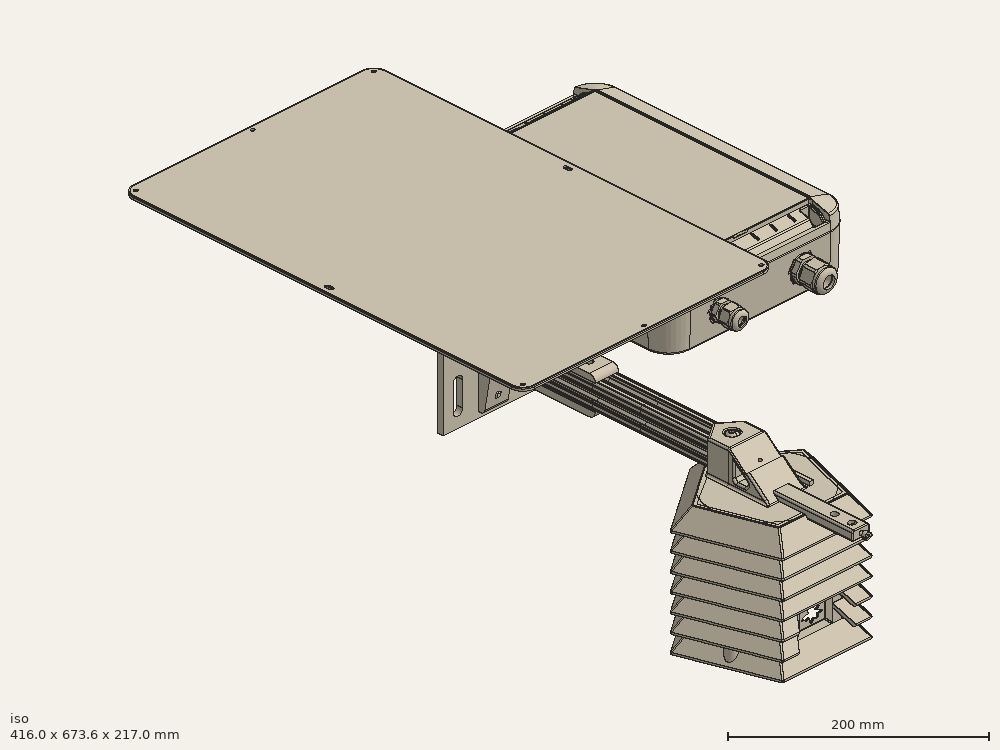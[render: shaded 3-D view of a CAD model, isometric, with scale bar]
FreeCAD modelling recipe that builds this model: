
FCSTD DOCUMENT  (FreeCAD 0.20R29410 (Git))
Label: SRSv2_0
License: All rights reserved
LicenseURL: http://en.wikipedia.org/wiki/All_rights_reserved
objects: Part::Feature×182, Sketcher::SketchObject×149, Part::Fillet×82, Part::MultiFuse×57, Part::Cylinder×56, Part::Extrusion×56, Part::Cut×55, App::Part×52, Part::Loft×44, Part::Sphere×3, Part::Box×2, Part::MultiCommon×2, Part::Cone×2, Part::Compound×1, Mesh::Feature×1
note: 691 computed .brp shape members not serialized (recipe doc carries the construction recipe); baked Part::Feature solids carry a one-line shape summary decoded from their .brp

FEATURE [Part::Feature] Part__Feature049  label="T-SlottedFramingScew"
  Placement = pos=(-0.00808436,-263.233,14.5255) rot=(0.577273,-0.577389,-0.577389;2.09434rad)
  shape: bbox 11.25 x 25.4 x 17.44 mm, 56 faces, 2 solids (baked)
FEATURE [Part::Feature] Part__Feature022  label="3136N138_T-Slotted Framing"
  shape: bbox 101.6 x 133.4 x 139.7 mm, 136 faces (baked)
FEATURE [Part::Feature] Part__Feature023  label="47065T801_T-Slotted Framing"
  Placement = pos=(0,100,0) rot=(-1,0,0;1.5708rad)
  shape: bbox 25.4 x 152.4 x 25.4 mm, 108 faces (baked)
FEATURE [Part::Feature] Part__Feature024  label="47065T801_T-Slotted Framing001"
  Placement = pos=(0,200,0) rot=(-1,0,0;1.5708rad)
  shape: bbox 25.4 x 152.4 x 25.4 mm, 108 faces (baked)
FEATURE [Part::MultiFuse] Fusion008  label="framingSupport"
  Placement = pos=(0,0,-3) rot=(0,0,1;3.14159rad)
  Shapes = -> [Part__Feature024,Part__Feature022,Part__Feature023]
FEATURE [Part::Box] Box  label="Cube"
  AttacherType = Attacher::AttachEngine3D
  Height = 12
  Length = 24
  Placement = pos=(-12,-341.5,-244.5) rot=(0,0,1;0rad)
  Width = 23
FEATURE [Part::Box] Box042  label="Cube030"
  AttacherType = Attacher::AttachEngine3D
  Height = 50
  Length = 25
  Placement = pos=(-11,-309,-310) rot=(0,0,1;0rad)
  Width = 25
FEATURE [Part::Cylinder] Cylinder
  Angle = 360
  AttacherType = Attacher::AttachEngine3D
  FirstAngle = 0
  Height = 15
  Placement = pos=(0,-287.79,-241.35) rot=(1,0,0;0.698132rad)
  Radius = 1.63
  SecondAngle = 0
FEATURE [Part::Cylinder] Cylinder128  label="base013"
  Angle = 360
  AttacherType = Attacher::AttachEngine3D
  FirstAngle = 0
  Height = 4.5
  Placement = pos=(136,0,65) rot=(0,0,1;0rad)
  Radius = 40
  SecondAngle = 0
FEATURE [Part::Cylinder] Cylinder129  label="baseCut002"
  Angle = 360
  AttacherType = Attacher::AttachEngine3D
  FirstAngle = 0
  Height = 7
  Placement = pos=(5,0,74) rot=(0,0,1;0rad)
  Radius = 24
  SecondAngle = 0
FEATURE [Part::Cylinder] Cylinder130
  Angle = 360
  AttacherType = Attacher::AttachEngine3D
  FirstAngle = 0
  Height = 1
  Placement = pos=(134,32.6,65) rot=(0,0,1;0rad)
  Radius = 5.5
  SecondAngle = 0
FEATURE [Part::Cylinder] Cylinder131
  Angle = 360
  AttacherType = Attacher::AttachEngine3D
  FirstAngle = 0
  Height = 5.82
  Placement = pos=(0,-21,0) rot=(0,0,1;0rad)
  Radius = 5
  SecondAngle = 0
FEATURE [Part::Cylinder] Cylinder132
  Angle = 360
  AttacherType = Attacher::AttachEngine3D
  FirstAngle = 0
  Height = 5.82
  Placement = pos=(20.5,-21,0) rot=(0,0,1;0rad)
  Radius = 5
  SecondAngle = 0
  expr: Radius = 5
FEATURE [Part::Cylinder] Cylinder133
  Angle = 360
  AttacherType = Attacher::AttachEngine3D
  FirstAngle = 0
  Height = 5.82
  Placement = pos=(0,-21,0) rot=(0,0,1;0rad)
  Radius = 5
  SecondAngle = 0
FEATURE [Part::Cylinder] Cylinder134
  Angle = 360
  AttacherType = Attacher::AttachEngine3D
  FirstAngle = 0
  Height = 5.82
  Placement = pos=(20.5,-21,0) rot=(0,0,1;0rad)
  Radius = 5
  SecondAngle = 0
FEATURE [Part::Cylinder] Cylinder139
  Angle = 360
  AttacherType = Attacher::AttachEngine3D
  FirstAngle = 0
  Height = 10
  Placement = pos=(0,-21,0) rot=(0,0,1;0rad)
  Radius = 2
  SecondAngle = 0
FEATURE [Part::Cylinder] Cylinder140
  Angle = 360
  AttacherType = Attacher::AttachEngine3D
  FirstAngle = 0
  Height = 10
  Placement = pos=(20.5,-21,0) rot=(0,0,1;0rad)
  Radius = 2
  SecondAngle = 0
FEATURE [Part::Cylinder] Cylinder141
  Angle = 360
  AttacherType = Attacher::AttachEngine3D
  FirstAngle = 0
  Height = 10
  Placement = pos=(0,-21,0) rot=(0,0,1;0rad)
  Radius = 2
  SecondAngle = 0
FEATURE [Part::Cylinder] Cylinder142
  Angle = 360
  AttacherType = Attacher::AttachEngine3D
  FirstAngle = 0
  Height = 10
  Placement = pos=(20.5,-21,0) rot=(0,0,1;0rad)
  Radius = 2
  SecondAngle = 0
FEATURE [Part::Cylinder] Cylinder143  label="WireCut003"
  Angle = 360
  AttacherType = Attacher::AttachEngine3D
  FirstAngle = 0
  Height = 60
  Placement = pos=(134,32.6,20) rot=(0,0,1;0rad)
  Radius = 2.5
  SecondAngle = 0
FEATURE [Part::Cylinder] Cylinder146
  Angle = 360
  AttacherType = Attacher::AttachEngine3D
  FirstAngle = 0
  Height = 50
  Placement = pos=(0,-302.012,-276.116) rot=(1,0,0;0.733038rad)
  Radius = 8
  SecondAngle = 0
FEATURE [Part::Cut] Cut039
  Base = -> Cylinder146
  Tool = -> Box
FEATURE [Part::Cylinder] Cylinder147  label="cut"
  Angle = 360
  AttacherType = Attacher::AttachEngine3D
  FirstAngle = 0
  Height = 50
  Placement = pos=(0,-300.005,-278.345) rot=(1,0,0;0.733038rad)
  Radius = 5
  SecondAngle = 0
FEATURE [Part::Cylinder] Cylinder148  label="m2HeatSetInsets016"
  Angle = 360
  AttacherType = Attacher::AttachEngine3D
  FirstAngle = 0
  Height = 10
  Placement = pos=(-35,0,65) rot=(0,0,1;0rad)
  Radius = 2
  SecondAngle = 0
  expr: Radius = 2
FEATURE [Part::Cylinder] Cylinder149  label="m2HeatSetInsets017"
  Angle = 360
  AttacherType = Attacher::AttachEngine3D
  FirstAngle = 0
  Height = 10
  Placement = pos=(35,0,65) rot=(0,0,1;0rad)
  Radius = 2
  SecondAngle = 0
FEATURE [Part::Cylinder] Cylinder150  label="m2HeatSetInsets018"
  Angle = 360
  AttacherType = Attacher::AttachEngine3D
  FirstAngle = 0
  Height = 10
  Placement = pos=(0,35,65) rot=(0,0,1;0rad)
  Radius = 2
  SecondAngle = 0
FEATURE [Part::Cylinder] Cylinder151  label="m2HeatSetInsets019"
  Angle = 360
  AttacherType = Attacher::AttachEngine3D
  FirstAngle = 0
  Height = 10
  Placement = pos=(0,-35,65) rot=(0,0,1;0rad)
  Radius = 2
  SecondAngle = 0
  expr: Radius = 2
FEATURE [Part::MultiFuse] Fusion079  label="m3HeatSetCuts015"
  Placement = pos=(-5,39,70) rot=(0,0,1;0rad)
  Shapes = -> [Cylinder132,Cylinder131]
FEATURE [Part::MultiFuse] Fusion080  label="m3HeatSetCuts016"
  Placement = pos=(-5,3,70) rot=(0,0,1;0rad)
  Shapes = -> [Cylinder134,Cylinder133]
FEATURE [Part::MultiFuse] Fusion081  label="m3HeatSetCuts017"
  Placement = pos=(128.75,10,-1) rot=(0,0,1;0rad)
  Shapes = -> [Fusion080,Fusion079]
FEATURE [Part::MultiFuse] Fusion086  label="m3HeatSetCuts019"
  Placement = pos=(-5,39,70) rot=(0,0,1;0rad)
  Shapes = -> [Cylinder140,Cylinder139]
FEATURE [Part::MultiFuse] Fusion087  label="m3HeatSetCuts020"
  Placement = pos=(-5,3,70) rot=(0,0,1;0rad)
  Shapes = -> [Cylinder142,Cylinder141]
FEATURE [Part::MultiFuse] Fusion085  label="m3HeatSetCuts018"
  Placement = pos=(128.75,10,-1) rot=(0,0,1;0rad)
  Shapes = -> [Fusion087,Fusion086]
FEATURE [Part::MultiFuse] Fusion088  label="lightModuleCut004"
  Shapes = -> [Fusion085,Cylinder143]
FEATURE [Part::MultiFuse] Fusion092
  Placement = pos=(0,-350,-314) rot=(0,0,-1;0.785398rad)
  Shapes = -> [Cylinder148,Cylinder149,Cylinder150,Cylinder151]
FEATURE [Part::Feature] Part__Feature153  label="logoTopCut"
  Placement = pos=(-30.8,-333,-323.9) rot=(0,0,1;0rad)
  shape: bbox 22.79 x 8 x 17.08 mm, 886 faces (baked)
FEATURE [Sketcher::SketchObject] Sketch003  label="inner"
  FullyConstrained = true
  Placement = pos=(0,0,-259.26) rot=(0,0,1;0rad)
  sketch-geometry (4):
    g0: LineSegment StartX=-30 StartY=-277 StartZ=0 EndX=-30 EndY=-327 EndZ=0
    g1: LineSegment StartX=-30 StartY=-327 StartZ=0 EndX=30 EndY=-327 EndZ=0
    g2: LineSegment StartX=30 StartY=-327 StartZ=0 EndX=30 EndY=-277 EndZ=0
    g3: LineSegment StartX=30 StartY=-277 StartZ=0 EndX=-30 EndY=-277 EndZ=0
  constraints (12):
    c: Vertical(g0)
    c: Coincident(g1,g0)
    c: Horizontal(g1)
    c: Coincident(g2,g1)
    c: Vertical(g2)
    c: Coincident(g3,g2)
    c: Coincident(g3,g0)
    c: Horizontal(g3)
    c: DistanceX(g0) = -30
    c: DistanceX(g1) = 30
    c: DistanceY(g0) = -327
    c: DistanceY(g0,g0) = 50
FEATURE [Sketcher::SketchObject] Sketch004  label="outer"
  FullyConstrained = true
  Placement = pos=(0,0,-281.2) rot=(0,0,1;0rad)
  sketch-geometry (4):
    g0: LineSegment StartX=-59 StartY=-252 StartZ=0 EndX=-59 EndY=-352 EndZ=0
    g1: LineSegment StartX=-59 StartY=-352 StartZ=0 EndX=59 EndY=-352 EndZ=0
    g2: LineSegment StartX=59 StartY=-352 StartZ=0 EndX=59 EndY=-252 EndZ=0
    g3: LineSegment StartX=59 StartY=-252 StartZ=0 EndX=-59 EndY=-252 EndZ=0
  constraints (12):
    c: Vertical(g0)
    c: Coincident(g1,g0)
    c: Horizontal(g1)
    c: Coincident(g2,g1)
    c: Vertical(g2)
    c: Coincident(g3,g2)
    c: Coincident(g3,g0)
    c: Horizontal(g3)
    c: DistanceX(g0) = -59
    c: DistanceX(g1) = 59
    c: DistanceY(g0) = -352
    c: DistanceY(g0,g0) = 100
FEATURE [Part::Loft] Loft
  Closed = false
  MaxDegree = 5
  Ruled = false
  Sections = -> [Sketch003,Sketch004]
  Solid = true
FEATURE [Part::Fillet] Fillet
  Base = -> Loft
  Edges = 12 edges r=3: [Edge1,Edge2,Edge3,Edge4,Edge5,Edge6,Edge7,Edge8,Edge9,Edge10,Edge11,Edge12]
FEATURE [Sketcher::SketchObject] Sketch005  label="inner001"
  FullyConstrained = true
  Placement = pos=(0,0,-259.26) rot=(0,0,1;0rad)
  sketch-geometry (4):
    g0: LineSegment StartX=-30 StartY=-277 StartZ=0 EndX=-30 EndY=-327 EndZ=0
    g1: LineSegment StartX=-30 StartY=-327 StartZ=0 EndX=30 EndY=-327 EndZ=0
    g2: LineSegment StartX=30 StartY=-327 StartZ=0 EndX=30 EndY=-277 EndZ=0
    g3: LineSegment StartX=30 StartY=-277 StartZ=0 EndX=-30 EndY=-277 EndZ=0
  constraints (12):
    c: Vertical(g0)
    c: Coincident(g1,g0)
    c: Horizontal(g1)
    c: Coincident(g2,g1)
    c: Vertical(g2)
    c: Coincident(g3,g2)
    c: Coincident(g3,g0)
    c: Horizontal(g3)
    c: DistanceX(g0) = -30
    c: DistanceX(g1) = 30
    c: DistanceY(g0) = -327
    c: DistanceY(g0,g0) = 50
FEATURE [Sketcher::SketchObject] Sketch006  label="outer001"
  FullyConstrained = true
  Placement = pos=(0,0,-281.2) rot=(0,0,1;0rad)
  sketch-geometry (4):
    g0: LineSegment StartX=-59 StartY=-252 StartZ=0 EndX=-59 EndY=-352 EndZ=0
    g1: LineSegment StartX=-59 StartY=-352 StartZ=0 EndX=59 EndY=-352 EndZ=0
    g2: LineSegment StartX=59 StartY=-352 StartZ=0 EndX=59 EndY=-252 EndZ=0
    g3: LineSegment StartX=59 StartY=-252 StartZ=0 EndX=-59 EndY=-252 EndZ=0
  constraints (12):
    c: Vertical(g0)
    c: Coincident(g1,g0)
    c: Horizontal(g1)
    c: Coincident(g2,g1)
    c: Vertical(g2)
    c: Coincident(g3,g2)
    c: Coincident(g3,g0)
    c: Horizontal(g3)
    c: DistanceX(g0) = -59
    c: DistanceX(g1) = 59
    c: DistanceY(g0) = -352
    c: DistanceY(g0,g0) = 100
FEATURE [Part::Loft] Loft001
  Closed = false
  MaxDegree = 5
  Ruled = false
  Sections = -> [Sketch005,Sketch006]
  Solid = true
FEATURE [Part::Fillet] Fillet009
  Base = -> Loft001
  Edges = 12 edges r=3: [Edge1,Edge2,Edge3,Edge4,Edge5,Edge6,Edge7,Edge8,Edge9,Edge10,Edge11,Edge12]
  Placement = pos=(0,0,-4) rot=(0,0,1;0rad)
FEATURE [Part::Cut] Cut  label="sls01"
  Base = -> Fillet
  Tool = -> Fillet009
FEATURE [Sketcher::SketchObject] Sketch007  label="inner002"
  FullyConstrained = true
  Placement = pos=(0,0,-259.26) rot=(0,0,1;0rad)
  sketch-geometry (4):
    g0: LineSegment StartX=-30 StartY=-277 StartZ=0 EndX=-30 EndY=-327 EndZ=0
    g1: LineSegment StartX=-30 StartY=-327 StartZ=0 EndX=30 EndY=-327 EndZ=0
    g2: LineSegment StartX=30 StartY=-327 StartZ=0 EndX=30 EndY=-277 EndZ=0
    g3: LineSegment StartX=30 StartY=-277 StartZ=0 EndX=-30 EndY=-277 EndZ=0
  constraints (12):
    c: Vertical(g0)
    c: Coincident(g1,g0)
    c: Horizontal(g1)
    c: Coincident(g2,g1)
    c: Vertical(g2)
    c: Coincident(g3,g2)
    c: Coincident(g3,g0)
    c: Horizontal(g3)
    c: DistanceX(g0) = -30
    c: DistanceX(g1) = 30
    c: DistanceY(g0) = -327
    c: DistanceY(g0,g0) = 50
FEATURE [Sketcher::SketchObject] Sketch008  label="outer002"
  FullyConstrained = true
  Placement = pos=(0,0,-281.2) rot=(0,0,1;0rad)
  sketch-geometry (4):
    g0: LineSegment StartX=-59 StartY=-252 StartZ=0 EndX=-59 EndY=-352 EndZ=0
    g1: LineSegment StartX=-59 StartY=-352 StartZ=0 EndX=59 EndY=-352 EndZ=0
    g2: LineSegment StartX=59 StartY=-352 StartZ=0 EndX=59 EndY=-252 EndZ=0
    g3: LineSegment StartX=59 StartY=-252 StartZ=0 EndX=-59 EndY=-252 EndZ=0
  constraints (12):
    c: Vertical(g0)
    c: Coincident(g1,g0)
    c: Horizontal(g1)
    c: Coincident(g2,g1)
    c: Vertical(g2)
    c: Coincident(g3,g2)
    c: Coincident(g3,g0)
    c: Horizontal(g3)
    c: DistanceX(g0) = -59
    c: DistanceX(g1) = 59
    c: DistanceY(g0) = -352
    c: DistanceY(g0,g0) = 100
FEATURE [Part::Loft] Loft002
  Closed = false
  MaxDegree = 5
  Ruled = false
  Sections = -> [Sketch007,Sketch008]
  Solid = true
FEATURE [Part::Fillet] Fillet010
  Base = -> Loft002
  Edges = 12 edges r=3: [Edge1,Edge2,Edge3,Edge4,Edge5,Edge6,Edge7,Edge8,Edge9,Edge10,Edge11,Edge12]
FEATURE [Sketcher::SketchObject] Sketch009  label="inner003"
  FullyConstrained = true
  Placement = pos=(0,0,-259.26) rot=(0,0,1;0rad)
  sketch-geometry (4):
    g0: LineSegment StartX=-30 StartY=-277 StartZ=0 EndX=-30 EndY=-327 EndZ=0
    g1: LineSegment StartX=-30 StartY=-327 StartZ=0 EndX=30 EndY=-327 EndZ=0
    g2: LineSegment StartX=30 StartY=-327 StartZ=0 EndX=30 EndY=-277 EndZ=0
    g3: LineSegment StartX=30 StartY=-277 StartZ=0 EndX=-30 EndY=-277 EndZ=0
  constraints (12):
    c: Vertical(g0)
    c: Coincident(g1,g0)
    c: Horizontal(g1)
    c: Coincident(g2,g1)
    c: Vertical(g2)
    c: Coincident(g3,g2)
    c: Coincident(g3,g0)
    c: Horizontal(g3)
    c: DistanceX(g0) = -30
    c: DistanceX(g1) = 30
    c: DistanceY(g0) = -327
    c: DistanceY(g0,g0) = 50
FEATURE [Sketcher::SketchObject] Sketch010  label="outer003"
  FullyConstrained = true
  Placement = pos=(0,0,-281.2) rot=(0,0,1;0rad)
  sketch-geometry (4):
    g0: LineSegment StartX=-59 StartY=-252 StartZ=0 EndX=-59 EndY=-352 EndZ=0
    g1: LineSegment StartX=-59 StartY=-352 StartZ=0 EndX=59 EndY=-352 EndZ=0
    g2: LineSegment StartX=59 StartY=-352 StartZ=0 EndX=59 EndY=-252 EndZ=0
    g3: LineSegment StartX=59 StartY=-252 StartZ=0 EndX=-59 EndY=-252 EndZ=0
  constraints (12):
    c: Vertical(g0)
    c: Coincident(g1,g0)
    c: Horizontal(g1)
    c: Coincident(g2,g1)
    c: Vertical(g2)
    c: Coincident(g3,g2)
    c: Coincident(g3,g0)
    c: Horizontal(g3)
    c: DistanceX(g0) = -59
    c: DistanceX(g1) = 59
    c: DistanceY(g0) = -352
    c: DistanceY(g0,g0) = 100
FEATURE [Part::Loft] Loft003
  Closed = false
  MaxDegree = 5
  Ruled = false
  Sections = -> [Sketch009,Sketch010]
  Solid = true
FEATURE [Part::Fillet] Fillet011
  Base = -> Loft003
  Edges = 12 edges r=3: [Edge1,Edge2,Edge3,Edge4,Edge5,Edge6,Edge7,Edge8,Edge9,Edge10,Edge11,Edge12]
  Placement = pos=(0,0,-4) rot=(0,0,1;0rad)
FEATURE [Part::Cut] Cut004  label="sls002"
  Base = -> Fillet010
  Placement = pos=(0,0,-16) rot=(0,0,1;0rad)
  Tool = -> Fillet011
FEATURE [Sketcher::SketchObject] Sketch011  label="inner004"
  FullyConstrained = true
  Placement = pos=(0,0,-259.26) rot=(0,0,1;0rad)
  sketch-geometry (4):
    g0: LineSegment StartX=-30 StartY=-277 StartZ=0 EndX=-30 EndY=-327 EndZ=0
    g1: LineSegment StartX=-30 StartY=-327 StartZ=0 EndX=30 EndY=-327 EndZ=0
    g2: LineSegment StartX=30 StartY=-327 StartZ=0 EndX=30 EndY=-277 EndZ=0
    g3: LineSegment StartX=30 StartY=-277 StartZ=0 EndX=-30 EndY=-277 EndZ=0
  constraints (12):
    c: Vertical(g0)
    c: Coincident(g1,g0)
    c: Horizontal(g1)
    c: Coincident(g2,g1)
    c: Vertical(g2)
    c: Coincident(g3,g2)
    c: Coincident(g3,g0)
    c: Horizontal(g3)
    c: DistanceX(g0) = -30
    c: DistanceX(g1) = 30
    c: DistanceY(g0) = -327
    c: DistanceY(g0,g0) = 50
FEATURE [Sketcher::SketchObject] Sketch012  label="outer004"
  FullyConstrained = true
  Placement = pos=(0,0,-281.2) rot=(0,0,1;0rad)
  sketch-geometry (4):
    g0: LineSegment StartX=-59 StartY=-252 StartZ=0 EndX=-59 EndY=-352 EndZ=0
    g1: LineSegment StartX=-59 StartY=-352 StartZ=0 EndX=59 EndY=-352 EndZ=0
    g2: LineSegment StartX=59 StartY=-352 StartZ=0 EndX=59 EndY=-252 EndZ=0
    g3: LineSegment StartX=59 StartY=-252 StartZ=0 EndX=-59 EndY=-252 EndZ=0
  constraints (12):
    c: Vertical(g0)
    c: Coincident(g1,g0)
    c: Horizontal(g1)
    c: Coincident(g2,g1)
    c: Vertical(g2)
    c: Coincident(g3,g2)
    c: Coincident(g3,g0)
    c: Horizontal(g3)
    c: DistanceX(g0) = -59
    c: DistanceX(g1) = 59
    c: DistanceY(g0) = -352
    c: DistanceY(g0,g0) = 100
FEATURE [Part::Loft] Loft004
  Closed = false
  MaxDegree = 5
  Ruled = false
  Sections = -> [Sketch011,Sketch012]
  Solid = true
FEATURE [Part::Fillet] Fillet012
  Base = -> Loft004
  Edges = 12 edges r=3: [Edge1,Edge2,Edge3,Edge4,Edge5,Edge6,Edge7,Edge8,Edge9,Edge10,Edge11,Edge12]
FEATURE [Sketcher::SketchObject] Sketch013  label="inner005"
  FullyConstrained = true
  Placement = pos=(0,0,-259.26) rot=(0,0,1;0rad)
  sketch-geometry (4):
    g0: LineSegment StartX=-30 StartY=-277 StartZ=0 EndX=-30 EndY=-327 EndZ=0
    g1: LineSegment StartX=-30 StartY=-327 StartZ=0 EndX=30 EndY=-327 EndZ=0
    g2: LineSegment StartX=30 StartY=-327 StartZ=0 EndX=30 EndY=-277 EndZ=0
    g3: LineSegment StartX=30 StartY=-277 StartZ=0 EndX=-30 EndY=-277 EndZ=0
  constraints (12):
    c: Vertical(g0)
    c: Coincident(g1,g0)
    c: Horizontal(g1)
    c: Coincident(g2,g1)
    c: Vertical(g2)
    c: Coincident(g3,g2)
    c: Coincident(g3,g0)
    c: Horizontal(g3)
    c: DistanceX(g0) = -30
    c: DistanceX(g1) = 30
    c: DistanceY(g0) = -327
    c: DistanceY(g0,g0) = 50
FEATURE [Sketcher::SketchObject] Sketch014  label="outer005"
  FullyConstrained = true
  Placement = pos=(0,0,-281.2) rot=(0,0,1;0rad)
  sketch-geometry (4):
    g0: LineSegment StartX=-59 StartY=-252 StartZ=0 EndX=-59 EndY=-352 EndZ=0
    g1: LineSegment StartX=-59 StartY=-352 StartZ=0 EndX=59 EndY=-352 EndZ=0
    g2: LineSegment StartX=59 StartY=-352 StartZ=0 EndX=59 EndY=-252 EndZ=0
    g3: LineSegment StartX=59 StartY=-252 StartZ=0 EndX=-59 EndY=-252 EndZ=0
  constraints (12):
    c: Vertical(g0)
    c: Coincident(g1,g0)
    c: Horizontal(g1)
    c: Coincident(g2,g1)
    c: Vertical(g2)
    c: Coincident(g3,g2)
    c: Coincident(g3,g0)
    c: Horizontal(g3)
    c: DistanceX(g0) = -59
    c: DistanceX(g1) = 59
    c: DistanceY(g0) = -352
    c: DistanceY(g0,g0) = 100
FEATURE [Part::Loft] Loft005
  Closed = false
  MaxDegree = 5
  Ruled = false
  Sections = -> [Sketch013,Sketch014]
  Solid = true
FEATURE [Part::Fillet] Fillet013
  Base = -> Loft005
  Edges = 12 edges r=3: [Edge1,Edge2,Edge3,Edge4,Edge5,Edge6,Edge7,Edge8,Edge9,Edge10,Edge11,Edge12]
  Placement = pos=(0,0,-4) rot=(0,0,1;0rad)
FEATURE [Part::Cut] Cut005  label="sls003"
  Base = -> Fillet012
  Placement = pos=(0,0,-32) rot=(0,0,1;0rad)
  Tool = -> Fillet013
FEATURE [Sketcher::SketchObject] Sketch015  label="inner006"
  FullyConstrained = true
  Placement = pos=(0,0,-259.26) rot=(0,0,1;0rad)
  sketch-geometry (4):
    g0: LineSegment StartX=-30 StartY=-277 StartZ=0 EndX=-30 EndY=-327 EndZ=0
    g1: LineSegment StartX=-30 StartY=-327 StartZ=0 EndX=30 EndY=-327 EndZ=0
    g2: LineSegment StartX=30 StartY=-327 StartZ=0 EndX=30 EndY=-277 EndZ=0
    g3: LineSegment StartX=30 StartY=-277 StartZ=0 EndX=-30 EndY=-277 EndZ=0
  constraints (12):
    c: Vertical(g0)
    c: Coincident(g1,g0)
    c: Horizontal(g1)
    c: Coincident(g2,g1)
    c: Vertical(g2)
    c: Coincident(g3,g2)
    c: Coincident(g3,g0)
    c: Horizontal(g3)
    c: DistanceX(g0) = -30
    c: DistanceX(g1) = 30
    c: DistanceY(g0) = -327
    c: DistanceY(g0,g0) = 50
FEATURE [Sketcher::SketchObject] Sketch016  label="outer006"
  FullyConstrained = true
  Placement = pos=(0,0,-281.2) rot=(0,0,1;0rad)
  sketch-geometry (4):
    g0: LineSegment StartX=-59 StartY=-252 StartZ=0 EndX=-59 EndY=-352 EndZ=0
    g1: LineSegment StartX=-59 StartY=-352 StartZ=0 EndX=59 EndY=-352 EndZ=0
    g2: LineSegment StartX=59 StartY=-352 StartZ=0 EndX=59 EndY=-252 EndZ=0
    g3: LineSegment StartX=59 StartY=-252 StartZ=0 EndX=-59 EndY=-252 EndZ=0
  constraints (12):
    c: Vertical(g0)
    c: Coincident(g1,g0)
    c: Horizontal(g1)
    c: Coincident(g2,g1)
    c: Vertical(g2)
    c: Coincident(g3,g2)
    c: Coincident(g3,g0)
    c: Horizontal(g3)
    c: DistanceX(g0) = -59
    c: DistanceX(g1) = 59
    c: DistanceY(g0) = -352
    c: DistanceY(g0,g0) = 100
FEATURE [Part::Loft] Loft006
  Closed = false
  MaxDegree = 5
  Ruled = false
  Sections = -> [Sketch015,Sketch016]
  Solid = true
FEATURE [Part::Fillet] Fillet014
  Base = -> Loft006
  Edges = 12 edges r=3: [Edge1,Edge2,Edge3,Edge4,Edge5,Edge6,Edge7,Edge8,Edge9,Edge10,Edge11,Edge12]
FEATURE [Sketcher::SketchObject] Sketch017  label="inner007"
  FullyConstrained = true
  Placement = pos=(0,0,-259.26) rot=(0,0,1;0rad)
  sketch-geometry (4):
    g0: LineSegment StartX=-30 StartY=-277 StartZ=0 EndX=-30 EndY=-327 EndZ=0
    g1: LineSegment StartX=-30 StartY=-327 StartZ=0 EndX=30 EndY=-327 EndZ=0
    g2: LineSegment StartX=30 StartY=-327 StartZ=0 EndX=30 EndY=-277 EndZ=0
    g3: LineSegment StartX=30 StartY=-277 StartZ=0 EndX=-30 EndY=-277 EndZ=0
  constraints (12):
    c: Vertical(g0)
    c: Coincident(g1,g0)
    c: Horizontal(g1)
    c: Coincident(g2,g1)
    c: Vertical(g2)
    c: Coincident(g3,g2)
    c: Coincident(g3,g0)
    c: Horizontal(g3)
    c: DistanceX(g0) = -30
    c: DistanceX(g1) = 30
    c: DistanceY(g0) = -327
    c: DistanceY(g0,g0) = 50
FEATURE [Sketcher::SketchObject] Sketch018  label="outer007"
  FullyConstrained = true
  Placement = pos=(0,0,-281.2) rot=(0,0,1;0rad)
  sketch-geometry (4):
    g0: LineSegment StartX=-59 StartY=-252 StartZ=0 EndX=-59 EndY=-352 EndZ=0
    g1: LineSegment StartX=-59 StartY=-352 StartZ=0 EndX=59 EndY=-352 EndZ=0
    g2: LineSegment StartX=59 StartY=-352 StartZ=0 EndX=59 EndY=-252 EndZ=0
    g3: LineSegment StartX=59 StartY=-252 StartZ=0 EndX=-59 EndY=-252 EndZ=0
  constraints (12):
    c: Vertical(g0)
    c: Coincident(g1,g0)
    c: Horizontal(g1)
    c: Coincident(g2,g1)
    c: Vertical(g2)
    c: Coincident(g3,g2)
    c: Coincident(g3,g0)
    c: Horizontal(g3)
    c: DistanceX(g0) = -59
    c: DistanceX(g1) = 59
    c: DistanceY(g0) = -352
    c: DistanceY(g0,g0) = 100
FEATURE [Part::Loft] Loft007
  Closed = false
  MaxDegree = 5
  Ruled = false
  Sections = -> [Sketch017,Sketch018]
  Solid = true
FEATURE [Part::Fillet] Fillet015
  Base = -> Loft007
  Edges = 12 edges r=3: [Edge1,Edge2,Edge3,Edge4,Edge5,Edge6,Edge7,Edge8,Edge9,Edge10,Edge11,Edge12]
  Placement = pos=(0,0,-4) rot=(0,0,1;0rad)
FEATURE [Part::Cut] Cut006  label="sls004"
  Base = -> Fillet014
  Placement = pos=(0,0,-48) rot=(0,0,1;0rad)
  Tool = -> Fillet015
FEATURE [Part::MultiFuse] Fusion036  label="slsBottom"
  Shapes = -> [Cut006,Cut005]
FEATURE [Sketcher::SketchObject] Sketch023
  FullyConstrained = true
  sketch-geometry (4):
    g0: Circle CenterX=-35 CenterY=-332 CenterZ=0 NormalX=0 NormalY=0 NormalZ=1 AngleXU=0 Radius=5.5
    g1: Circle CenterX=35 CenterY=-332 CenterZ=0 NormalX=0 NormalY=0 NormalZ=1 AngleXU=0 Radius=5.5
    g2: Circle CenterX=35 CenterY=-272 CenterZ=0 NormalX=0 NormalY=0 NormalZ=1 AngleXU=0 Radius=5.5
    g3: Circle CenterX=-35 CenterY=-272 CenterZ=0 NormalX=0 NormalY=0 NormalZ=1 AngleXU=0 Radius=5.5
  constraints (12):
    c: DistanceX(g0) = -35
    c: DistanceY(g0) = -332
    c: Equal(g0,g3)
    c: Equal(g0,g2)
    c: Equal(g0,g1)
    c: Diameter(g0) = 11
    c: DistanceX(g3,g0) = 0
    c: DistanceY(g0,g3) = 60
    c: DistanceY(g2,g3) = 0
    c: DistanceY(g0,g1) = 0
    c: DistanceX(g2,g1) = 0
    c: DistanceX(g1) = 35
FEATURE [Part::Extrusion] Extrude007  label="stands"
  Base = -> Sketch023
  Dir = (0,0,1)
  DirMode = 2
  FaceMakerClass = Part::FaceMakerBullseye
  LengthFwd = 69
  LengthRev = 0
  Placement = pos=(0,0,-323) rot=(0,0,1;0rad)
  Solid = true
  Symmetric = false
FEATURE [Sketcher::SketchObject] Sketch024  label="inner008"
  FullyConstrained = true
  Placement = pos=(0,0,-259.26) rot=(0,0,1;0rad)
  sketch-geometry (4):
    g0: LineSegment StartX=-30 StartY=-277 StartZ=0 EndX=-30 EndY=-327 EndZ=0
    g1: LineSegment StartX=-30 StartY=-327 StartZ=0 EndX=30 EndY=-327 EndZ=0
    g2: LineSegment StartX=30 StartY=-327 StartZ=0 EndX=30 EndY=-277 EndZ=0
    g3: LineSegment StartX=30 StartY=-277 StartZ=0 EndX=-30 EndY=-277 EndZ=0
  constraints (12):
    c: Vertical(g0)
    c: Coincident(g1,g0)
    c: Horizontal(g1)
    c: Coincident(g2,g1)
    c: Vertical(g2)
    c: Coincident(g3,g2)
    c: Coincident(g3,g0)
    c: Horizontal(g3)
    c: DistanceX(g0) = -30
    c: DistanceX(g1) = 30
    c: DistanceY(g0) = -327
    c: DistanceY(g0,g0) = 50
FEATURE [Sketcher::SketchObject] Sketch025  label="outer008"
  FullyConstrained = true
  Placement = pos=(0,0,-281.2) rot=(0,0,1;0rad)
  sketch-geometry (4):
    g0: LineSegment StartX=-59 StartY=-252 StartZ=0 EndX=-59 EndY=-352 EndZ=0
    g1: LineSegment StartX=-59 StartY=-352 StartZ=0 EndX=59 EndY=-352 EndZ=0
    g2: LineSegment StartX=59 StartY=-352 StartZ=0 EndX=59 EndY=-252 EndZ=0
    g3: LineSegment StartX=59 StartY=-252 StartZ=0 EndX=-59 EndY=-252 EndZ=0
  constraints (12):
    c: Vertical(g0)
    c: Coincident(g1,g0)
    c: Horizontal(g1)
    c: Coincident(g2,g1)
    c: Vertical(g2)
    c: Coincident(g3,g2)
    c: Coincident(g3,g0)
    c: Horizontal(g3)
    c: DistanceX(g0) = -59
    c: DistanceX(g1) = 59
    c: DistanceY(g0) = -352
    c: DistanceY(g0,g0) = 100
FEATURE [Part::Loft] Loft008
  Closed = false
  MaxDegree = 5
  Ruled = false
  Sections = -> [Sketch024,Sketch025]
  Solid = true
FEATURE [Part::Fillet] Fillet016
  Base = -> Loft008
  Edges = 12 edges r=3: [Edge1,Edge2,Edge3,Edge4,Edge5,Edge6,Edge7,Edge8,Edge9,Edge10,Edge11,Edge12]
FEATURE [Sketcher::SketchObject] Sketch026  label="inner009"
  FullyConstrained = true
  Placement = pos=(0,0,-259.26) rot=(0,0,1;0rad)
  sketch-geometry (4):
    g0: LineSegment StartX=-30 StartY=-277 StartZ=0 EndX=-30 EndY=-327 EndZ=0
    g1: LineSegment StartX=-30 StartY=-327 StartZ=0 EndX=30 EndY=-327 EndZ=0
    g2: LineSegment StartX=30 StartY=-327 StartZ=0 EndX=30 EndY=-277 EndZ=0
    g3: LineSegment StartX=30 StartY=-277 StartZ=0 EndX=-30 EndY=-277 EndZ=0
  constraints (12):
    c: Vertical(g0)
    c: Coincident(g1,g0)
    c: Horizontal(g1)
    c: Coincident(g2,g1)
    c: Vertical(g2)
    c: Coincident(g3,g2)
    c: Coincident(g3,g0)
    c: Horizontal(g3)
    c: DistanceX(g0) = -30
    c: DistanceX(g1) = 30
    c: DistanceY(g0) = -327
    c: DistanceY(g0,g0) = 50
FEATURE [Sketcher::SketchObject] Sketch027  label="outer009"
  FullyConstrained = true
  Placement = pos=(0,0,-281.2) rot=(0,0,1;0rad)
  sketch-geometry (4):
    g0: LineSegment StartX=-59 StartY=-252 StartZ=0 EndX=-59 EndY=-352 EndZ=0
    g1: LineSegment StartX=-59 StartY=-352 StartZ=0 EndX=59 EndY=-352 EndZ=0
    g2: LineSegment StartX=59 StartY=-352 StartZ=0 EndX=59 EndY=-252 EndZ=0
    g3: LineSegment StartX=59 StartY=-252 StartZ=0 EndX=-59 EndY=-252 EndZ=0
  constraints (12):
    c: Vertical(g0)
    c: Coincident(g1,g0)
    c: Horizontal(g1)
    c: Coincident(g2,g1)
    c: Vertical(g2)
    c: Coincident(g3,g2)
    c: Coincident(g3,g0)
    c: Horizontal(g3)
    c: DistanceX(g0) = -59
    c: DistanceX(g1) = 59
    c: DistanceY(g0) = -352
    c: DistanceY(g0,g0) = 100
FEATURE [Part::Loft] Loft009
  Closed = false
  MaxDegree = 5
  Ruled = false
  Sections = -> [Sketch026,Sketch027]
  Solid = true
FEATURE [Part::Fillet] Fillet017
  Base = -> Loft009
  Edges = 12 edges r=3: [Edge1,Edge2,Edge3,Edge4,Edge5,Edge6,Edge7,Edge8,Edge9,Edge10,Edge11,Edge12]
  Placement = pos=(0,0,-4) rot=(0,0,1;0rad)
FEATURE [Part::Cut] Cut007  label="sls005"
  Base = -> Fillet016
  Placement = pos=(0,0,4) rot=(0,0,1;0rad)
  Tool = -> Fillet017
FEATURE [Sketcher::SketchObject] Sketch028  label="inner010"
  FullyConstrained = true
  Placement = pos=(0,0,-259.26) rot=(0,0,1;0rad)
  sketch-geometry (4):
    g0: LineSegment StartX=-30 StartY=-277 StartZ=0 EndX=-30 EndY=-327 EndZ=0
    g1: LineSegment StartX=-30 StartY=-327 StartZ=0 EndX=30 EndY=-327 EndZ=0
    g2: LineSegment StartX=30 StartY=-327 StartZ=0 EndX=30 EndY=-277 EndZ=0
    g3: LineSegment StartX=30 StartY=-277 StartZ=0 EndX=-30 EndY=-277 EndZ=0
  constraints (12):
    c: Vertical(g0)
    c: Coincident(g1,g0)
    c: Horizontal(g1)
    c: Coincident(g2,g1)
    c: Vertical(g2)
    c: Coincident(g3,g2)
    c: Coincident(g3,g0)
    c: Horizontal(g3)
    c: DistanceX(g0) = -30
    c: DistanceX(g1) = 30
    c: DistanceY(g0) = -327
    c: DistanceY(g0,g0) = 50
FEATURE [Sketcher::SketchObject] Sketch029  label="outer010"
  FullyConstrained = true
  Placement = pos=(0,0,-281.2) rot=(0,0,1;0rad)
  sketch-geometry (4):
    g0: LineSegment StartX=-59 StartY=-252 StartZ=0 EndX=-59 EndY=-352 EndZ=0
    g1: LineSegment StartX=-59 StartY=-352 StartZ=0 EndX=59 EndY=-352 EndZ=0
    g2: LineSegment StartX=59 StartY=-352 StartZ=0 EndX=59 EndY=-252 EndZ=0
    g3: LineSegment StartX=59 StartY=-252 StartZ=0 EndX=-59 EndY=-252 EndZ=0
  constraints (12):
    c: Vertical(g0)
    c: Coincident(g1,g0)
    c: Horizontal(g1)
    c: Coincident(g2,g1)
    c: Vertical(g2)
    c: Coincident(g3,g2)
    c: Coincident(g3,g0)
    c: Horizontal(g3)
    c: DistanceX(g0) = -59
    c: DistanceX(g1) = 59
    c: DistanceY(g0) = -352
    c: DistanceY(g0,g0) = 100
FEATURE [Part::Loft] Loft010
  Closed = false
  MaxDegree = 5
  Ruled = false
  Sections = -> [Sketch028,Sketch029]
  Solid = true
FEATURE [Part::Fillet] Fillet018
  Base = -> Loft010
  Edges = 12 edges r=3: [Edge1,Edge2,Edge3,Edge4,Edge5,Edge6,Edge7,Edge8,Edge9,Edge10,Edge11,Edge12]
FEATURE [Sketcher::SketchObject] Sketch030  label="inner011"
  FullyConstrained = true
  Placement = pos=(0,0,-259.26) rot=(0,0,1;0rad)
  sketch-geometry (4):
    g0: LineSegment StartX=-30 StartY=-277 StartZ=0 EndX=-30 EndY=-327 EndZ=0
    g1: LineSegment StartX=-30 StartY=-327 StartZ=0 EndX=30 EndY=-327 EndZ=0
    g2: LineSegment StartX=30 StartY=-327 StartZ=0 EndX=30 EndY=-277 EndZ=0
    g3: LineSegment StartX=30 StartY=-277 StartZ=0 EndX=-30 EndY=-277 EndZ=0
  constraints (12):
    c: Vertical(g0)
    c: Coincident(g1,g0)
    c: Horizontal(g1)
    c: Coincident(g2,g1)
    c: Vertical(g2)
    c: Coincident(g3,g2)
    c: Coincident(g3,g0)
    c: Horizontal(g3)
    c: DistanceX(g0) = -30
    c: DistanceX(g1) = 30
    c: DistanceY(g0) = -327
    c: DistanceY(g0,g0) = 50
FEATURE [Sketcher::SketchObject] Sketch031  label="outer011"
  FullyConstrained = true
  Placement = pos=(0,0,-281.2) rot=(0,0,1;0rad)
  sketch-geometry (4):
    g0: LineSegment StartX=-59 StartY=-252 StartZ=0 EndX=-59 EndY=-352 EndZ=0
    g1: LineSegment StartX=-59 StartY=-352 StartZ=0 EndX=59 EndY=-352 EndZ=0
    g2: LineSegment StartX=59 StartY=-352 StartZ=0 EndX=59 EndY=-252 EndZ=0
    g3: LineSegment StartX=59 StartY=-252 StartZ=0 EndX=-59 EndY=-252 EndZ=0
  constraints (12):
    c: Vertical(g0)
    c: Coincident(g1,g0)
    c: Horizontal(g1)
    c: Coincident(g2,g1)
    c: Vertical(g2)
    c: Coincident(g3,g2)
    c: Coincident(g3,g0)
    c: Horizontal(g3)
    c: DistanceX(g0) = -59
    c: DistanceX(g1) = 59
    c: DistanceY(g0) = -352
    c: DistanceY(g0,g0) = 100
FEATURE [Part::Loft] Loft011
  Closed = false
  MaxDegree = 5
  Ruled = false
  Sections = -> [Sketch030,Sketch031]
  Solid = true
FEATURE [Part::Fillet] Fillet019
  Base = -> Loft011
  Edges = 12 edges r=3: [Edge1,Edge2,Edge3,Edge4,Edge5,Edge6,Edge7,Edge8,Edge9,Edge10,Edge11,Edge12]
  Placement = pos=(0,0,-4) rot=(0,0,1;0rad)
FEATURE [Part::Cut] Cut008  label="sls006"
  Base = -> Fillet018
  Placement = pos=(0,0,7) rot=(0,0,1;0rad)
  Tool = -> Fillet019
FEATURE [Sketcher::SketchObject] Sketch033
  FullyConstrained = true
  Placement = pos=(0,0,0) rot=(1,0,0;1.5708rad)
  sketch-geometry (4):
    g0: LineSegment StartX=-22 StartY=-275.2 StartZ=0 EndX=22 EndY=-275.2 EndZ=0
    g1: LineSegment StartX=22 StartY=-275.2 StartZ=0 EndX=22 EndY=-323.5 EndZ=0
    g2: LineSegment StartX=22 StartY=-323.5 StartZ=0 EndX=-22 EndY=-323.5 EndZ=0
    g3: LineSegment StartX=-22 StartY=-323.5 StartZ=0 EndX=-22 EndY=-275.2 EndZ=0
  constraints (12):
    c: Coincident(g0,g1)
    c: Coincident(g1,g2)
    c: Coincident(g2,g3)
    c: Coincident(g3,g0)
    c: Horizontal(g0)
    c: Horizontal(g2)
    c: Vertical(g1)
    c: Vertical(g3)
    c: DistanceX(g1) = 22
    c: DistanceX(g0) = -22
    c: DistanceY(g0) = -275.2
    c: DistanceY(g2) = -323.5
FEATURE [Part::Extrusion] Extrude009  label="face"
  Base = -> Sketch033
  Dir = (0,-1,2e-16)
  DirMode = 2
  FaceMakerClass = Part::FaceMakerBullseye
  LengthFwd = 2
  LengthRev = 0
  Placement = pos=(0,-325.87,0) rot=(0,0,1;0rad)
  Solid = true
  Symmetric = false
FEATURE [Sketcher::SketchObject] Sketch034
  FullyConstrained = true
  sketch-geometry (4):
    g0: Circle CenterX=-35 CenterY=-332 CenterZ=0 NormalX=0 NormalY=0 NormalZ=1 AngleXU=0 Radius=2
    g1: Circle CenterX=35 CenterY=-332 CenterZ=0 NormalX=0 NormalY=0 NormalZ=1 AngleXU=0 Radius=2
    g2: Circle CenterX=35 CenterY=-272 CenterZ=0 NormalX=0 NormalY=0 NormalZ=1 AngleXU=0 Radius=2
    g3: Circle CenterX=-35 CenterY=-272 CenterZ=0 NormalX=0 NormalY=0 NormalZ=1 AngleXU=0 Radius=2
  constraints (12):
    c: DistanceX(g0) = -35
    c: DistanceY(g0) = -332
    c: Equal(g0,g3)
    c: Equal(g0,g2)
    c: Equal(g0,g1)
    c: Diameter(g0) = 4
    c: DistanceX(g3,g0) = 0
    c: DistanceY(g0,g3) = 60
    c: DistanceY(g2,g3) = 0
    c: DistanceY(g0,g1) = 0
    c: DistanceX(g2,g1) = 0
    c: DistanceX(g1) = 35
FEATURE [Part::Extrusion] Extrude010  label="slsCuts"
  Base = -> Sketch034
  Dir = (0,0,1)
  DirMode = 2
  FaceMakerClass = Part::FaceMakerBullseye
  LengthFwd = 20
  LengthRev = 0
  Placement = pos=(0,0,-323) rot=(0,0,1;0rad)
  Solid = true
  Symmetric = false
FEATURE [Sketcher::SketchObject] Sketch036
  FullyConstrained = true
  MapMode = 2
  sketch-geometry (4):
    g0: LineSegment StartX=-28 StartY=-347.85 StartZ=0 EndX=28 EndY=-347.85 EndZ=0
    g1: LineSegment StartX=18 StartY=-327.85 StartZ=0 EndX=28 EndY=-347.85 EndZ=0
    g2: LineSegment StartX=-28 StartY=-347.85 StartZ=0 EndX=-18 EndY=-327.85 EndZ=0
    g3: LineSegment StartX=-18 StartY=-327.85 StartZ=0 EndX=18 EndY=-327.85 EndZ=0
  constraints (12):
    c: Horizontal(g0)
    c: Coincident(g1,g0)
    c: Coincident(g2,g0)
    c: Coincident(g3,g2)
    c: Coincident(g3,g1)
    c: Horizontal(g3)
    c: DistanceX(g2) = -18
    c: DistanceX(g1) = 18
    c: DistanceX(g0,g2) = 10
    c: DistanceY(g2) = -327.85
    c: DistanceY(g0,g2) = 20
    c: DistanceX(g1,g0) = 10
FEATURE [Part::Extrusion] Extrude012
  Base = -> Sketch036
  Dir = (0,0,1)
  DirMode = 2
  FaceMakerClass = Part::FaceMakerBullseye
  LengthFwd = 40
  LengthRev = 0
  Placement = pos=(0,0,-329) rot=(0,0,1;0rad)
  Solid = true
  Symmetric = false
FEATURE [Part::Cut] Cut011  label="slsBottom001"
  Base = -> Fusion036
  Tool = -> Extrude012
FEATURE [Part::MultiFuse] Fusion037  label="sls"
  Shapes = -> [Cut011,Extrude009,Extrude007,Cut004,Cut]
FEATURE [Sketcher::SketchObject] Sketch037
  FullyConstrained = true
  sketch-geometry (4):
    g0: LineSegment StartX=-29 StartY=-278.2 StartZ=0 EndX=29 EndY=-278.2 EndZ=0
    g1: LineSegment StartX=29 StartY=-278.2 StartZ=0 EndX=29 EndY=-325.8 EndZ=0
    g2: LineSegment StartX=29 StartY=-325.8 StartZ=0 EndX=-29 EndY=-325.8 EndZ=0
    g3: LineSegment StartX=-29 StartY=-325.8 StartZ=0 EndX=-29 EndY=-278.2 EndZ=0
  constraints (12):
    c: Coincident(g0,g1)
    c: Coincident(g1,g2)
    c: Coincident(g2,g3)
    c: Coincident(g3,g0)
    c: Horizontal(g0)
    c: Horizontal(g2)
    c: Vertical(g1)
    c: Vertical(g3)
    c: DistanceX(g2) = -29
    c: DistanceY(g2) = -325.8
    c: DistanceY(g2,g0) = 47.6
    c: DistanceX(g1) = 29
FEATURE [Part::Extrusion] Extrude013  label="slsCut"
  Base = -> Sketch037
  Dir = (0,0,1)
  DirMode = 2
  FaceMakerClass = Part::FaceMakerBullseye
  LengthFwd = 60
  LengthRev = 0
  Placement = pos=(0,0,-329) rot=(0,0,1;0rad)
  Solid = true
  Symmetric = false
FEATURE [Part::Cut] Cut012  label="sls007"
  Base = -> Fusion037
  Tool = -> Extrude013
FEATURE [Sketcher::SketchObject] Sketch038  label="inner012"
  FullyConstrained = true
  Placement = pos=(0,0,-259.26) rot=(0,0,1;0rad)
  sketch-geometry (4):
    g0: LineSegment StartX=-30 StartY=-277 StartZ=0 EndX=-30 EndY=-327 EndZ=0
    g1: LineSegment StartX=-30 StartY=-327 StartZ=0 EndX=30 EndY=-327 EndZ=0
    g2: LineSegment StartX=30 StartY=-327 StartZ=0 EndX=30 EndY=-277 EndZ=0
    g3: LineSegment StartX=30 StartY=-277 StartZ=0 EndX=-30 EndY=-277 EndZ=0
  constraints (12):
    c: Vertical(g0)
    c: Coincident(g1,g0)
    c: Horizontal(g1)
    c: Coincident(g2,g1)
    c: Vertical(g2)
    c: Coincident(g3,g2)
    c: Coincident(g3,g0)
    c: Horizontal(g3)
    c: DistanceX(g0) = -30
    c: DistanceX(g1) = 30
    c: DistanceY(g0) = -327
    c: DistanceY(g0,g0) = 50
FEATURE [Sketcher::SketchObject] Sketch039  label="outer012"
  FullyConstrained = true
  Placement = pos=(0,0,-281.2) rot=(0,0,1;0rad)
  sketch-geometry (4):
    g0: LineSegment StartX=-59 StartY=-252 StartZ=0 EndX=-59 EndY=-352 EndZ=0
    g1: LineSegment StartX=-59 StartY=-352 StartZ=0 EndX=59 EndY=-352 EndZ=0
    g2: LineSegment StartX=59 StartY=-352 StartZ=0 EndX=59 EndY=-252 EndZ=0
    g3: LineSegment StartX=59 StartY=-252 StartZ=0 EndX=-59 EndY=-252 EndZ=0
  constraints (12):
    c: Vertical(g0)
    c: Coincident(g1,g0)
    c: Horizontal(g1)
    c: Coincident(g2,g1)
    c: Vertical(g2)
    c: Coincident(g3,g2)
    c: Coincident(g3,g0)
    c: Horizontal(g3)
    c: DistanceX(g0) = -59
    c: DistanceX(g1) = 59
    c: DistanceY(g0) = -352
    c: DistanceY(g0,g0) = 100
FEATURE [Part::Loft] Loft012
  Closed = false
  MaxDegree = 5
  Ruled = false
  Sections = -> [Sketch038,Sketch039]
  Solid = true
FEATURE [Part::Fillet] Fillet020
  Base = -> Loft012
  Edges = 12 edges r=3: [Edge1,Edge2,Edge3,Edge4,Edge5,Edge6,Edge7,Edge8,Edge9,Edge10,Edge11,Edge12]
FEATURE [Sketcher::SketchObject] Sketch040  label="inner013"
  FullyConstrained = true
  Placement = pos=(0,0,-259.26) rot=(0,0,1;0rad)
  sketch-geometry (4):
    g0: LineSegment StartX=-30 StartY=-277 StartZ=0 EndX=-30 EndY=-327 EndZ=0
    g1: LineSegment StartX=-30 StartY=-327 StartZ=0 EndX=30 EndY=-327 EndZ=0
    g2: LineSegment StartX=30 StartY=-327 StartZ=0 EndX=30 EndY=-277 EndZ=0
    g3: LineSegment StartX=30 StartY=-277 StartZ=0 EndX=-30 EndY=-277 EndZ=0
  constraints (12):
    c: Vertical(g0)
    c: Coincident(g1,g0)
    c: Horizontal(g1)
    c: Coincident(g2,g1)
    c: Vertical(g2)
    c: Coincident(g3,g2)
    c: Coincident(g3,g0)
    c: Horizontal(g3)
    c: DistanceX(g0) = -30
    c: DistanceX(g1) = 30
    c: DistanceY(g0) = -327
    c: DistanceY(g0,g0) = 50
FEATURE [Sketcher::SketchObject] Sketch041  label="outer013"
  FullyConstrained = true
  Placement = pos=(0,0,-281.2) rot=(0,0,1;0rad)
  sketch-geometry (4):
    g0: LineSegment StartX=-59 StartY=-252 StartZ=0 EndX=-59 EndY=-352 EndZ=0
    g1: LineSegment StartX=-59 StartY=-352 StartZ=0 EndX=59 EndY=-352 EndZ=0
    g2: LineSegment StartX=59 StartY=-352 StartZ=0 EndX=59 EndY=-252 EndZ=0
    g3: LineSegment StartX=59 StartY=-252 StartZ=0 EndX=-59 EndY=-252 EndZ=0
  constraints (12):
    c: Vertical(g0)
    c: Coincident(g1,g0)
    c: Horizontal(g1)
    c: Coincident(g2,g1)
    c: Vertical(g2)
    c: Coincident(g3,g2)
    c: Coincident(g3,g0)
    c: Horizontal(g3)
    c: DistanceX(g0) = -59
    c: DistanceX(g1) = 59
    c: DistanceY(g0) = -352
    c: DistanceY(g0,g0) = 100
FEATURE [Part::Loft] Loft013
  Closed = false
  MaxDegree = 5
  Ruled = false
  Sections = -> [Sketch040,Sketch041]
  Solid = true
FEATURE [Part::Fillet] Fillet021
  Base = -> Loft013
  Edges = 12 edges r=3: [Edge1,Edge2,Edge3,Edge4,Edge5,Edge6,Edge7,Edge8,Edge9,Edge10,Edge11,Edge12]
  Placement = pos=(0,0,-4) rot=(0,0,1;0rad)
FEATURE [Part::Cut] Cut013  label="sls008"
  Base = -> Fillet020
  Placement = pos=(0,0,10) rot=(0,0,1;0rad)
  Tool = -> Fillet021
FEATURE [Part::MultiFuse] Fusion039
  Shapes = -> [Cut013,Cut008,Cut007]
FEATURE [Sketcher::SketchObject] Sketch042  label="inner014"
  FullyConstrained = true
  Placement = pos=(0,0,-259.26) rot=(0,0,1;0rad)
  sketch-geometry (4):
    g0: LineSegment StartX=-30 StartY=-277 StartZ=0 EndX=-30 EndY=-327 EndZ=0
    g1: LineSegment StartX=-30 StartY=-327 StartZ=0 EndX=30 EndY=-327 EndZ=0
    g2: LineSegment StartX=30 StartY=-327 StartZ=0 EndX=30 EndY=-277 EndZ=0
    g3: LineSegment StartX=30 StartY=-277 StartZ=0 EndX=-30 EndY=-277 EndZ=0
  constraints (12):
    c: Vertical(g0)
    c: Coincident(g1,g0)
    c: Horizontal(g1)
    c: Coincident(g2,g1)
    c: Vertical(g2)
    c: Coincident(g3,g2)
    c: Coincident(g3,g0)
    c: Horizontal(g3)
    c: DistanceX(g0) = -30
    c: DistanceX(g1) = 30
    c: DistanceY(g0) = -327
    c: DistanceY(g0,g0) = 50
FEATURE [Sketcher::SketchObject] Sketch043  label="outer014"
  FullyConstrained = true
  Placement = pos=(0,0,-281.2) rot=(0,0,1;0rad)
  sketch-geometry (4):
    g0: LineSegment StartX=-59 StartY=-252 StartZ=0 EndX=-59 EndY=-352 EndZ=0
    g1: LineSegment StartX=-59 StartY=-352 StartZ=0 EndX=59 EndY=-352 EndZ=0
    g2: LineSegment StartX=59 StartY=-352 StartZ=0 EndX=59 EndY=-252 EndZ=0
    g3: LineSegment StartX=59 StartY=-252 StartZ=0 EndX=-59 EndY=-252 EndZ=0
  constraints (12):
    c: Vertical(g0)
    c: Coincident(g1,g0)
    c: Horizontal(g1)
    c: Coincident(g2,g1)
    c: Vertical(g2)
    c: Coincident(g3,g2)
    c: Coincident(g3,g0)
    c: Horizontal(g3)
    c: DistanceX(g0) = -59
    c: DistanceX(g1) = 59
    c: DistanceY(g0) = -352
    c: DistanceY(g0,g0) = 100
FEATURE [Part::Loft] Loft014
  Closed = false
  MaxDegree = 5
  Ruled = false
  Sections = -> [Sketch042,Sketch043]
  Solid = true
FEATURE [Part::Fillet] Fillet022
  Base = -> Loft014
  Edges = 12 edges r=3: [Edge1,Edge2,Edge3,Edge4,Edge5,Edge6,Edge7,Edge8,Edge9,Edge10,Edge11,Edge12]
FEATURE [Sketcher::SketchObject] Sketch044  label="inner015"
  FullyConstrained = true
  Placement = pos=(0,0,-259.26) rot=(0,0,1;0rad)
  sketch-geometry (4):
    g0: LineSegment StartX=-36 StartY=-277 StartZ=0 EndX=-36 EndY=-327 EndZ=0
    g1: LineSegment StartX=-36 StartY=-327 StartZ=0 EndX=36 EndY=-327 EndZ=0
    g2: LineSegment StartX=36 StartY=-327 StartZ=0 EndX=36 EndY=-277 EndZ=0
    g3: LineSegment StartX=36 StartY=-277 StartZ=0 EndX=-36 EndY=-277 EndZ=0
  constraints (12):
    c: Vertical(g0)
    c: Coincident(g1,g0)
    c: Horizontal(g1)
    c: Coincident(g2,g1)
    c: Vertical(g2)
    c: Coincident(g3,g2)
    c: Coincident(g3,g0)
    c: Horizontal(g3)
    c: DistanceX(g0) = -36
    c: DistanceX(g1) = 36
    c: DistanceY(g0) = -327
    c: DistanceY(g0,g0) = 50
FEATURE [Sketcher::SketchObject] Sketch045  label="outer015"
  FullyConstrained = true
  Placement = pos=(0,0,-281.2) rot=(0,0,1;0rad)
  sketch-geometry (4):
    g0: LineSegment StartX=-65 StartY=-252 StartZ=0 EndX=-65 EndY=-352 EndZ=0
    g1: LineSegment StartX=-65 StartY=-352 StartZ=0 EndX=65 EndY=-352 EndZ=0
    g2: LineSegment StartX=65 StartY=-352 StartZ=0 EndX=65 EndY=-252 EndZ=0
    g3: LineSegment StartX=65 StartY=-252 StartZ=0 EndX=-65 EndY=-252 EndZ=0
  constraints (12):
    c: Vertical(g0)
    c: Coincident(g1,g0)
    c: Horizontal(g1)
    c: Coincident(g2,g1)
    c: Vertical(g2)
    c: Coincident(g3,g2)
    c: Coincident(g3,g0)
    c: Horizontal(g3)
    c: DistanceX(g0) = -65
    c: DistanceX(g1) = 65
    c: DistanceY(g0) = -352
    c: DistanceY(g0,g0) = 100
FEATURE [Part::Loft] Loft015
  Closed = false
  MaxDegree = 5
  Ruled = false
  Sections = -> [Sketch044,Sketch045]
  Solid = true
FEATURE [Part::Fillet] Fillet023
  Base = -> Loft015
  Edges = 12 edges r=3: [Edge1,Edge2,Edge3,Edge4,Edge5,Edge6,Edge7,Edge8,Edge9,Edge10,Edge11,Edge12]
  Placement = pos=(0,0,-4) rot=(0,0,1;0rad)
FEATURE [Part::Cut] Cut014  label="sls009"
  Base = -> Fillet022
  Placement = pos=(0,0,4) rot=(0,0,1;0rad)
  Tool = -> Fillet023
FEATURE [Sketcher::SketchObject] Sketch046  label="inner016"
  FullyConstrained = true
  Placement = pos=(0,0,-259.26) rot=(0,0,1;0rad)
  sketch-geometry (4):
    g0: LineSegment StartX=-30 StartY=-277 StartZ=0 EndX=-30 EndY=-327 EndZ=0
    g1: LineSegment StartX=-30 StartY=-327 StartZ=0 EndX=30 EndY=-327 EndZ=0
    g2: LineSegment StartX=30 StartY=-327 StartZ=0 EndX=30 EndY=-277 EndZ=0
    g3: LineSegment StartX=30 StartY=-277 StartZ=0 EndX=-30 EndY=-277 EndZ=0
  constraints (12):
    c: Vertical(g0)
    c: Coincident(g1,g0)
    c: Horizontal(g1)
    c: Coincident(g2,g1)
    c: Vertical(g2)
    c: Coincident(g3,g2)
    c: Coincident(g3,g0)
    c: Horizontal(g3)
    c: DistanceX(g0) = -30
    c: DistanceX(g1) = 30
    c: DistanceY(g0) = -327
    c: DistanceY(g0,g0) = 50
FEATURE [Sketcher::SketchObject] Sketch047  label="outer016"
  FullyConstrained = true
  Placement = pos=(0,0,-281.2) rot=(0,0,1;0rad)
  sketch-geometry (4):
    g0: LineSegment StartX=-59 StartY=-252 StartZ=0 EndX=-59 EndY=-352 EndZ=0
    g1: LineSegment StartX=-59 StartY=-352 StartZ=0 EndX=59 EndY=-352 EndZ=0
    g2: LineSegment StartX=59 StartY=-352 StartZ=0 EndX=59 EndY=-252 EndZ=0
    g3: LineSegment StartX=59 StartY=-252 StartZ=0 EndX=-59 EndY=-252 EndZ=0
  constraints (12):
    c: Vertical(g0)
    c: Coincident(g1,g0)
    c: Horizontal(g1)
    c: Coincident(g2,g1)
    c: Vertical(g2)
    c: Coincident(g3,g2)
    c: Coincident(g3,g0)
    c: Horizontal(g3)
    c: DistanceX(g0) = -59
    c: DistanceX(g1) = 59
    c: DistanceY(g0) = -352
    c: DistanceY(g0,g0) = 100
FEATURE [Part::Loft] Loft016
  Closed = false
  MaxDegree = 5
  Ruled = false
  Sections = -> [Sketch046,Sketch047]
  Solid = true
FEATURE [Part::Fillet] Fillet024
  Base = -> Loft016
  Edges = 12 edges r=3: [Edge1,Edge2,Edge3,Edge4,Edge5,Edge6,Edge7,Edge8,Edge9,Edge10,Edge11,Edge12]
FEATURE [Sketcher::SketchObject] Sketch048  label="inner017"
  FullyConstrained = true
  Placement = pos=(0,0,-259.26) rot=(0,0,1;0rad)
  sketch-geometry (4):
    g0: LineSegment StartX=-30 StartY=-277 StartZ=0 EndX=-30 EndY=-327 EndZ=0
    g1: LineSegment StartX=-30 StartY=-327 StartZ=0 EndX=30 EndY=-327 EndZ=0
    g2: LineSegment StartX=30 StartY=-327 StartZ=0 EndX=30 EndY=-277 EndZ=0
    g3: LineSegment StartX=30 StartY=-277 StartZ=0 EndX=-30 EndY=-277 EndZ=0
  constraints (12):
    c: Vertical(g0)
    c: Coincident(g1,g0)
    c: Horizontal(g1)
    c: Coincident(g2,g1)
    c: Vertical(g2)
    c: Coincident(g3,g2)
    c: Coincident(g3,g0)
    c: Horizontal(g3)
    c: DistanceX(g0) = -30
    c: DistanceX(g1) = 30
    c: DistanceY(g0) = -327
    c: DistanceY(g0,g0) = 50
FEATURE [Sketcher::SketchObject] Sketch049  label="outer017"
  FullyConstrained = true
  Placement = pos=(0,0,-281.2) rot=(0,0,1;0rad)
  sketch-geometry (4):
    g0: LineSegment StartX=-65 StartY=-252 StartZ=0 EndX=-65 EndY=-352 EndZ=0
    g1: LineSegment StartX=-65 StartY=-352 StartZ=0 EndX=65 EndY=-352 EndZ=0
    g2: LineSegment StartX=65 StartY=-352 StartZ=0 EndX=65 EndY=-252 EndZ=0
    g3: LineSegment StartX=65 StartY=-252 StartZ=0 EndX=-65 EndY=-252 EndZ=0
  constraints (12):
    c: Vertical(g0)
    c: Coincident(g1,g0)
    c: Horizontal(g1)
    c: Coincident(g2,g1)
    c: Vertical(g2)
    c: Coincident(g3,g2)
    c: Coincident(g3,g0)
    c: Horizontal(g3)
    c: DistanceX(g0) = -65
    c: DistanceX(g1) = 65
    c: DistanceY(g0) = -352
    c: DistanceY(g0,g0) = 100
FEATURE [Part::Loft] Loft017
  Closed = false
  MaxDegree = 5
  Ruled = false
  Sections = -> [Sketch048,Sketch049]
  Solid = true
FEATURE [Part::Fillet] Fillet025
  Base = -> Loft017
  Edges = 12 edges r=3: [Edge1,Edge2,Edge3,Edge4,Edge5,Edge6,Edge7,Edge8,Edge9,Edge10,Edge11,Edge12]
  Placement = pos=(0,0,-4) rot=(0,0,1;0rad)
FEATURE [Part::Cut] Cut015  label="sls010"
  Base = -> Fillet024
  Placement = pos=(0,0,7) rot=(0,0,1;0rad)
  Tool = -> Fillet025
FEATURE [Sketcher::SketchObject] Sketch050  label="inner018"
  FullyConstrained = true
  Placement = pos=(0,0,-259.26) rot=(0,0,1;0rad)
  sketch-geometry (4):
    g0: LineSegment StartX=-30 StartY=-277 StartZ=0 EndX=-30 EndY=-327 EndZ=0
    g1: LineSegment StartX=-30 StartY=-327 StartZ=0 EndX=30 EndY=-327 EndZ=0
    g2: LineSegment StartX=30 StartY=-327 StartZ=0 EndX=30 EndY=-277 EndZ=0
    g3: LineSegment StartX=30 StartY=-277 StartZ=0 EndX=-30 EndY=-277 EndZ=0
  constraints (12):
    c: Vertical(g0)
    c: Coincident(g1,g0)
    c: Horizontal(g1)
    c: Coincident(g2,g1)
    c: Vertical(g2)
    c: Coincident(g3,g2)
    c: Coincident(g3,g0)
    c: Horizontal(g3)
    c: DistanceX(g0) = -30
    c: DistanceX(g1) = 30
    c: DistanceY(g0) = -327
    c: DistanceY(g0,g0) = 50
FEATURE [Sketcher::SketchObject] Sketch051  label="outer018"
  FullyConstrained = true
  Placement = pos=(0,0,-281.2) rot=(0,0,1;0rad)
  sketch-geometry (4):
    g0: LineSegment StartX=-59 StartY=-252 StartZ=0 EndX=-59 EndY=-352 EndZ=0
    g1: LineSegment StartX=-59 StartY=-352 StartZ=0 EndX=59 EndY=-352 EndZ=0
    g2: LineSegment StartX=59 StartY=-352 StartZ=0 EndX=59 EndY=-252 EndZ=0
    g3: LineSegment StartX=59 StartY=-252 StartZ=0 EndX=-59 EndY=-252 EndZ=0
  constraints (12):
    c: Vertical(g0)
    c: Coincident(g1,g0)
    c: Horizontal(g1)
    c: Coincident(g2,g1)
    c: Vertical(g2)
    c: Coincident(g3,g2)
    c: Coincident(g3,g0)
    c: Horizontal(g3)
    c: DistanceX(g0) = -59
    c: DistanceX(g1) = 59
    c: DistanceY(g0) = -352
    c: DistanceY(g0,g0) = 100
FEATURE [Part::Loft] Loft018
  Closed = false
  MaxDegree = 5
  Ruled = false
  Sections = -> [Sketch050,Sketch051]
  Solid = true
FEATURE [Part::Fillet] Fillet026
  Base = -> Loft018
  Edges = 12 edges r=3: [Edge1,Edge2,Edge3,Edge4,Edge5,Edge6,Edge7,Edge8,Edge9,Edge10,Edge11,Edge12]
FEATURE [Sketcher::SketchObject] Sketch052  label="inner019"
  FullyConstrained = true
  Placement = pos=(0,0,-259.26) rot=(0,0,1;0rad)
  sketch-geometry (4):
    g0: LineSegment StartX=-30 StartY=-277 StartZ=0 EndX=-30 EndY=-327 EndZ=0
    g1: LineSegment StartX=-30 StartY=-327 StartZ=0 EndX=30 EndY=-327 EndZ=0
    g2: LineSegment StartX=30 StartY=-327 StartZ=0 EndX=30 EndY=-277 EndZ=0
    g3: LineSegment StartX=30 StartY=-277 StartZ=0 EndX=-30 EndY=-277 EndZ=0
  constraints (12):
    c: Vertical(g0)
    c: Coincident(g1,g0)
    c: Horizontal(g1)
    c: Coincident(g2,g1)
    c: Vertical(g2)
    c: Coincident(g3,g2)
    c: Coincident(g3,g0)
    c: Horizontal(g3)
    c: DistanceX(g0) = -30
    c: DistanceX(g1) = 30
    c: DistanceY(g0) = -327
    c: DistanceY(g0,g0) = 50
FEATURE [Sketcher::SketchObject] Sketch053  label="outer019"
  FullyConstrained = true
  Placement = pos=(0,0,-281.2) rot=(0,0,1;0rad)
  sketch-geometry (4):
    g0: LineSegment StartX=-59 StartY=-252 StartZ=0 EndX=-59 EndY=-352 EndZ=0
    g1: LineSegment StartX=-59 StartY=-352 StartZ=0 EndX=59 EndY=-352 EndZ=0
    g2: LineSegment StartX=59 StartY=-352 StartZ=0 EndX=59 EndY=-252 EndZ=0
    g3: LineSegment StartX=59 StartY=-252 StartZ=0 EndX=-59 EndY=-252 EndZ=0
  constraints (12):
    c: Vertical(g0)
    c: Coincident(g1,g0)
    c: Horizontal(g1)
    c: Coincident(g2,g1)
    c: Vertical(g2)
    c: Coincident(g3,g2)
    c: Coincident(g3,g0)
    c: Horizontal(g3)
    c: DistanceX(g0) = -59
    c: DistanceX(g1) = 59
    c: DistanceY(g0) = -352
    c: DistanceY(g0,g0) = 100
FEATURE [Part::Loft] Loft019
  Closed = false
  MaxDegree = 5
  Ruled = false
  Sections = -> [Sketch052,Sketch053]
  Solid = true
FEATURE [Part::Fillet] Fillet027
  Base = -> Loft019
  Edges = 12 edges r=3: [Edge1,Edge2,Edge3,Edge4,Edge5,Edge6,Edge7,Edge8,Edge9,Edge10,Edge11,Edge12]
  Placement = pos=(0,0,-4) rot=(0,0,1;0rad)
FEATURE [Part::Cut] Cut016  label="sls011"
  Base = -> Fillet026
  Placement = pos=(0,0,10) rot=(0,0,1;0rad)
  Tool = -> Fillet027
FEATURE [Part::MultiFuse] Fusion040
  Placement = pos=(0,0,5) rot=(0,0,1;0rad)
  Shapes = -> [Cut016,Cut015,Cut014]
FEATURE [Part::MultiFuse] Fusion041  label="slsCUts"
  Shapes = -> [Fusion040,Fusion039]
FEATURE [Part::MultiFuse] Fusion042  label="slsCuts001"
  Shapes = -> [Fusion041,Extrude010]
FEATURE [Part::Cut] Cut017  label="sls012"
  Base = -> Cut012
  Tool = -> Fusion042
FEATURE [Part::Cut] Cut018  label="sls013"
  Base = -> Cut017
  Placement = pos=(0,17,15) rot=(0,0,1;0rad)
  Tool = -> Part__Feature153
FEATURE [Sketcher::SketchObject] Sketch054
  FullyConstrained = true
  MapMode = 2
  Placement = pos=(-0.5,-512,-305.5) rot=(0.57735,-0.57735,-0.57735;2.0944rad)
  sketch-geometry (8):
    g0: LineSegment StartX=-225.068 StartY=76.4427 StartZ=0 EndX=-228.265 EndY=72.5985 EndZ=0
    g1: LineSegment StartX=-228.265 StartY=72.5985 StartZ=0 EndX=-209.044 EndY=56.6125 EndZ=0
    g2: LineSegment StartX=-185 StartY=46.25 StartZ=0 EndX=-212.066 EndY=69.9864 EndZ=0
    g3: LineSegment StartX=-214.208 StartY=67.4108 StartZ=0 EndX=-212.066 EndY=69.9864 EndZ=0
    g4: LineSegment StartX=-214.208 StartY=67.4108 StartZ=0 EndX=-225.068 EndY=76.4427 EndZ=0
    g5: LineSegment StartX=-185 StartY=46.25 StartZ=0 EndX=-185 EndY=40.7882 EndZ=0
    g6: LineSegment StartX=-185 StartY=40.7882 StartZ=0 EndX=-203.044 EndY=56.6125 EndZ=0
    g7: LineSegment StartX=-203.044 StartY=56.6125 StartZ=0 EndX=-209.044 EndY=56.6125 EndZ=0
  constraints (24):
    c: Coincident(g0,g1)
    c: Coincident(g2,g3)
    c: Coincident(g4,g3)
    c: Coincident(g4,g0)
    c: Coincident(g5,g2)
    c: Coincident(g6,g5)
    c: Coincident(g7,g6)
    c: Horizontal(g7)
    c: Coincident(g1,g7)
    c: Parallel(g2,g6)
    c: Angle(g3,g2) = 1.54462
    c: Angle(g0,g4) = 1.5708
    c: Angle(g3,g4) = 1.5708
    c: DistanceX(g2) = -185
    c: DistanceY(g2) = 46.25
    c: Vertical(g5)
    c: Angle(g2,g5) = 2.29074
    c: Distance(g2) = 36
    c: Distance(g3) = 3.35
    c: Distance(g0) = 5
    c: Parallel(g4,g1)
    c: DistanceX(g7,g7) = 6
    c: Distance(g1) = 25
    c: Distance(g6) = 24
FEATURE [Part::Extrusion] Extrude014
  Base = -> Sketch054
  Dir = (-1,0,0)
  DirMode = 2
  FaceMakerClass = Part::FaceMakerBullseye
  LengthFwd = 61.6
  LengthRev = 0
  Placement = pos=(31.3,0,0) rot=(0,0,1;0rad)
  Solid = true
  Symmetric = false
FEATURE [Part::Cut] Cut020
  Base = -> Extrude014
  Tool = -> Cylinder
FEATURE [Part::MultiFuse] Fusion043  label="sls014"
  Shapes = -> [Cut020,Cut018]
FEATURE [Sketcher::SketchObject] Sketch095
  FullyConstrained = true
  sketch-geometry (4):
    g0: LineSegment StartX=-29.4 StartY=-303 StartZ=0 EndX=29.4 EndY=-303 EndZ=0
    g1: LineSegment StartX=29.4 StartY=-303 StartZ=0 EndX=39.5 EndY=-345 EndZ=0
    g2: LineSegment StartX=39.5 StartY=-345 StartZ=0 EndX=-39.5 EndY=-345 EndZ=0
    g3: LineSegment StartX=-39.5 StartY=-345 StartZ=0 EndX=-29.4 EndY=-303 EndZ=0
  constraints (12):
    c: Horizontal(g0)
    c: Coincident(g1,g0)
    c: Coincident(g2,g1)
    c: Horizontal(g2)
    c: Coincident(g3,g2)
    c: Coincident(g3,g0)
    c: DistanceX(g2) = -39.5
    c: DistanceY(g2) = -345
    c: DistanceX(g0) = -29.4
    c: DistanceX(g0) = 29.4
    c: DistanceX(g1) = 39.5
    c: DistanceY(g1,g0) = 42
FEATURE [Part::Extrusion] Extrude032  label="slsIn"
  Base = -> Sketch095
  Dir = (0,0,1)
  DirMode = 2
  FaceMakerClass = Part::FaceMakerBullseye
  LengthFwd = 4.5
  LengthRev = 0
  Placement = pos=(0,0,-249) rot=(0,0,1;0rad)
  Solid = true
  Symmetric = false
FEATURE [Sketcher::SketchObject] Sketch096
  FullyConstrained = true
  Placement = pos=(0,0,0) rot=(0.57735,0.57735,0.57735;2.0944rad)
  sketch-geometry (4):
    g0: LineSegment StartX=-358.25 StartY=-249 StartZ=0 EndX=-353.25 EndY=-249 EndZ=0
    g1: LineSegment StartX=-353.25 StartY=-249 StartZ=0 EndX=-326.489 EndY=-278.721 EndZ=0
    g2: LineSegment StartX=-326.489 StartY=-278.721 StartZ=0 EndX=-329.25 EndY=-281.208 EndZ=0
    g3: LineSegment StartX=-329.25 StartY=-281.208 StartZ=0 EndX=-358.25 EndY=-249 EndZ=0
  constraints (12):
    c: Coincident(g1,g0)
    c: Coincident(g0,g3)
    c: Horizontal(g0)
    c: DistanceX(g0,g0) = 5
    c: DistanceY(g0) = -249
    c: Coincident(g1,g2)
    c: Parallel(g3,g1)
    c: Coincident(g3,g2)
    c: Angle(g2,g3) = 1.5708
    c: Angle(g2) = -2.40855
    c: DistanceX(g3,g3) = 29
    c: DistanceX(g2) = -329.25
FEATURE [Part::Extrusion] Extrude033  label="slsIn001"
  Base = -> Sketch096
  Dir = (1,0,0)
  DirMode = 2
  FaceMakerClass = Part::FaceMakerBullseye
  LengthFwd = 20
  LengthRev = 0
  Placement = pos=(-10,0,0) rot=(0,0,1;0rad)
  Solid = true
  Symmetric = false
FEATURE [Part::MultiFuse] Fusion090
  Shapes = -> [Fusion043,Extrude032,Extrude033,Cut039]
FEATURE [Part::Sphere] Sphere004  label="SphereBase002"
  Angle1 = 0
  Angle2 = 12
  Angle3 = 360
  AttacherType = Attacher::AttachEngine3D
  Placement = pos=(5,0,74) rot=(0,0,1;0rad)
  Radius = 27.5
FEATURE [Part::Cut] Cut036
  Base = -> Sphere004
  Placement = pos=(131,0,-5) rot=(0,0,1;0rad)
  Tool = -> Cylinder129
FEATURE [Part::MultiFuse] Fusion082  label="Base002"
  Placement = pos=(-2,10,0) rot=(0,0,1;0rad)
  Shapes = -> [Cut036,Cylinder128]
FEATURE [Part::MultiFuse] Fusion083  label="lightModule008"
  Shapes = -> [Fusion082,Cylinder130,Fusion081]
FEATURE [Part::Cut] Cut037  label="lightModule007"
  Base = -> Fusion083
  Placement = pos=(-134,-360,-314) rot=(0,0,1;0rad)
  Tool = -> Fusion088
FEATURE [Part::MultiFuse] Fusion091  label="sls015"
  Shapes = -> [Fusion090,Cut037]
FEATURE [Part::Cut] Cut040  label="sls016"
  Base = -> Fusion091
  Tool = -> Cylinder147
FEATURE [Part::Cut] Cut041
  Base = -> Cut040
  Tool = -> Fusion092
FEATURE [Sketcher::SketchObject] Sketch100  label="SketchTop002"
  FullyConstrained = true
  sketch-geometry (6):
    g0: LineSegment StartX=50 StartY=-368.819 StartZ=0 EndX=80.9017 EndY=-273.713 EndZ=0
    g1: LineSegment StartX=80.9017 StartY=-273.713 StartZ=0 EndX=0 EndY=-214.935 EndZ=0
    g2: LineSegment StartX=0 StartY=-214.935 StartZ=0 EndX=-80.9017 EndY=-273.713 EndZ=0
    g3: LineSegment StartX=-80.9017 StartY=-273.713 StartZ=0 EndX=-50 EndY=-368.819 EndZ=0
    g4: LineSegment StartX=-50 StartY=-368.819 StartZ=0 EndX=50 EndY=-368.819 EndZ=0
    g5: Circle CenterX=0 CenterY=-300 CenterZ=0 NormalX=0 NormalY=0 NormalZ=1 AngleXU=0 Radius=85.0651
  constraints (15):
    c: Coincident(g0,g1)
    c: Coincident(g1,g2)
    c: Coincident(g2,g3)
    c: Coincident(g3,g4)
    c: Coincident(g4,g0)
    c: Equal(g0, g1-g4) x4
    c: PointOnObject(g0,g5)
    c: PointOnObject(g1,g5)
    c: PointOnObject(g2,g5)
    c: PointOnObject(g3,g5)
    c: PointOnObject(g4,g5)
    c: Horizontal(g4)
    c: DistanceX(g4,g4) = 100
    c: DistanceY(g5) = -300
    c: DistanceX(g5) = 0
FEATURE [Sketcher::SketchObject] Sketch101  label="SketchBottom002"
  FullyConstrained = true
  Placement = pos=(0,0,20) rot=(0,0,1;0rad)
  sketch-geometry (6):
    g0: LineSegment StartX=37.5 StartY=-351.614 StartZ=0 EndX=60.6763 EndY=-280.285 EndZ=0
    g1: LineSegment StartX=60.6763 StartY=-280.285 StartZ=0 EndX=0 EndY=-236.201 EndZ=0
    g2: LineSegment StartX=0 StartY=-236.201 StartZ=0 EndX=-60.6763 EndY=-280.285 EndZ=0
    g3: LineSegment StartX=-60.6763 StartY=-280.285 StartZ=0 EndX=-37.5 EndY=-351.614 EndZ=0
    g4: LineSegment StartX=-37.5 StartY=-351.614 StartZ=0 EndX=37.5 EndY=-351.614 EndZ=0
    g5: Circle CenterX=0 CenterY=-300 CenterZ=0 NormalX=0 NormalY=0 NormalZ=1 AngleXU=0 Radius=63.7988
  constraints (15):
    c: Coincident(g0,g1)
    c: Coincident(g1,g2)
    c: Coincident(g2,g3)
    c: Coincident(g3,g4)
    c: Coincident(g4,g0)
    c: Equal(g0, g1-g4) x4
    c: PointOnObject(g0,g5)
    c: PointOnObject(g1,g5)
    c: PointOnObject(g2,g5)
    c: PointOnObject(g3,g5)
    c: PointOnObject(g4,g5)
    c: Horizontal(g4)
    c: DistanceX(g4,g4) = 75
    c: DistanceX(g5) = 0
    c: DistanceY(g5) = -300
FEATURE [Part::Loft] Loft022
  Closed = false
  MaxDegree = 5
  Ruled = false
  Sections = -> [Sketch100,Sketch101]
  Solid = true
FEATURE [Sketcher::SketchObject] Sketch102  label="SketchTop003"
  FullyConstrained = true
  sketch-geometry (6):
    g0: LineSegment StartX=47.5 StartY=-365.378 StartZ=0 EndX=76.8566 EndY=-275.028 EndZ=0
    g1: LineSegment StartX=76.8566 StartY=-275.028 StartZ=0 EndX=1.9185e-12 EndY=-219.188 EndZ=0
    g2: LineSegment StartX=1.9185e-12 StartY=-219.188 StartZ=0 EndX=-76.8566 EndY=-275.028 EndZ=0
    g3: LineSegment StartX=-76.8566 StartY=-275.028 StartZ=0 EndX=-47.5 EndY=-365.378 EndZ=0
    g4: LineSegment StartX=-47.5 StartY=-365.378 StartZ=0 EndX=47.5 EndY=-365.378 EndZ=0
    g5: Circle CenterX=0 CenterY=-300 CenterZ=0 NormalX=0 NormalY=0 NormalZ=1 AngleXU=0 Radius=80.8118
  constraints (15):
    c: Coincident(g0,g1)
    c: Coincident(g1,g2)
    c: Coincident(g2,g3)
    c: Coincident(g3,g4)
    c: Coincident(g4,g0)
    c: Equal(g0, g1-g4) x4
    c: PointOnObject(g0,g5)
    c: PointOnObject(g1,g5)
    c: PointOnObject(g2,g5)
    c: PointOnObject(g3,g5)
    c: PointOnObject(g4,g5)
    c: Horizontal(g4)
    c: DistanceX(g4,g4) = 95
    c: DistanceY(g5) = -300
    c: DistanceX(g5) = 0
FEATURE [Sketcher::SketchObject] Sketch103  label="SketchBottom003"
  FullyConstrained = true
  Placement = pos=(0,0,20) rot=(0,0,1;0rad)
  sketch-geometry (6):
    g0: LineSegment StartX=35 StartY=-348.173 StartZ=0 EndX=56.6312 EndY=-281.599 EndZ=0
    g1: LineSegment StartX=56.6312 StartY=-281.599 StartZ=0 EndX=0 EndY=-240.454 EndZ=0
    g2: LineSegment StartX=0 StartY=-240.454 StartZ=0 EndX=-56.6312 EndY=-281.599 EndZ=0
    g3: LineSegment StartX=-56.6312 StartY=-281.599 StartZ=0 EndX=-35 EndY=-348.173 EndZ=0
    g4: LineSegment StartX=-35 StartY=-348.173 StartZ=0 EndX=35 EndY=-348.173 EndZ=0
    g5: Circle CenterX=0 CenterY=-300 CenterZ=0 NormalX=0 NormalY=0 NormalZ=1 AngleXU=0 Radius=59.5456
  constraints (15):
    c: Coincident(g0,g1)
    c: Coincident(g1,g2)
    c: Coincident(g2,g3)
    c: Coincident(g3,g4)
    c: Coincident(g4,g0)
    c: Equal(g0, g1-g4) x4
    c: PointOnObject(g0,g5)
    c: PointOnObject(g1,g5)
    c: PointOnObject(g2,g5)
    c: PointOnObject(g3,g5)
    c: PointOnObject(g4,g5)
    c: Horizontal(g4)
    c: DistanceX(g4,g4) = 70
    c: DistanceX(g5) = 0
    c: DistanceY(g5) = -300
FEATURE [Part::Loft] Loft023
  Closed = false
  MaxDegree = 5
  Ruled = false
  Sections = -> [Sketch102,Sketch103]
  Solid = true
FEATURE [Part::Cut] Cut044  label="srsCone001"
  Base = -> Loft022
  Placement = pos=(0,0,-36) rot=(0,0,1;0rad)
  Tool = -> Loft023
FEATURE [Part::Fillet] Fillet031
  Base = -> Cut044
  Edges = 5 edges r=1.5: [Edge3,Edge15,Edge16,Edge17,Edge18]
FEATURE [Part::Fillet] Fillet032
  Base = -> Fillet031
  Edges = 5 edges r=1.5: [Edge4,Edge7,Edge11,Edge12,Edge13]
FEATURE [Part::Fillet] Fillet033
  Base = -> Fillet032
  Edges = 5 edges r=2: [Edge1,Edge3,Edge5,Edge15,Edge17]
FEATURE [Part::Fillet] Fillet034  label="srsCone"
  Base = -> Fillet033
  Edges = 5 edges r=1.5: [Edge63,Edge64,Edge65,Edge66,Edge67]
FEATURE [Sketcher::SketchObject] Sketch104  label="SketchTop004"
  FullyConstrained = true
  sketch-geometry (6):
    g0: LineSegment StartX=50 StartY=-368.819 StartZ=0 EndX=80.9017 EndY=-273.713 EndZ=0
    g1: LineSegment StartX=80.9017 StartY=-273.713 StartZ=0 EndX=0 EndY=-214.935 EndZ=0
    g2: LineSegment StartX=0 StartY=-214.935 StartZ=0 EndX=-80.9017 EndY=-273.713 EndZ=0
    g3: LineSegment StartX=-80.9017 StartY=-273.713 StartZ=0 EndX=-50 EndY=-368.819 EndZ=0
    g4: LineSegment StartX=-50 StartY=-368.819 StartZ=0 EndX=50 EndY=-368.819 EndZ=0
    g5: Circle CenterX=0 CenterY=-300 CenterZ=0 NormalX=0 NormalY=0 NormalZ=1 AngleXU=0 Radius=85.0651
  constraints (15):
    c: Coincident(g0,g1)
    c: Coincident(g1,g2)
    c: Coincident(g2,g3)
    c: Coincident(g3,g4)
    c: Coincident(g4,g0)
    c: Equal(g0, g1-g4) x4
    c: PointOnObject(g0,g5)
    c: PointOnObject(g1,g5)
    c: PointOnObject(g2,g5)
    c: PointOnObject(g3,g5)
    c: PointOnObject(g4,g5)
    c: Horizontal(g4)
    c: DistanceX(g4,g4) = 100
    c: DistanceY(g5) = -300
    c: DistanceX(g5) = 0
FEATURE [Sketcher::SketchObject] Sketch105  label="SketchBottom004"
  FullyConstrained = true
  Placement = pos=(0,0,20) rot=(0,0,1;0rad)
  sketch-geometry (6):
    g0: LineSegment StartX=37.5 StartY=-351.614 StartZ=0 EndX=60.6763 EndY=-280.285 EndZ=0
    g1: LineSegment StartX=60.6763 StartY=-280.285 StartZ=0 EndX=0 EndY=-236.201 EndZ=0
    g2: LineSegment StartX=0 StartY=-236.201 StartZ=0 EndX=-60.6763 EndY=-280.285 EndZ=0
    g3: LineSegment StartX=-60.6763 StartY=-280.285 StartZ=0 EndX=-37.5 EndY=-351.614 EndZ=0
    g4: LineSegment StartX=-37.5 StartY=-351.614 StartZ=0 EndX=37.5 EndY=-351.614 EndZ=0
    g5: Circle CenterX=0 CenterY=-300 CenterZ=0 NormalX=0 NormalY=0 NormalZ=1 AngleXU=0 Radius=63.7988
  constraints (15):
    c: Coincident(g0,g1)
    c: Coincident(g1,g2)
    c: Coincident(g2,g3)
    c: Coincident(g3,g4)
    c: Coincident(g4,g0)
    c: Equal(g0, g1-g4) x4
    c: PointOnObject(g0,g5)
    c: PointOnObject(g1,g5)
    c: PointOnObject(g2,g5)
    c: PointOnObject(g3,g5)
    c: PointOnObject(g4,g5)
    c: Horizontal(g4)
    c: DistanceX(g4,g4) = 75
    c: DistanceX(g5) = 0
    c: DistanceY(g5) = -300
FEATURE [Part::Loft] Loft024
  Closed = false
  MaxDegree = 5
  Ruled = false
  Sections = -> [Sketch104,Sketch105]
  Solid = true
FEATURE [Sketcher::SketchObject] Sketch106  label="SketchTop005"
  FullyConstrained = true
  sketch-geometry (6):
    g0: LineSegment StartX=47.5 StartY=-365.378 StartZ=0 EndX=76.8566 EndY=-275.028 EndZ=0
    g1: LineSegment StartX=76.8566 StartY=-275.028 StartZ=0 EndX=1.9185e-12 EndY=-219.188 EndZ=0
    g2: LineSegment StartX=1.9185e-12 StartY=-219.188 StartZ=0 EndX=-76.8566 EndY=-275.028 EndZ=0
    g3: LineSegment StartX=-76.8566 StartY=-275.028 StartZ=0 EndX=-47.5 EndY=-365.378 EndZ=0
    g4: LineSegment StartX=-47.5 StartY=-365.378 StartZ=0 EndX=47.5 EndY=-365.378 EndZ=0
    g5: Circle CenterX=0 CenterY=-300 CenterZ=0 NormalX=0 NormalY=0 NormalZ=1 AngleXU=0 Radius=80.8118
  constraints (15):
    c: Coincident(g0,g1)
    c: Coincident(g1,g2)
    c: Coincident(g2,g3)
    c: Coincident(g3,g4)
    c: Coincident(g4,g0)
    c: Equal(g0, g1-g4) x4
    c: PointOnObject(g0,g5)
    c: PointOnObject(g1,g5)
    c: PointOnObject(g2,g5)
    c: PointOnObject(g3,g5)
    c: PointOnObject(g4,g5)
    c: Horizontal(g4)
    c: DistanceX(g4,g4) = 95
    c: DistanceY(g5) = -300
    c: DistanceX(g5) = 0
FEATURE [Sketcher::SketchObject] Sketch107  label="SketchBottom005"
  FullyConstrained = true
  Placement = pos=(0,0,20) rot=(0,0,1;0rad)
  sketch-geometry (6):
    g0: LineSegment StartX=35 StartY=-348.173 StartZ=0 EndX=56.6312 EndY=-281.599 EndZ=0
    g1: LineSegment StartX=56.6312 StartY=-281.599 StartZ=0 EndX=0 EndY=-240.454 EndZ=0
    g2: LineSegment StartX=0 StartY=-240.454 StartZ=0 EndX=-56.6312 EndY=-281.599 EndZ=0
    g3: LineSegment StartX=-56.6312 StartY=-281.599 StartZ=0 EndX=-35 EndY=-348.173 EndZ=0
    g4: LineSegment StartX=-35 StartY=-348.173 StartZ=0 EndX=35 EndY=-348.173 EndZ=0
    g5: Circle CenterX=0 CenterY=-300 CenterZ=0 NormalX=0 NormalY=0 NormalZ=1 AngleXU=0 Radius=59.5456
  constraints (15):
    c: Coincident(g0,g1)
    c: Coincident(g1,g2)
    c: Coincident(g2,g3)
    c: Coincident(g3,g4)
    c: Coincident(g4,g0)
    c: Equal(g0, g1-g4) x4
    c: PointOnObject(g0,g5)
    c: PointOnObject(g1,g5)
    c: PointOnObject(g2,g5)
    c: PointOnObject(g3,g5)
    c: PointOnObject(g4,g5)
    c: Horizontal(g4)
    c: DistanceX(g4,g4) = 70
    c: DistanceX(g5) = 0
    c: DistanceY(g5) = -300
FEATURE [Part::Loft] Loft025
  Closed = false
  MaxDegree = 5
  Ruled = false
  Sections = -> [Sketch106,Sketch107]
  Solid = true
FEATURE [Part::Cut] Cut045  label="srsCone002"
  Base = -> Loft024
  Placement = pos=(0,0,-36) rot=(0,0,1;0rad)
  Tool = -> Loft025
FEATURE [Part::Fillet] Fillet035
  Base = -> Cut045
  Edges = 5 edges r=1.5: [Edge3,Edge15,Edge16,Edge17,Edge18]
FEATURE [Part::Fillet] Fillet036
  Base = -> Fillet035
  Edges = 5 edges r=1.5: [Edge4,Edge7,Edge11,Edge12,Edge13]
FEATURE [Part::Fillet] Fillet037
  Base = -> Fillet036
  Edges = 5 edges r=2: [Edge1,Edge3,Edge5,Edge15,Edge17]
FEATURE [Part::Fillet] Fillet038  label="srsCone003"
  Base = -> Fillet037
  Edges = 5 edges r=1.5: [Edge63,Edge64,Edge65,Edge66,Edge67]
  Placement = pos=(0,0,-18) rot=(0,0,1;0rad)
FEATURE [Sketcher::SketchObject] Sketch108  label="SketchTop006"
  FullyConstrained = true
  sketch-geometry (6):
    g0: LineSegment StartX=50 StartY=-368.819 StartZ=0 EndX=80.9017 EndY=-273.713 EndZ=0
    g1: LineSegment StartX=80.9017 StartY=-273.713 StartZ=0 EndX=0 EndY=-214.935 EndZ=0
    g2: LineSegment StartX=0 StartY=-214.935 StartZ=0 EndX=-80.9017 EndY=-273.713 EndZ=0
    g3: LineSegment StartX=-80.9017 StartY=-273.713 StartZ=0 EndX=-50 EndY=-368.819 EndZ=0
    g4: LineSegment StartX=-50 StartY=-368.819 StartZ=0 EndX=50 EndY=-368.819 EndZ=0
    g5: Circle CenterX=0 CenterY=-300 CenterZ=0 NormalX=0 NormalY=0 NormalZ=1 AngleXU=0 Radius=85.0651
  constraints (15):
    c: Coincident(g0,g1)
    c: Coincident(g1,g2)
    c: Coincident(g2,g3)
    c: Coincident(g3,g4)
    c: Coincident(g4,g0)
    c: Equal(g0, g1-g4) x4
    c: PointOnObject(g0,g5)
    c: PointOnObject(g1,g5)
    c: PointOnObject(g2,g5)
    c: PointOnObject(g3,g5)
    c: PointOnObject(g4,g5)
    c: Horizontal(g4)
    c: DistanceX(g4,g4) = 100
    c: DistanceY(g5) = -300
    c: DistanceX(g5) = 0
FEATURE [Sketcher::SketchObject] Sketch109  label="SketchBottom006"
  FullyConstrained = true
  Placement = pos=(0,0,20) rot=(0,0,1;0rad)
  sketch-geometry (6):
    g0: LineSegment StartX=37.5 StartY=-351.614 StartZ=0 EndX=60.6763 EndY=-280.285 EndZ=0
    g1: LineSegment StartX=60.6763 StartY=-280.285 StartZ=0 EndX=0 EndY=-236.201 EndZ=0
    g2: LineSegment StartX=0 StartY=-236.201 StartZ=0 EndX=-60.6763 EndY=-280.285 EndZ=0
    g3: LineSegment StartX=-60.6763 StartY=-280.285 StartZ=0 EndX=-37.5 EndY=-351.614 EndZ=0
    g4: LineSegment StartX=-37.5 StartY=-351.614 StartZ=0 EndX=37.5 EndY=-351.614 EndZ=0
    g5: Circle CenterX=0 CenterY=-300 CenterZ=0 NormalX=0 NormalY=0 NormalZ=1 AngleXU=0 Radius=63.7988
  constraints (15):
    c: Coincident(g0,g1)
    c: Coincident(g1,g2)
    c: Coincident(g2,g3)
    c: Coincident(g3,g4)
    c: Coincident(g4,g0)
    c: Equal(g0, g1-g4) x4
    c: PointOnObject(g0,g5)
    c: PointOnObject(g1,g5)
    c: PointOnObject(g2,g5)
    c: PointOnObject(g3,g5)
    c: PointOnObject(g4,g5)
    c: Horizontal(g4)
    c: DistanceX(g4,g4) = 75
    c: DistanceX(g5) = 0
    c: DistanceY(g5) = -300
FEATURE [Part::Loft] Loft026
  Closed = false
  MaxDegree = 5
  Ruled = false
  Sections = -> [Sketch108,Sketch109]
  Solid = true
FEATURE [Sketcher::SketchObject] Sketch110  label="SketchTop007"
  FullyConstrained = true
  sketch-geometry (6):
    g0: LineSegment StartX=47.5 StartY=-365.378 StartZ=0 EndX=76.8566 EndY=-275.028 EndZ=0
    g1: LineSegment StartX=76.8566 StartY=-275.028 StartZ=0 EndX=1.9185e-12 EndY=-219.188 EndZ=0
    g2: LineSegment StartX=1.9185e-12 StartY=-219.188 StartZ=0 EndX=-76.8566 EndY=-275.028 EndZ=0
    g3: LineSegment StartX=-76.8566 StartY=-275.028 StartZ=0 EndX=-47.5 EndY=-365.378 EndZ=0
    g4: LineSegment StartX=-47.5 StartY=-365.378 StartZ=0 EndX=47.5 EndY=-365.378 EndZ=0
    g5: Circle CenterX=0 CenterY=-300 CenterZ=0 NormalX=0 NormalY=0 NormalZ=1 AngleXU=0 Radius=80.8118
  constraints (15):
    c: Coincident(g0,g1)
    c: Coincident(g1,g2)
    c: Coincident(g2,g3)
    c: Coincident(g3,g4)
    c: Coincident(g4,g0)
    c: Equal(g0, g1-g4) x4
    c: PointOnObject(g0,g5)
    c: PointOnObject(g1,g5)
    c: PointOnObject(g2,g5)
    c: PointOnObject(g3,g5)
    c: PointOnObject(g4,g5)
    c: Horizontal(g4)
    c: DistanceX(g4,g4) = 95
    c: DistanceY(g5) = -300
    c: DistanceX(g5) = 0
FEATURE [Sketcher::SketchObject] Sketch111  label="SketchBottom007"
  FullyConstrained = true
  Placement = pos=(0,0,20) rot=(0,0,1;0rad)
  sketch-geometry (6):
    g0: LineSegment StartX=35 StartY=-348.173 StartZ=0 EndX=56.6312 EndY=-281.599 EndZ=0
    g1: LineSegment StartX=56.6312 StartY=-281.599 StartZ=0 EndX=0 EndY=-240.454 EndZ=0
    g2: LineSegment StartX=0 StartY=-240.454 StartZ=0 EndX=-56.6312 EndY=-281.599 EndZ=0
    g3: LineSegment StartX=-56.6312 StartY=-281.599 StartZ=0 EndX=-35 EndY=-348.173 EndZ=0
    g4: LineSegment StartX=-35 StartY=-348.173 StartZ=0 EndX=35 EndY=-348.173 EndZ=0
    g5: Circle CenterX=0 CenterY=-300 CenterZ=0 NormalX=0 NormalY=0 NormalZ=1 AngleXU=0 Radius=59.5456
  constraints (15):
    c: Coincident(g0,g1)
    c: Coincident(g1,g2)
    c: Coincident(g2,g3)
    c: Coincident(g3,g4)
    c: Coincident(g4,g0)
    c: Equal(g0, g1-g4) x4
    c: PointOnObject(g0,g5)
    c: PointOnObject(g1,g5)
    c: PointOnObject(g2,g5)
    c: PointOnObject(g3,g5)
    c: PointOnObject(g4,g5)
    c: Horizontal(g4)
    c: DistanceX(g4,g4) = 70
    c: DistanceX(g5) = 0
    c: DistanceY(g5) = -300
FEATURE [Part::Loft] Loft027
  Closed = false
  MaxDegree = 5
  Ruled = false
  Sections = -> [Sketch110,Sketch111]
  Solid = true
FEATURE [Part::Cut] Cut046  label="srsCone004"
  Base = -> Loft026
  Placement = pos=(0,0,-36) rot=(0,0,1;0rad)
  Tool = -> Loft027
FEATURE [Part::Fillet] Fillet039
  Base = -> Cut046
  Edges = 5 edges r=1.5: [Edge3,Edge15,Edge16,Edge17,Edge18]
FEATURE [Part::Fillet] Fillet040
  Base = -> Fillet039
  Edges = 5 edges r=1.5: [Edge4,Edge7,Edge11,Edge12,Edge13]
FEATURE [Part::Fillet] Fillet041
  Base = -> Fillet040
  Edges = 5 edges r=2: [Edge1,Edge3,Edge5,Edge15,Edge17]
FEATURE [Part::Fillet] Fillet042  label="srsCone005"
  Base = -> Fillet041
  Edges = 5 edges r=1.5: [Edge63,Edge64,Edge65,Edge66,Edge67]
  Placement = pos=(0,0,-36) rot=(0,0,1;0rad)
FEATURE [Sketcher::SketchObject] Sketch112  label="SketchTop008"
  FullyConstrained = true
  sketch-geometry (6):
    g0: LineSegment StartX=50 StartY=-368.819 StartZ=0 EndX=80.9017 EndY=-273.713 EndZ=0
    g1: LineSegment StartX=80.9017 StartY=-273.713 StartZ=0 EndX=0 EndY=-214.935 EndZ=0
    g2: LineSegment StartX=0 StartY=-214.935 StartZ=0 EndX=-80.9017 EndY=-273.713 EndZ=0
    g3: LineSegment StartX=-80.9017 StartY=-273.713 StartZ=0 EndX=-50 EndY=-368.819 EndZ=0
    g4: LineSegment StartX=-50 StartY=-368.819 StartZ=0 EndX=50 EndY=-368.819 EndZ=0
    g5: Circle CenterX=0 CenterY=-300 CenterZ=0 NormalX=0 NormalY=0 NormalZ=1 AngleXU=0 Radius=85.0651
  constraints (15):
    c: Coincident(g0,g1)
    c: Coincident(g1,g2)
    c: Coincident(g2,g3)
    c: Coincident(g3,g4)
    c: Coincident(g4,g0)
    c: Equal(g0, g1-g4) x4
    c: PointOnObject(g0,g5)
    c: PointOnObject(g1,g5)
    c: PointOnObject(g2,g5)
    c: PointOnObject(g3,g5)
    c: PointOnObject(g4,g5)
    c: Horizontal(g4)
    c: DistanceX(g4,g4) = 100
    c: DistanceY(g5) = -300
    c: DistanceX(g5) = 0
FEATURE [Sketcher::SketchObject] Sketch113  label="SketchBottom008"
  FullyConstrained = true
  Placement = pos=(0,0,20) rot=(0,0,1;0rad)
  sketch-geometry (6):
    g0: LineSegment StartX=37.5 StartY=-351.614 StartZ=0 EndX=60.6763 EndY=-280.285 EndZ=0
    g1: LineSegment StartX=60.6763 StartY=-280.285 StartZ=0 EndX=0 EndY=-236.201 EndZ=0
    g2: LineSegment StartX=0 StartY=-236.201 StartZ=0 EndX=-60.6763 EndY=-280.285 EndZ=0
    g3: LineSegment StartX=-60.6763 StartY=-280.285 StartZ=0 EndX=-37.5 EndY=-351.614 EndZ=0
    g4: LineSegment StartX=-37.5 StartY=-351.614 StartZ=0 EndX=37.5 EndY=-351.614 EndZ=0
    g5: Circle CenterX=0 CenterY=-300 CenterZ=0 NormalX=0 NormalY=0 NormalZ=1 AngleXU=0 Radius=63.7988
  constraints (15):
    c: Coincident(g0,g1)
    c: Coincident(g1,g2)
    c: Coincident(g2,g3)
    c: Coincident(g3,g4)
    c: Coincident(g4,g0)
    c: Equal(g0, g1-g4) x4
    c: PointOnObject(g0,g5)
    c: PointOnObject(g1,g5)
    c: PointOnObject(g2,g5)
    c: PointOnObject(g3,g5)
    c: PointOnObject(g4,g5)
    c: Horizontal(g4)
    c: DistanceX(g4,g4) = 75
    c: DistanceX(g5) = 0
    c: DistanceY(g5) = -300
FEATURE [Part::Loft] Loft028
  Closed = false
  MaxDegree = 5
  Ruled = false
  Sections = -> [Sketch112,Sketch113]
  Solid = true
FEATURE [Sketcher::SketchObject] Sketch114  label="SketchTop009"
  FullyConstrained = true
  sketch-geometry (6):
    g0: LineSegment StartX=47.5 StartY=-365.378 StartZ=0 EndX=76.8566 EndY=-275.028 EndZ=0
    g1: LineSegment StartX=76.8566 StartY=-275.028 StartZ=0 EndX=1.9185e-12 EndY=-219.188 EndZ=0
    g2: LineSegment StartX=1.9185e-12 StartY=-219.188 StartZ=0 EndX=-76.8566 EndY=-275.028 EndZ=0
    g3: LineSegment StartX=-76.8566 StartY=-275.028 StartZ=0 EndX=-47.5 EndY=-365.378 EndZ=0
    g4: LineSegment StartX=-47.5 StartY=-365.378 StartZ=0 EndX=47.5 EndY=-365.378 EndZ=0
    g5: Circle CenterX=0 CenterY=-300 CenterZ=0 NormalX=0 NormalY=0 NormalZ=1 AngleXU=0 Radius=80.8118
  constraints (15):
    c: Coincident(g0,g1)
    c: Coincident(g1,g2)
    c: Coincident(g2,g3)
    c: Coincident(g3,g4)
    c: Coincident(g4,g0)
    c: Equal(g0, g1-g4) x4
    c: PointOnObject(g0,g5)
    c: PointOnObject(g1,g5)
    c: PointOnObject(g2,g5)
    c: PointOnObject(g3,g5)
    c: PointOnObject(g4,g5)
    c: Horizontal(g4)
    c: DistanceX(g4,g4) = 95
    c: DistanceY(g5) = -300
    c: DistanceX(g5) = 0
FEATURE [Sketcher::SketchObject] Sketch115  label="SketchBottom009"
  FullyConstrained = true
  Placement = pos=(0,0,20) rot=(0,0,1;0rad)
  sketch-geometry (6):
    g0: LineSegment StartX=35 StartY=-348.173 StartZ=0 EndX=56.6312 EndY=-281.599 EndZ=0
    g1: LineSegment StartX=56.6312 StartY=-281.599 StartZ=0 EndX=0 EndY=-240.454 EndZ=0
    g2: LineSegment StartX=0 StartY=-240.454 StartZ=0 EndX=-56.6312 EndY=-281.599 EndZ=0
    g3: LineSegment StartX=-56.6312 StartY=-281.599 StartZ=0 EndX=-35 EndY=-348.173 EndZ=0
    g4: LineSegment StartX=-35 StartY=-348.173 StartZ=0 EndX=35 EndY=-348.173 EndZ=0
    g5: Circle CenterX=0 CenterY=-300 CenterZ=0 NormalX=0 NormalY=0 NormalZ=1 AngleXU=0 Radius=59.5456
  constraints (15):
    c: Coincident(g0,g1)
    c: Coincident(g1,g2)
    c: Coincident(g2,g3)
    c: Coincident(g3,g4)
    c: Coincident(g4,g0)
    c: Equal(g0, g1-g4) x4
    c: PointOnObject(g0,g5)
    c: PointOnObject(g1,g5)
    c: PointOnObject(g2,g5)
    c: PointOnObject(g3,g5)
    c: PointOnObject(g4,g5)
    c: Horizontal(g4)
    c: DistanceX(g4,g4) = 70
    c: DistanceX(g5) = 0
    c: DistanceY(g5) = -300
FEATURE [Part::Loft] Loft029
  Closed = false
  MaxDegree = 5
  Ruled = false
  Sections = -> [Sketch114,Sketch115]
  Solid = true
FEATURE [Part::Cut] Cut047  label="srsCone006"
  Base = -> Loft028
  Placement = pos=(0,0,-36) rot=(0,0,1;0rad)
  Tool = -> Loft029
FEATURE [Part::Fillet] Fillet043
  Base = -> Cut047
  Edges = 5 edges r=1.5: [Edge3,Edge15,Edge16,Edge17,Edge18]
FEATURE [Part::Fillet] Fillet044
  Base = -> Fillet043
  Edges = 5 edges r=1.5: [Edge4,Edge7,Edge11,Edge12,Edge13]
FEATURE [Part::Fillet] Fillet045
  Base = -> Fillet044
  Edges = 5 edges r=2: [Edge1,Edge3,Edge5,Edge15,Edge17]
FEATURE [Part::Fillet] Fillet046  label="srsCone007"
  Base = -> Fillet045
  Edges = 5 edges r=1.5: [Edge63,Edge64,Edge65,Edge66,Edge67]
  Placement = pos=(0,0,-54) rot=(0,0,1;0rad)
FEATURE [Sketcher::SketchObject] Sketch116  label="SketchTop010"
  FullyConstrained = true
  sketch-geometry (6):
    g0: LineSegment StartX=50 StartY=-368.819 StartZ=0 EndX=80.9017 EndY=-273.713 EndZ=0
    g1: LineSegment StartX=80.9017 StartY=-273.713 StartZ=0 EndX=0 EndY=-214.935 EndZ=0
    g2: LineSegment StartX=0 StartY=-214.935 StartZ=0 EndX=-80.9017 EndY=-273.713 EndZ=0
    g3: LineSegment StartX=-80.9017 StartY=-273.713 StartZ=0 EndX=-50 EndY=-368.819 EndZ=0
    g4: LineSegment StartX=-50 StartY=-368.819 StartZ=0 EndX=50 EndY=-368.819 EndZ=0
    g5: Circle CenterX=0 CenterY=-300 CenterZ=0 NormalX=0 NormalY=0 NormalZ=1 AngleXU=0 Radius=85.0651
  constraints (15):
    c: Coincident(g0,g1)
    c: Coincident(g1,g2)
    c: Coincident(g2,g3)
    c: Coincident(g3,g4)
    c: Coincident(g4,g0)
    c: Equal(g0, g1-g4) x4
    c: PointOnObject(g0,g5)
    c: PointOnObject(g1,g5)
    c: PointOnObject(g2,g5)
    c: PointOnObject(g3,g5)
    c: PointOnObject(g4,g5)
    c: Horizontal(g4)
    c: DistanceX(g4,g4) = 100
    c: DistanceY(g5) = -300
    c: DistanceX(g5) = 0
FEATURE [Sketcher::SketchObject] Sketch117  label="SketchBottom010"
  FullyConstrained = true
  Placement = pos=(0,0,20) rot=(0,0,1;0rad)
  sketch-geometry (6):
    g0: LineSegment StartX=37.5 StartY=-351.614 StartZ=0 EndX=60.6763 EndY=-280.285 EndZ=0
    g1: LineSegment StartX=60.6763 StartY=-280.285 StartZ=0 EndX=0 EndY=-236.201 EndZ=0
    g2: LineSegment StartX=0 StartY=-236.201 StartZ=0 EndX=-60.6763 EndY=-280.285 EndZ=0
    g3: LineSegment StartX=-60.6763 StartY=-280.285 StartZ=0 EndX=-37.5 EndY=-351.614 EndZ=0
    g4: LineSegment StartX=-37.5 StartY=-351.614 StartZ=0 EndX=37.5 EndY=-351.614 EndZ=0
    g5: Circle CenterX=0 CenterY=-300 CenterZ=0 NormalX=0 NormalY=0 NormalZ=1 AngleXU=0 Radius=63.7988
  constraints (15):
    c: Coincident(g0,g1)
    c: Coincident(g1,g2)
    c: Coincident(g2,g3)
    c: Coincident(g3,g4)
    c: Coincident(g4,g0)
    c: Equal(g0, g1-g4) x4
    c: PointOnObject(g0,g5)
    c: PointOnObject(g1,g5)
    c: PointOnObject(g2,g5)
    c: PointOnObject(g3,g5)
    c: PointOnObject(g4,g5)
    c: Horizontal(g4)
    c: DistanceX(g4,g4) = 75
    c: DistanceX(g5) = 0
    c: DistanceY(g5) = -300
FEATURE [Part::Loft] Loft030
  Closed = false
  MaxDegree = 5
  Ruled = false
  Sections = -> [Sketch116,Sketch117]
  Solid = true
FEATURE [Sketcher::SketchObject] Sketch118  label="SketchTop011"
  FullyConstrained = true
  sketch-geometry (6):
    g0: LineSegment StartX=47.5 StartY=-365.378 StartZ=0 EndX=76.8566 EndY=-275.028 EndZ=0
    g1: LineSegment StartX=76.8566 StartY=-275.028 StartZ=0 EndX=1.9185e-12 EndY=-219.188 EndZ=0
    g2: LineSegment StartX=1.9185e-12 StartY=-219.188 StartZ=0 EndX=-76.8566 EndY=-275.028 EndZ=0
    g3: LineSegment StartX=-76.8566 StartY=-275.028 StartZ=0 EndX=-47.5 EndY=-365.378 EndZ=0
    g4: LineSegment StartX=-47.5 StartY=-365.378 StartZ=0 EndX=47.5 EndY=-365.378 EndZ=0
    g5: Circle CenterX=0 CenterY=-300 CenterZ=0 NormalX=0 NormalY=0 NormalZ=1 AngleXU=0 Radius=80.8118
  constraints (15):
    c: Coincident(g0,g1)
    c: Coincident(g1,g2)
    c: Coincident(g2,g3)
    c: Coincident(g3,g4)
    c: Coincident(g4,g0)
    c: Equal(g0, g1-g4) x4
    c: PointOnObject(g0,g5)
    c: PointOnObject(g1,g5)
    c: PointOnObject(g2,g5)
    c: PointOnObject(g3,g5)
    c: PointOnObject(g4,g5)
    c: Horizontal(g4)
    c: DistanceX(g4,g4) = 95
    c: DistanceY(g5) = -300
    c: DistanceX(g5) = 0
FEATURE [Sketcher::SketchObject] Sketch119  label="SketchBottom011"
  FullyConstrained = true
  Placement = pos=(0,0,20) rot=(0,0,1;0rad)
  sketch-geometry (6):
    g0: LineSegment StartX=35 StartY=-348.173 StartZ=0 EndX=56.6312 EndY=-281.599 EndZ=0
    g1: LineSegment StartX=56.6312 StartY=-281.599 StartZ=0 EndX=0 EndY=-240.454 EndZ=0
    g2: LineSegment StartX=0 StartY=-240.454 StartZ=0 EndX=-56.6312 EndY=-281.599 EndZ=0
    g3: LineSegment StartX=-56.6312 StartY=-281.599 StartZ=0 EndX=-35 EndY=-348.173 EndZ=0
    g4: LineSegment StartX=-35 StartY=-348.173 StartZ=0 EndX=35 EndY=-348.173 EndZ=0
    g5: Circle CenterX=0 CenterY=-300 CenterZ=0 NormalX=0 NormalY=0 NormalZ=1 AngleXU=0 Radius=59.5456
  constraints (15):
    c: Coincident(g0,g1)
    c: Coincident(g1,g2)
    c: Coincident(g2,g3)
    c: Coincident(g3,g4)
    c: Coincident(g4,g0)
    c: Equal(g0, g1-g4) x4
    c: PointOnObject(g0,g5)
    c: PointOnObject(g1,g5)
    c: PointOnObject(g2,g5)
    c: PointOnObject(g3,g5)
    c: PointOnObject(g4,g5)
    c: Horizontal(g4)
    c: DistanceX(g4,g4) = 70
    c: DistanceX(g5) = 0
    c: DistanceY(g5) = -300
FEATURE [Part::Loft] Loft031
  Closed = false
  MaxDegree = 5
  Ruled = false
  Sections = -> [Sketch118,Sketch119]
  Solid = true
FEATURE [Part::Cut] Cut048  label="srsCone008"
  Base = -> Loft030
  Placement = pos=(0,0,-36) rot=(0,0,1;0rad)
  Tool = -> Loft031
FEATURE [Part::Fillet] Fillet047
  Base = -> Cut048
  Edges = 5 edges r=1.5: [Edge3,Edge15,Edge16,Edge17,Edge18]
FEATURE [Part::Fillet] Fillet048
  Base = -> Fillet047
  Edges = 5 edges r=1.5: [Edge4,Edge7,Edge11,Edge12,Edge13]
FEATURE [Part::Fillet] Fillet049
  Base = -> Fillet048
  Edges = 5 edges r=2: [Edge1,Edge3,Edge5,Edge15,Edge17]
FEATURE [Part::Fillet] Fillet050  label="srsCone009"
  Base = -> Fillet049
  Edges = 5 edges r=1.5: [Edge63,Edge64,Edge65,Edge66,Edge67]
  Placement = pos=(0,0,-72) rot=(0,0,1;0rad)
FEATURE [Sketcher::SketchObject] Sketch120  label="SketchTop012"
  FullyConstrained = true
  sketch-geometry (6):
    g0: LineSegment StartX=50 StartY=-368.819 StartZ=0 EndX=80.9017 EndY=-273.713 EndZ=0
    g1: LineSegment StartX=80.9017 StartY=-273.713 StartZ=0 EndX=0 EndY=-214.935 EndZ=0
    g2: LineSegment StartX=0 StartY=-214.935 StartZ=0 EndX=-80.9017 EndY=-273.713 EndZ=0
    g3: LineSegment StartX=-80.9017 StartY=-273.713 StartZ=0 EndX=-50 EndY=-368.819 EndZ=0
    g4: LineSegment StartX=-50 StartY=-368.819 StartZ=0 EndX=50 EndY=-368.819 EndZ=0
    g5: Circle CenterX=0 CenterY=-300 CenterZ=0 NormalX=0 NormalY=0 NormalZ=1 AngleXU=0 Radius=85.0651
  constraints (15):
    c: Coincident(g0,g1)
    c: Coincident(g1,g2)
    c: Coincident(g2,g3)
    c: Coincident(g3,g4)
    c: Coincident(g4,g0)
    c: Equal(g0, g1-g4) x4
    c: PointOnObject(g0,g5)
    c: PointOnObject(g1,g5)
    c: PointOnObject(g2,g5)
    c: PointOnObject(g3,g5)
    c: PointOnObject(g4,g5)
    c: Horizontal(g4)
    c: DistanceX(g4,g4) = 100
    c: DistanceY(g5) = -300
    c: DistanceX(g5) = 0
FEATURE [Sketcher::SketchObject] Sketch121  label="SketchBottom012"
  FullyConstrained = true
  Placement = pos=(0,0,20) rot=(0,0,1;0rad)
  sketch-geometry (6):
    g0: LineSegment StartX=37.5 StartY=-351.614 StartZ=0 EndX=60.6763 EndY=-280.285 EndZ=0
    g1: LineSegment StartX=60.6763 StartY=-280.285 StartZ=0 EndX=0 EndY=-236.201 EndZ=0
    g2: LineSegment StartX=0 StartY=-236.201 StartZ=0 EndX=-60.6763 EndY=-280.285 EndZ=0
    g3: LineSegment StartX=-60.6763 StartY=-280.285 StartZ=0 EndX=-37.5 EndY=-351.614 EndZ=0
    g4: LineSegment StartX=-37.5 StartY=-351.614 StartZ=0 EndX=37.5 EndY=-351.614 EndZ=0
    g5: Circle CenterX=0 CenterY=-300 CenterZ=0 NormalX=0 NormalY=0 NormalZ=1 AngleXU=0 Radius=63.7988
  constraints (15):
    c: Coincident(g0,g1)
    c: Coincident(g1,g2)
    c: Coincident(g2,g3)
    c: Coincident(g3,g4)
    c: Coincident(g4,g0)
    c: Equal(g0, g1-g4) x4
    c: PointOnObject(g0,g5)
    c: PointOnObject(g1,g5)
    c: PointOnObject(g2,g5)
    c: PointOnObject(g3,g5)
    c: PointOnObject(g4,g5)
    c: Horizontal(g4)
    c: DistanceX(g4,g4) = 75
    c: DistanceX(g5) = 0
    c: DistanceY(g5) = -300
FEATURE [Part::Loft] Loft032
  Closed = false
  MaxDegree = 5
  Ruled = false
  Sections = -> [Sketch120,Sketch121]
  Solid = true
FEATURE [Sketcher::SketchObject] Sketch122  label="SketchTop013"
  FullyConstrained = true
  sketch-geometry (6):
    g0: LineSegment StartX=47.5 StartY=-365.378 StartZ=0 EndX=76.8566 EndY=-275.028 EndZ=0
    g1: LineSegment StartX=76.8566 StartY=-275.028 StartZ=0 EndX=1.9185e-12 EndY=-219.188 EndZ=0
    g2: LineSegment StartX=1.9185e-12 StartY=-219.188 StartZ=0 EndX=-76.8566 EndY=-275.028 EndZ=0
    g3: LineSegment StartX=-76.8566 StartY=-275.028 StartZ=0 EndX=-47.5 EndY=-365.378 EndZ=0
    g4: LineSegment StartX=-47.5 StartY=-365.378 StartZ=0 EndX=47.5 EndY=-365.378 EndZ=0
    g5: Circle CenterX=0 CenterY=-300 CenterZ=0 NormalX=0 NormalY=0 NormalZ=1 AngleXU=0 Radius=80.8118
  constraints (15):
    c: Coincident(g0,g1)
    c: Coincident(g1,g2)
    c: Coincident(g2,g3)
    c: Coincident(g3,g4)
    c: Coincident(g4,g0)
    c: Equal(g0, g1-g4) x4
    c: PointOnObject(g0,g5)
    c: PointOnObject(g1,g5)
    c: PointOnObject(g2,g5)
    c: PointOnObject(g3,g5)
    c: PointOnObject(g4,g5)
    c: Horizontal(g4)
    c: DistanceX(g4,g4) = 95
    c: DistanceY(g5) = -300
    c: DistanceX(g5) = 0
FEATURE [Sketcher::SketchObject] Sketch123  label="SketchBottom013"
  FullyConstrained = true
  Placement = pos=(0,0,20) rot=(0,0,1;0rad)
  sketch-geometry (6):
    g0: LineSegment StartX=35 StartY=-348.173 StartZ=0 EndX=56.6312 EndY=-281.599 EndZ=0
    g1: LineSegment StartX=56.6312 StartY=-281.599 StartZ=0 EndX=0 EndY=-240.454 EndZ=0
    g2: LineSegment StartX=0 StartY=-240.454 StartZ=0 EndX=-56.6312 EndY=-281.599 EndZ=0
    g3: LineSegment StartX=-56.6312 StartY=-281.599 StartZ=0 EndX=-35 EndY=-348.173 EndZ=0
    g4: LineSegment StartX=-35 StartY=-348.173 StartZ=0 EndX=35 EndY=-348.173 EndZ=0
    g5: Circle CenterX=0 CenterY=-300 CenterZ=0 NormalX=0 NormalY=0 NormalZ=1 AngleXU=0 Radius=59.5456
  constraints (15):
    c: Coincident(g0,g1)
    c: Coincident(g1,g2)
    c: Coincident(g2,g3)
    c: Coincident(g3,g4)
    c: Coincident(g4,g0)
    c: Equal(g0, g1-g4) x4
    c: PointOnObject(g0,g5)
    c: PointOnObject(g1,g5)
    c: PointOnObject(g2,g5)
    c: PointOnObject(g3,g5)
    c: PointOnObject(g4,g5)
    c: Horizontal(g4)
    c: DistanceX(g4,g4) = 70
    c: DistanceX(g5) = 0
    c: DistanceY(g5) = -300
FEATURE [Part::Loft] Loft033
  Closed = false
  MaxDegree = 5
  Ruled = false
  Sections = -> [Sketch122,Sketch123]
  Solid = true
FEATURE [Part::Cut] Cut049  label="srsCone010"
  Base = -> Loft032
  Placement = pos=(0,0,-36) rot=(0,0,1;0rad)
  Tool = -> Loft033
FEATURE [Part::Fillet] Fillet051
  Base = -> Cut049
  Edges = 5 edges r=1.5: [Edge3,Edge15,Edge16,Edge17,Edge18]
FEATURE [Part::Fillet] Fillet052
  Base = -> Fillet051
  Edges = 5 edges r=1.5: [Edge4,Edge7,Edge11,Edge12,Edge13]
FEATURE [Part::Fillet] Fillet053
  Base = -> Fillet052
  Edges = 5 edges r=2: [Edge1,Edge3,Edge5,Edge15,Edge17]
FEATURE [Part::Fillet] Fillet054  label="srsCone011"
  Base = -> Fillet053
  Edges = 5 edges r=1.5: [Edge63,Edge64,Edge65,Edge66,Edge67]
  Placement = pos=(0,0,-90) rot=(0,0,1;0rad)
FEATURE [Sketcher::SketchObject] Sketch124  label="SketchTop014"
  FullyConstrained = true
  sketch-geometry (6):
    g0: LineSegment StartX=50 StartY=-368.819 StartZ=0 EndX=80.9017 EndY=-273.713 EndZ=0
    g1: LineSegment StartX=80.9017 StartY=-273.713 StartZ=0 EndX=0 EndY=-214.935 EndZ=0
    g2: LineSegment StartX=0 StartY=-214.935 StartZ=0 EndX=-80.9017 EndY=-273.713 EndZ=0
    g3: LineSegment StartX=-80.9017 StartY=-273.713 StartZ=0 EndX=-50 EndY=-368.819 EndZ=0
    g4: LineSegment StartX=-50 StartY=-368.819 StartZ=0 EndX=50 EndY=-368.819 EndZ=0
    g5: Circle CenterX=0 CenterY=-300 CenterZ=0 NormalX=0 NormalY=0 NormalZ=1 AngleXU=0 Radius=85.0651
  constraints (15):
    c: Coincident(g0,g1)
    c: Coincident(g1,g2)
    c: Coincident(g2,g3)
    c: Coincident(g3,g4)
    c: Coincident(g4,g0)
    c: Equal(g0, g1-g4) x4
    c: PointOnObject(g0,g5)
    c: PointOnObject(g1,g5)
    c: PointOnObject(g2,g5)
    c: PointOnObject(g3,g5)
    c: PointOnObject(g4,g5)
    c: Horizontal(g4)
    c: DistanceX(g4,g4) = 100
    c: DistanceY(g5) = -300
    c: DistanceX(g5) = 0
FEATURE [Sketcher::SketchObject] Sketch125  label="SketchBottom014"
  FullyConstrained = true
  Placement = pos=(0,0,20) rot=(0,0,1;0rad)
  sketch-geometry (6):
    g0: LineSegment StartX=37.5 StartY=-351.614 StartZ=0 EndX=60.6763 EndY=-280.285 EndZ=0
    g1: LineSegment StartX=60.6763 StartY=-280.285 StartZ=0 EndX=0 EndY=-236.201 EndZ=0
    g2: LineSegment StartX=0 StartY=-236.201 StartZ=0 EndX=-60.6763 EndY=-280.285 EndZ=0
    g3: LineSegment StartX=-60.6763 StartY=-280.285 StartZ=0 EndX=-37.5 EndY=-351.614 EndZ=0
    g4: LineSegment StartX=-37.5 StartY=-351.614 StartZ=0 EndX=37.5 EndY=-351.614 EndZ=0
    g5: Circle CenterX=0 CenterY=-300 CenterZ=0 NormalX=0 NormalY=0 NormalZ=1 AngleXU=0 Radius=63.7988
  constraints (15):
    c: Coincident(g0,g1)
    c: Coincident(g1,g2)
    c: Coincident(g2,g3)
    c: Coincident(g3,g4)
    c: Coincident(g4,g0)
    c: Equal(g0, g1-g4) x4
    c: PointOnObject(g0,g5)
    c: PointOnObject(g1,g5)
    c: PointOnObject(g2,g5)
    c: PointOnObject(g3,g5)
    c: PointOnObject(g4,g5)
    c: Horizontal(g4)
    c: DistanceX(g4,g4) = 75
    c: DistanceX(g5) = 0
    c: DistanceY(g5) = -300
FEATURE [Part::Loft] Loft034
  Closed = false
  MaxDegree = 5
  Ruled = false
  Sections = -> [Sketch124,Sketch125]
  Solid = true
FEATURE [Sketcher::SketchObject] Sketch126  label="SketchTop015"
  FullyConstrained = true
  sketch-geometry (6):
    g0: LineSegment StartX=47.5 StartY=-365.378 StartZ=0 EndX=76.8566 EndY=-275.028 EndZ=0
    g1: LineSegment StartX=76.8566 StartY=-275.028 StartZ=0 EndX=1.9185e-12 EndY=-219.188 EndZ=0
    g2: LineSegment StartX=1.9185e-12 StartY=-219.188 StartZ=0 EndX=-76.8566 EndY=-275.028 EndZ=0
    g3: LineSegment StartX=-76.8566 StartY=-275.028 StartZ=0 EndX=-47.5 EndY=-365.378 EndZ=0
    g4: LineSegment StartX=-47.5 StartY=-365.378 StartZ=0 EndX=47.5 EndY=-365.378 EndZ=0
    g5: Circle CenterX=0 CenterY=-300 CenterZ=0 NormalX=0 NormalY=0 NormalZ=1 AngleXU=0 Radius=80.8118
  constraints (15):
    c: Coincident(g0,g1)
    c: Coincident(g1,g2)
    c: Coincident(g2,g3)
    c: Coincident(g3,g4)
    c: Coincident(g4,g0)
    c: Equal(g0, g1-g4) x4
    c: PointOnObject(g0,g5)
    c: PointOnObject(g1,g5)
    c: PointOnObject(g2,g5)
    c: PointOnObject(g3,g5)
    c: PointOnObject(g4,g5)
    c: Horizontal(g4)
    c: DistanceX(g4,g4) = 95
    c: DistanceY(g5) = -300
    c: DistanceX(g5) = 0
FEATURE [Sketcher::SketchObject] Sketch127  label="SketchBottom015"
  FullyConstrained = true
  Placement = pos=(0,0,20) rot=(0,0,1;0rad)
  sketch-geometry (6):
    g0: LineSegment StartX=35 StartY=-348.173 StartZ=0 EndX=56.6312 EndY=-281.599 EndZ=0
    g1: LineSegment StartX=56.6312 StartY=-281.599 StartZ=0 EndX=0 EndY=-240.454 EndZ=0
    g2: LineSegment StartX=0 StartY=-240.454 StartZ=0 EndX=-56.6312 EndY=-281.599 EndZ=0
    g3: LineSegment StartX=-56.6312 StartY=-281.599 StartZ=0 EndX=-35 EndY=-348.173 EndZ=0
    g4: LineSegment StartX=-35 StartY=-348.173 StartZ=0 EndX=35 EndY=-348.173 EndZ=0
    g5: Circle CenterX=0 CenterY=-300 CenterZ=0 NormalX=0 NormalY=0 NormalZ=1 AngleXU=0 Radius=59.5456
  constraints (15):
    c: Coincident(g0,g1)
    c: Coincident(g1,g2)
    c: Coincident(g2,g3)
    c: Coincident(g3,g4)
    c: Coincident(g4,g0)
    c: Equal(g0, g1-g4) x4
    c: PointOnObject(g0,g5)
    c: PointOnObject(g1,g5)
    c: PointOnObject(g2,g5)
    c: PointOnObject(g3,g5)
    c: PointOnObject(g4,g5)
    c: Horizontal(g4)
    c: DistanceX(g4,g4) = 70
    c: DistanceX(g5) = 0
    c: DistanceY(g5) = -300
FEATURE [Part::Loft] Loft035
  Closed = false
  MaxDegree = 5
  Ruled = false
  Sections = -> [Sketch126,Sketch127]
  Solid = true
FEATURE [Part::Cut] Cut050  label="srsCone012"
  Base = -> Loft034
  Placement = pos=(0,0,-36) rot=(0,0,1;0rad)
  Tool = -> Loft035
FEATURE [Part::Fillet] Fillet055
  Base = -> Cut050
  Edges = 5 edges r=1.5: [Edge3,Edge15,Edge16,Edge17,Edge18]
FEATURE [Part::Fillet] Fillet056
  Base = -> Fillet055
  Edges = 5 edges r=1.5: [Edge4,Edge7,Edge11,Edge12,Edge13]
FEATURE [Part::Fillet] Fillet057
  Base = -> Fillet056
  Edges = 5 edges r=2: [Edge1,Edge3,Edge5,Edge15,Edge17]
FEATURE [Part::Fillet] Fillet058  label="srsCone013"
  Base = -> Fillet057
  Edges = 5 edges r=1.5: [Edge63,Edge64,Edge65,Edge66,Edge67]
  Placement = pos=(0,0,-108) rot=(0,0,1;0rad)
FEATURE [Sketcher::SketchObject] Sketch128  label="SketchTop016"
  FullyConstrained = true
  sketch-geometry (6):
    g0: LineSegment StartX=50 StartY=-368.819 StartZ=0 EndX=80.9017 EndY=-273.713 EndZ=0
    g1: LineSegment StartX=80.9017 StartY=-273.713 StartZ=0 EndX=0 EndY=-214.935 EndZ=0
    g2: LineSegment StartX=0 StartY=-214.935 StartZ=0 EndX=-80.9017 EndY=-273.713 EndZ=0
    g3: LineSegment StartX=-80.9017 StartY=-273.713 StartZ=0 EndX=-50 EndY=-368.819 EndZ=0
    g4: LineSegment StartX=-50 StartY=-368.819 StartZ=0 EndX=50 EndY=-368.819 EndZ=0
    g5: Circle CenterX=0 CenterY=-300 CenterZ=0 NormalX=0 NormalY=0 NormalZ=1 AngleXU=0 Radius=85.0651
  constraints (15):
    c: Coincident(g0,g1)
    c: Coincident(g1,g2)
    c: Coincident(g2,g3)
    c: Coincident(g3,g4)
    c: Coincident(g4,g0)
    c: Equal(g0, g1-g4) x4
    c: PointOnObject(g0,g5)
    c: PointOnObject(g1,g5)
    c: PointOnObject(g2,g5)
    c: PointOnObject(g3,g5)
    c: PointOnObject(g4,g5)
    c: Horizontal(g4)
    c: DistanceX(g4,g4) = 100
    c: DistanceY(g5) = -300
    c: DistanceX(g5) = 0
FEATURE [Sketcher::SketchObject] Sketch129  label="SketchBottom016"
  FullyConstrained = true
  Placement = pos=(0,0,20) rot=(0,0,1;0rad)
  sketch-geometry (6):
    g0: LineSegment StartX=37.5 StartY=-351.614 StartZ=0 EndX=60.6763 EndY=-280.285 EndZ=0
    g1: LineSegment StartX=60.6763 StartY=-280.285 StartZ=0 EndX=0 EndY=-236.201 EndZ=0
    g2: LineSegment StartX=0 StartY=-236.201 StartZ=0 EndX=-60.6763 EndY=-280.285 EndZ=0
    g3: LineSegment StartX=-60.6763 StartY=-280.285 StartZ=0 EndX=-37.5 EndY=-351.614 EndZ=0
    g4: LineSegment StartX=-37.5 StartY=-351.614 StartZ=0 EndX=37.5 EndY=-351.614 EndZ=0
    g5: Circle CenterX=0 CenterY=-300 CenterZ=0 NormalX=0 NormalY=0 NormalZ=1 AngleXU=0 Radius=63.7988
  constraints (15):
    c: Coincident(g0,g1)
    c: Coincident(g1,g2)
    c: Coincident(g2,g3)
    c: Coincident(g3,g4)
    c: Coincident(g4,g0)
    c: Equal(g0, g1-g4) x4
    c: PointOnObject(g0,g5)
    c: PointOnObject(g1,g5)
    c: PointOnObject(g2,g5)
    c: PointOnObject(g3,g5)
    c: PointOnObject(g4,g5)
    c: Horizontal(g4)
    c: DistanceX(g4,g4) = 75
    c: DistanceX(g5) = 0
    c: DistanceY(g5) = -300
FEATURE [Part::Extrusion] Extrude  label="top"
  Base = -> Sketch129
  Dir = (0,0,1)
  DirMode = 2
  FaceMakerClass = Part::FaceMakerBullseye
  LengthFwd = 4
  LengthRev = 0
  Placement = pos=(0,0,-40) rot=(0,0,1;0rad)
  Solid = true
  Symmetric = false
FEATURE [Sketcher::SketchObject] Sketch  label="logoPanel"
  FullyConstrained = true
  Placement = pos=(0,0,-126) rot=(0,0,1;0rad)
  sketch-geometry (4):
    g0: LineSegment StartX=29.9062 StartY=-352 StartZ=0 EndX=27 EndY=-348 EndZ=0
    g1: LineSegment StartX=-27 StartY=-348 StartZ=0 EndX=-29.9062 EndY=-352 EndZ=0
    g2: LineSegment StartX=29.9062 StartY=-352 StartZ=0 EndX=-29.9062 EndY=-352 EndZ=0
    g3: LineSegment StartX=-27 StartY=-348 StartZ=0 EndX=27 EndY=-348 EndZ=0
  constraints (12):
    c: DistanceY(g1) = -352
    c: DistanceY(g1) = -348
    c: Coincident(g2,g0)
    c: Coincident(g2,g1)
    c: Horizontal(g2)
    c: Angle(g2,g1) = 0.942478
    c: Angle(g0,g2) = 0.942478
    c: DistanceX(g1) = -27
    c: DistanceX(g0) = 27
    c: Coincident(g3,g1)
    c: Coincident(g3,g0)
    c: Horizontal(g3)
FEATURE [Part::Feature] Part__Feature154  label="logoTopCut001"
  Placement = pos=(-31.2,-352,-123.5) rot=(0,0,1;0rad)
  shape: bbox 22.79 x 8 x 17.08 mm, 886 faces (baked)
FEATURE [Sketcher::SketchObject] Sketch130  label="logoPanel001"
  FullyConstrained = true
  Placement = pos=(0,0,-126) rot=(0,0,1;0rad)
  sketch-geometry (4):
    g0: LineSegment StartX=33.0778 StartY=-370 StartZ=0 EndX=20 EndY=-352 EndZ=0
    g1: LineSegment StartX=20 StartY=-352 StartZ=0 EndX=-20 EndY=-352 EndZ=0
    g2: LineSegment StartX=-20 StartY=-352 StartZ=0 EndX=-33.0778 EndY=-370 EndZ=0
    g3: LineSegment StartX=33.0778 StartY=-370 StartZ=0 EndX=-33.0778 EndY=-370 EndZ=0
  constraints (12):
    c: Coincident(g1,g0)
    c: Horizontal(g1)
    c: Coincident(g2,g1)
    c: DistanceY(g1) = -352
    c: Coincident(g3,g0)
    c: Coincident(g3,g2)
    c: Horizontal(g3)
    c: Angle(g3,g2) = 0.942478
    c: Angle(g0,g3) = 0.942478
    c: DistanceX(g0) = 20
    c: DistanceX(g1) = -20
    c: DistanceY(g2) = -370
FEATURE [Part::Feature] Part__Feature  label="ips7100s"
  Placement = pos=(24,-275,-121) rot=(0,0,1;0rad)
  shape: bbox 48.08 x 13.98 x 44.07 mm, 1935 faces (baked)
FEATURE [Part::Feature] Part__Feature155  label="fan"
  Placement = pos=(22.5475,33.2927,6) rot=(-0.588042,0.808831,0;3.14159rad)
  shape: bbox 15 x 15 x 4.502 mm, 133 faces (baked)
FEATURE [Part::Feature] Part__Feature001  label="plastic"
  Placement = pos=(22,36,-5.99e-13) rot=(1,0,0;3.14159rad)
  shape: bbox 48 x 37 x 12 mm, 162 faces, 21 solids (baked)
FEATURE [Part::Feature] Part__Feature002  label="metal_cover_connector"
  Placement = pos=(-2,18.5,11.5) rot=(0,0.707107,0.707107;3.14159rad)
  shape: bbox 48 x 37 x 6 mm, 58 faces (baked)
FEATURE [Part::Feature] Part__Feature003  label="metal_cover_fan"
  Placement = pos=(-2,18.5,0.5) rot=(0,-0.707107,0.707107;3.14159rad)
  shape: bbox 48 x 37 x 6 mm, 63 faces (baked)
FEATURE [Part::Feature] Part__Feature004  label="1_27mm_pin_right_angle"
  Placement = pos=(-0.770082,-1.65718,-0.233527) rot=(0,0,1;0rad)
  shape: bbox 2.2 x 4.2 x 0.4 mm, 17 faces (baked)
FEATURE [Part::Feature] Part__Feature005  label="1_27mm_plastic_for_pin"
  Placement = pos=(-0.452582,-1.45718,-0.233527) rot=(0,1,0;1.5708rad)
  shape: bbox 1.905 x 1 x 1.27 mm, 10 faces (baked)
FEATURE [Part::Feature] Part__Feature006  label="1_27mm_pin_right_angle001"
  Placement = pos=(-0.770082,-1.65718,-0.233527) rot=(0,0,1;0rad)
  shape: bbox 2.2 x 4.2 x 0.4 mm, 17 faces (baked)
FEATURE [Part::Feature] Part__Feature007  label="1_27mm_plastic_for_pin001"
  Placement = pos=(-0.452582,-1.45718,-0.233527) rot=(0,1,0;1.5708rad)
  shape: bbox 1.905 x 1 x 1.27 mm, 10 faces (baked)
FEATURE [Part::Feature] Part__Feature008  label="1_27mm_pin_right_angle002"
  Placement = pos=(-0.770082,-1.65718,-0.233527) rot=(0,0,1;0rad)
  shape: bbox 2.2 x 4.2 x 0.4 mm, 17 faces (baked)
FEATURE [Part::Feature] Part__Feature009  label="1_27mm_plastic_for_pin002"
  Placement = pos=(-0.452582,-1.45718,-0.233527) rot=(0,1,0;1.5708rad)
  shape: bbox 1.905 x 1 x 1.27 mm, 10 faces (baked)
FEATURE [Part::Feature] Part__Feature010  label="1_27mm_pin_right_angle003"
  Placement = pos=(-0.770082,-1.65718,-0.233527) rot=(0,0,1;0rad)
  shape: bbox 2.2 x 4.2 x 0.4 mm, 17 faces (baked)
FEATURE [Part::Feature] Part__Feature011  label="1_27mm_plastic_for_pin003"
  Placement = pos=(-0.452582,-1.45718,-0.233527) rot=(0,1,0;1.5708rad)
  shape: bbox 1.905 x 1 x 1.27 mm, 10 faces (baked)
FEATURE [Part::Feature] Part__Feature012  label="1_27mm_pin_right_angle004"
  Placement = pos=(-0.770082,-1.65718,-0.233527) rot=(0,0,1;0rad)
  shape: bbox 2.2 x 4.2 x 0.4 mm, 17 faces (baked)
FEATURE [Part::Feature] Part__Feature013  label="1_27mm_plastic_for_pin004"
  Placement = pos=(-0.452582,-1.45718,-0.233527) rot=(0,1,0;1.5708rad)
  shape: bbox 1.905 x 1 x 1.27 mm, 10 faces (baked)
FEATURE [Part::Feature] Part__Feature014  label="1_27mm_pin_right_angle005"
  Placement = pos=(-0.770082,-1.65718,-0.233527) rot=(0,0,1;0rad)
  shape: bbox 2.2 x 4.2 x 0.4 mm, 17 faces (baked)
FEATURE [Part::Feature] Part__Feature015  label="1_27mm_plastic_for_pin005"
  Placement = pos=(-0.452582,-1.45718,-0.233527) rot=(0,1,0;1.5708rad)
  shape: bbox 1.905 x 1 x 1.27 mm, 10 faces (baked)
FEATURE [Part::Feature] Part__Feature016  label="1_27mm_pin_right_angle006"
  Placement = pos=(-0.770082,-1.65718,-0.233527) rot=(0,0,1;0rad)
  shape: bbox 2.2 x 4.2 x 0.4 mm, 17 faces (baked)
FEATURE [Part::Feature] Part__Feature017  label="1_27mm_plastic_for_pin006"
  Placement = pos=(-0.452582,-1.45718,-0.233527) rot=(0,1,0;1.5708rad)
  shape: bbox 1.905 x 1 x 1.27 mm, 10 faces (baked)
FEATURE [Part::Feature] Part__Feature018  label="1_27mm_pin_right_angle007"
  Placement = pos=(-0.770082,-1.65718,-0.233527) rot=(0,0,1;0rad)
  shape: bbox 2.2 x 4.2 x 0.4 mm, 17 faces (baked)
FEATURE [Part::Feature] Part__Feature019  label="1_27mm_plastic_for_pin007"
  Placement = pos=(-0.452582,-1.45718,-0.233527) rot=(0,1,0;1.5708rad)
  shape: bbox 1.905 x 1 x 1.27 mm, 10 faces (baked)
FEATURE [Part::Feature] Part__Feature020  label="1_27mm_pin_right_angle008"
  Placement = pos=(-0.770082,-1.65718,-0.233527) rot=(0,0,1;0rad)
  shape: bbox 2.2 x 4.2 x 0.4 mm, 17 faces (baked)
FEATURE [Part::Feature] Part__Feature021  label="1_27mm_plastic_for_pin008"
  Placement = pos=(-0.452582,-1.45718,-0.233527) rot=(0,1,0;1.5708rad)
  shape: bbox 1.905 x 1 x 1.27 mm, 10 faces (baked)
FEATURE [Part::Feature] Part__Feature156  label="1_27mm_pin_right_angle009"
  Placement = pos=(-0.770082,-1.65718,-0.233527) rot=(0,0,1;0rad)
  shape: bbox 2.2 x 4.2 x 0.4 mm, 17 faces (baked)
FEATURE [Part::Feature] Part__Feature157  label="1_27mm_plastic_for_pin009"
  Placement = pos=(-0.452582,-1.45718,-0.233527) rot=(0,1,0;1.5708rad)
  shape: bbox 1.905 x 1 x 1.27 mm, 10 faces (baked)
FEATURE [App::Part] __27mm_single_pin_assembled  label="1_27mm_single_pin_assembled"
  Group = -> [Part__Feature004,Part__Feature005]
  Origin = -> Origin
  Placement = pos=(-0.361489,-0.21886,0.454215) rot=(0,0,1;0rad)
FEATURE [App::Part] __27mm_single_pin_assembled001  label="1_27mm_single_pin_assembled001"
  Group = -> [Part__Feature006,Part__Feature007]
  Origin = -> Origin001
  Placement = pos=(-0.361489,-0.21886,-0.795785) rot=(0,0,1;0rad)
FEATURE [App::Part] __27mm_single_pin_assembled002  label="1_27mm_single_pin_assembled002"
  Group = -> [Part__Feature008,Part__Feature009]
  Origin = -> Origin002
  Placement = pos=(-0.361489,-0.21886,-2.04579) rot=(0,0,1;0rad)
FEATURE [App::Part] __27mm_single_pin_assembled003  label="1_27mm_single_pin_assembled003"
  Group = -> [Part__Feature010,Part__Feature011]
  Origin = -> Origin003
  Placement = pos=(-0.361489,-0.21886,-3.29579) rot=(0,0,1;0rad)
FEATURE [App::Part] __27mm_single_pin_assembled004  label="1_27mm_single_pin_assembled004"
  Group = -> [Part__Feature012,Part__Feature013]
  Origin = -> Origin004
  Placement = pos=(-0.361489,-0.21886,-4.54579) rot=(0,0,1;0rad)
FEATURE [App::Part] __27mm_single_pin_assembled005  label="1_27mm_single_pin_assembled005"
  Group = -> [Part__Feature014,Part__Feature015]
  Origin = -> Origin005
  Placement = pos=(-3.17165,-0.21886,-3.76284) rot=(0,1,0;3.14159rad)
FEATURE [App::Part] __27mm_single_pin_assembled006  label="1_27mm_single_pin_assembled006"
  Group = -> [Part__Feature016,Part__Feature017]
  Origin = -> Origin006
  Placement = pos=(-3.17165,-0.21886,-5.01284) rot=(0,1,0;3.14159rad)
FEATURE [App::Part] __27mm_single_pin_assembled007  label="1_27mm_single_pin_assembled007"
  Group = -> [Part__Feature018,Part__Feature019]
  Origin = -> Origin007
  Placement = pos=(-3.17165,-0.21886,-0.0128383) rot=(0,1,0;3.14159rad)
FEATURE [App::Part] __27mm_single_pin_assembled008  label="1_27mm_single_pin_assembled008"
  Group = -> [Part__Feature020,Part__Feature021]
  Origin = -> Origin008
  Placement = pos=(-3.17165,-0.21886,-2.51284) rot=(0,1,0;3.14159rad)
FEATURE [App::Part] __27mm_single_pin_assembled009  label="1_27mm_single_pin_assembled009"
  Group = -> [Part__Feature156,Part__Feature157]
  Origin = -> Origin009
  Placement = pos=(-3.17165,-0.21886,-1.26284) rot=(0,1,0;3.14159rad)
FEATURE [App::Part] __27mm_2x10pin  label="1_27mm_2x10pin"
  Group = -> [__27mm_single_pin_assembled,__27mm_single_pin_assembled001,__27mm_single_pin_assembled002,__27mm_single_pin_assembled003,__27mm_single_pin_assembled004,__27mm_single_pin_assembled005,__27mm_single_pin_assembled006,__27mm_single_pin_assembled007,__27mm_single_pin_assembled008,__27mm_single_pin_assembled009]
  Origin = -> Origin010
  Placement = pos=(18.0516,5.67069,10.176) rot=(1,0,0;1.5708rad)
FEATURE [App::Part] pms7003
  Group = -> [Part__Feature155,Part__Feature001,Part__Feature002,Part__Feature003,__27mm_2x10pin]
  Origin = -> Origin011
  Placement = pos=(2,-286.5,-118) rot=(1,0,0;1.5708rad)
FEATURE [Part::Feature] Part__Feature158  label="SCD30"
  Placement = pos=(1.25,-320,-110) rot=(0,1,0;3.14159rad)
  shape: bbox 35.11 x 7.027 x 23.02 mm, 2292 faces, 25 solids (baked)
FEATURE [Part::Feature] Part__Feature169  label="COZIR"
  Placement = pos=(5.41,2.98,10) rot=(0,0,1;0rad)
  shape: bbox 51.61 x 17 x 50.23 mm, 43 faces (baked)
FEATURE [Part::Feature] Part__Feature170  label="COMPOUND004"
  shape: bbox 3.14 x 5 x 10.76 mm, 60 faces, 10 solids (baked)
FEATURE [App::Part] COZIR_Sensor_v2  label="COZIR Sensor v2"
  Group = -> [Part__Feature169,Part__Feature170]
  Origin = -> Origin022
  Placement = pos=(53.75,-287.25,-104.75) rot=(0,0,1;0rad)
FEATURE [Part::Feature] Part__Feature171  label="cozIRBlink"
  Placement = pos=(0,-264.25,-92) rot=(0,0,1;0rad)
  shape: bbox 21.06 x 9.056 x 38.62 mm, 1727 faces (baked)
FEATURE [Part::Cylinder] Cylinder153  label="SJH-5XD"
  Angle = 360
  AttacherType = Attacher::AttachEngine3D
  FirstAngle = 0
  Height = 19
  Placement = pos=(38,-285,-115) rot=(0,0,1;0rad)
  Radius = 10
  SecondAngle = 0
FEATURE [Part::Feature] Part__Feature172  label="SOLID006"
  shape: bbox 14.22 x 14.22 x 8 mm, 4 faces (baked)
FEATURE [Part::Feature] Part__Feature173  label="COMPOUND005"
  shape: bbox 19 x 19 x 10.5 mm, 41 faces, 0 solids (baked)
FEATURE [App::Part] Document  label="SO2LowCost"
  Group = -> [Part__Feature172,Part__Feature173]
  Origin = -> Origin023
  Placement = pos=(-38,-285,-115) rot=(0,0,1;0rad)
FEATURE [Part::Feature] Part__Feature174  label="SOLID007"
  shape: bbox 1 x 0.5 x 0.5 mm, 28 faces (baked)
FEATURE [App::Part] C_0402_1005Metric002
  Group = -> [Part__Feature174]
  Origin = -> Origin024
  Placement = pos=(120.904,-86.868,1.65) rot=(0,0,1;0rad)
FEATURE [Part::Feature] Part__Feature175  label="COMPOUND006"
  shape: bbox 2.998 x 2.998 x 0.9931 mm, 45 faces, 8 solids (baked)
FEATURE [Part::Feature] Part__Feature176  label="COMPOUND007"
  shape: bbox 6 x 2.96 x 4.95 mm, 229 faces, 7 solids (baked)
FEATURE [Part::Feature] Part__Feature177  label="COMPOUND008"
  shape: bbox 6 x 2.96 x 4.95 mm, 229 faces, 7 solids (baked)
FEATURE [Part::Feature] Part__Feature178  label="SOLID008"
  shape: bbox 1 x 0.5 x 0.5 mm, 28 faces (baked)
FEATURE [App::Part] C_0402_1005Metric003
  Group = -> [Part__Feature178]
  Origin = -> Origin028
  Placement = pos=(124.968,-87.376,1.65) rot=(0,0,-1;1.5708rad)
FEATURE [Part::Feature] Part__Feature179  label="SOLID009"
  shape: bbox 0.65 x 0.35 x 0.2 mm, 24 faces (baked)
FEATURE [App::Part] LED_0201_0603Metric001
  Group = -> [Part__Feature179]
  Origin = -> Origin029
  Placement = pos=(117.196,-81.5848,1.65) rot=(0,0,1;0rad)
FEATURE [Part::Feature] Part__Feature180  label="SOLID010"
  shape: bbox 2.54 x 10.16 x 11.54 mm, 100 faces (baked)
FEATURE [Part::Feature] Part__Feature181  label="SOLID011"
  shape: bbox 1 x 0.5 x 0.35 mm, 26 faces (baked)
FEATURE [Part::Feature] Part__Feature182  label="SOLID012"
  shape: bbox 1 x 2 x 0.45 mm, 140 faces (baked)
FEATURE [Part::Feature] Part__Feature183  label="COMPOUND009"
  shape: bbox 25.4 x 17.78 x 1.6 mm, 31 faces (baked)
FEATURE [App::Part] PinHeader_1x04_P2_54mm_Vertical001  label="PinHeader_1x04_P2.54mm_Vertical001"
  Group = -> [Part__Feature180]
  Origin = -> Origin030
  Placement = pos=(120.904,-91.2114,-0.05) rot=(-0.707107,0.707107,0;3.14159rad)
FEATURE [App::Part] R_0402_1005Metric001
  Group = -> [Part__Feature181]
  Origin = -> Origin031
  Placement = pos=(119.634,-84.328,1.65) rot=(0,0,1;1.5708rad)
FEATURE [App::Part] R_Array_Concave_4x0403
  Group = -> [Part__Feature182]
  Origin = -> Origin032
  Placement = pos=(129.642,-85.3186,1.65) rot=(0,0,1;0rad)
FEATURE [App::Part] SENSOR_AHT20_GAE001
  Group = -> [Part__Feature175]
  Origin = -> Origin025
  Placement = pos=(125.019,-83.8708,1.65) rot=(0,0,1;0rad)
FEATURE [App::Part] SM04B_SRSS_TB_LF__SN_002  label="SM04B-SRSS-TB_LF__SN_002"
  Group = -> [Part__Feature176]
  Origin = -> Origin026
  Placement = pos=(132.732,-85.8012,1.15) rot=(0.57735,0.57735,0.57735;2.0944rad)
FEATURE [App::Part] SM04B_SRSS_TB_LF__SN_003  label="SM04B-SRSS-TB_LF__SN_003"
  Group = -> [Part__Feature177]
  Origin = -> Origin027
  Placement = pos=(116.391,-85.8266,1.15) rot=(-0.57735,0.57735,0.57735;4.18879rad)
FEATURE [App::Part] Open_CASCADE_STEP_translator_6_9_002  label="TMP117"
  Group = -> [C_0402_1005Metric002,SENSOR_AHT20_GAE001,SM04B_SRSS_TB_LF__SN_002,SM04B_SRSS_TB_LF__SN_003,C_0402_1005Metric003,LED_0201_0603Metric001,PinHeader_1x04_P2_54mm_Vertical001,R_0402_1005Metric001,R_Array_Concave_4x0403,Part__Feature183]
  Origin = -> Origin033
  Placement = pos=(-125,-330,36.25) rot=(-1,0,0;4.71239rad)
FEATURE [Part::Feature] Part__Feature184  label="SOLID013"
  shape: bbox 1 x 0.5 x 0.5 mm, 28 faces (baked)
FEATURE [App::Part] C_0402_1005Metric004
  Group = -> [Part__Feature184]
  Origin = -> Origin034
  Placement = pos=(120.904,-86.868,1.65) rot=(0,0,1;0rad)
FEATURE [Part::Feature] Part__Feature185  label="COMPOUND010"
  shape: bbox 2.998 x 2.998 x 0.9931 mm, 45 faces, 8 solids (baked)
FEATURE [Part::Feature] Part__Feature186  label="COMPOUND011"
  shape: bbox 6 x 2.96 x 4.95 mm, 229 faces, 7 solids (baked)
FEATURE [Part::Feature] Part__Feature187  label="COMPOUND012"
  shape: bbox 6 x 2.96 x 4.95 mm, 229 faces, 7 solids (baked)
FEATURE [Part::Feature] Part__Feature188  label="SOLID014"
  shape: bbox 1 x 0.5 x 0.5 mm, 28 faces (baked)
FEATURE [App::Part] C_0402_1005Metric005
  Group = -> [Part__Feature188]
  Origin = -> Origin038
  Placement = pos=(124.968,-87.376,1.65) rot=(0,0,-1;1.5708rad)
FEATURE [Part::Feature] Part__Feature189  label="SOLID015"
  shape: bbox 0.65 x 0.35 x 0.2 mm, 24 faces (baked)
FEATURE [App::Part] LED_0201_0603Metric002
  Group = -> [Part__Feature189]
  Origin = -> Origin039
  Placement = pos=(117.196,-81.5848,1.65) rot=(0,0,1;0rad)
FEATURE [Part::Feature] Part__Feature190  label="SOLID016"
  shape: bbox 2.54 x 10.16 x 11.54 mm, 100 faces (baked)
FEATURE [Part::Feature] Part__Feature191  label="SOLID017"
  shape: bbox 1 x 0.5 x 0.35 mm, 26 faces (baked)
FEATURE [Part::Feature] Part__Feature192  label="SOLID018"
  shape: bbox 1 x 2 x 0.45 mm, 140 faces (baked)
FEATURE [Part::Feature] Part__Feature193  label="COMPOUND013"
  shape: bbox 25.4 x 17.78 x 1.6 mm, 31 faces (baked)
FEATURE [App::Part] PinHeader_1x04_P2_54mm_Vertical002  label="PinHeader_1x04_P2.54mm_Vertical002"
  Group = -> [Part__Feature190]
  Origin = -> Origin040
  Placement = pos=(120.904,-91.2114,-0.05) rot=(-0.707107,0.707107,0;3.14159rad)
FEATURE [App::Part] R_0402_1005Metric002
  Group = -> [Part__Feature191]
  Origin = -> Origin041
  Placement = pos=(119.634,-84.328,1.65) rot=(0,0,1;1.5708rad)
FEATURE [App::Part] R_Array_Concave_4x0404
  Group = -> [Part__Feature192]
  Origin = -> Origin042
  Placement = pos=(129.642,-85.3186,1.65) rot=(0,0,1;0rad)
FEATURE [App::Part] SENSOR_AHT20_GAE002
  Group = -> [Part__Feature185]
  Origin = -> Origin035
  Placement = pos=(125.019,-83.8708,1.65) rot=(0,0,1;0rad)
FEATURE [App::Part] SM04B_SRSS_TB_LF__SN_004  label="SM04B-SRSS-TB_LF__SN_004"
  Group = -> [Part__Feature186]
  Origin = -> Origin036
  Placement = pos=(132.732,-85.8012,1.15) rot=(0.57735,0.57735,0.57735;2.0944rad)
FEATURE [App::Part] SM04B_SRSS_TB_LF__SN_005  label="SM04B-SRSS-TB_LF__SN_005"
  Group = -> [Part__Feature187]
  Origin = -> Origin037
  Placement = pos=(116.391,-85.8266,1.15) rot=(-0.57735,0.57735,0.57735;4.18879rad)
FEATURE [App::Part] Open_CASCADE_STEP_translator_6_9_003  label="LPS22"
  Group = -> [C_0402_1005Metric004,SENSOR_AHT20_GAE002,SM04B_SRSS_TB_LF__SN_004,SM04B_SRSS_TB_LF__SN_005,C_0402_1005Metric005,LED_0201_0603Metric002,PinHeader_1x04_P2_54mm_Vertical002,R_0402_1005Metric002,R_Array_Concave_4x0404,Part__Feature193]
  Origin = -> Origin043
  Placement = pos=(-125,-301,36.25) rot=(-1,0,0;4.71239rad)
FEATURE [Part::Feature] Part__Feature194  label="SOLID019"
  shape: bbox 1 x 0.5 x 0.5 mm, 28 faces (baked)
FEATURE [App::Part] C_0402_1005Metric006
  Group = -> [Part__Feature194]
  Origin = -> Origin044
  Placement = pos=(120.904,-86.868,1.65) rot=(0,0,1;0rad)
FEATURE [Part::Feature] Part__Feature195  label="COMPOUND014"
  shape: bbox 2.998 x 2.998 x 0.9931 mm, 45 faces, 8 solids (baked)
FEATURE [Part::Feature] Part__Feature196  label="COMPOUND015"
  shape: bbox 6 x 2.96 x 4.95 mm, 229 faces, 7 solids (baked)
FEATURE [Part::Feature] Part__Feature197  label="COMPOUND016"
  shape: bbox 6 x 2.96 x 4.95 mm, 229 faces, 7 solids (baked)
FEATURE [Part::Feature] Part__Feature198  label="SOLID020"
  shape: bbox 1 x 0.5 x 0.5 mm, 28 faces (baked)
FEATURE [App::Part] C_0402_1005Metric007
  Group = -> [Part__Feature198]
  Origin = -> Origin048
  Placement = pos=(124.968,-87.376,1.65) rot=(0,0,-1;1.5708rad)
FEATURE [Part::Feature] Part__Feature199  label="SOLID021"
  shape: bbox 0.65 x 0.35 x 0.2 mm, 24 faces (baked)
FEATURE [App::Part] LED_0201_0603Metric003
  Group = -> [Part__Feature199]
  Origin = -> Origin049
  Placement = pos=(117.196,-81.5848,1.65) rot=(0,0,1;0rad)
FEATURE [Part::Feature] Part__Feature200  label="SOLID022"
  shape: bbox 2.54 x 10.16 x 11.54 mm, 100 faces (baked)
FEATURE [Part::Feature] Part__Feature201  label="SOLID023"
  shape: bbox 1 x 0.5 x 0.35 mm, 26 faces (baked)
FEATURE [Part::Feature] Part__Feature202  label="SOLID024"
  shape: bbox 1 x 2 x 0.45 mm, 140 faces (baked)
FEATURE [Part::Feature] Part__Feature203  label="COMPOUND017"
  shape: bbox 25.4 x 17.78 x 1.6 mm, 31 faces (baked)
FEATURE [App::Part] PinHeader_1x04_P2_54mm_Vertical003  label="PinHeader_1x04_P2.54mm_Vertical003"
  Group = -> [Part__Feature200]
  Origin = -> Origin050
  Placement = pos=(120.904,-91.2114,-0.05) rot=(-0.707107,0.707107,0;3.14159rad)
FEATURE [App::Part] R_0402_1005Metric003
  Group = -> [Part__Feature201]
  Origin = -> Origin051
  Placement = pos=(119.634,-84.328,1.65) rot=(0,0,1;1.5708rad)
FEATURE [App::Part] R_Array_Concave_4x0405
  Group = -> [Part__Feature202]
  Origin = -> Origin052
  Placement = pos=(129.642,-85.3186,1.65) rot=(0,0,1;0rad)
FEATURE [App::Part] SENSOR_AHT20_GAE003
  Group = -> [Part__Feature195]
  Origin = -> Origin045
  Placement = pos=(125.019,-83.8708,1.65) rot=(0,0,1;0rad)
FEATURE [App::Part] SM04B_SRSS_TB_LF__SN_006  label="SM04B-SRSS-TB_LF__SN_006"
  Group = -> [Part__Feature196]
  Origin = -> Origin046
  Placement = pos=(132.732,-85.8012,1.15) rot=(0.57735,0.57735,0.57735;2.0944rad)
FEATURE [App::Part] SM04B_SRSS_TB_LF__SN_007  label="SM04B-SRSS-TB_LF__SN_007"
  Group = -> [Part__Feature197]
  Origin = -> Origin047
  Placement = pos=(116.391,-85.8266,1.15) rot=(-0.57735,0.57735,0.57735;4.18879rad)
FEATURE [App::Part] Open_CASCADE_STEP_translator_6_9_004  label="SHT40"
  Group = -> [C_0402_1005Metric006,SENSOR_AHT20_GAE003,SM04B_SRSS_TB_LF__SN_006,SM04B_SRSS_TB_LF__SN_007,C_0402_1005Metric007,LED_0201_0603Metric003,PinHeader_1x04_P2_54mm_Vertical003,R_0402_1005Metric003,R_Array_Concave_4x0405,Part__Feature203]
  Origin = -> Origin053
  Placement = pos=(-125,-278,36.25) rot=(-1,0,0;4.71239rad)
FEATURE [Part::Extrusion] Extrude034  label="logoPanel002"
  Base = -> Sketch
  Dir = (0,0,1)
  DirMode = 2
  FaceMakerClass = Part::FaceMakerBullseye
  LengthFwd = 38
  LengthRev = 0
  Solid = true
  Symmetric = false
FEATURE [Sketcher::SketchObject] Sketch131
  FullyConstrained = true
FEATURE [Sketcher::SketchObject] Sketch132  label="SketchBottom017"
  FullyConstrained = true
  Placement = pos=(0,0,-126) rot=(0,0,1;0rad)
  sketch-geometry (6):
    g0: LineSegment StartX=37.5 StartY=-351.614 StartZ=0 EndX=60.6763 EndY=-280.285 EndZ=0
    g1: LineSegment StartX=60.6763 StartY=-280.285 StartZ=0 EndX=0 EndY=-236.201 EndZ=0
    g2: LineSegment StartX=0 StartY=-236.201 StartZ=0 EndX=-60.6763 EndY=-280.285 EndZ=0
    g3: LineSegment StartX=-60.6763 StartY=-280.285 StartZ=0 EndX=-37.5 EndY=-351.614 EndZ=0
    g4: LineSegment StartX=-37.5 StartY=-351.614 StartZ=0 EndX=37.5 EndY=-351.614 EndZ=0
    g5: Circle CenterX=0 CenterY=-300 CenterZ=0 NormalX=0 NormalY=0 NormalZ=1 AngleXU=0 Radius=63.7988
  constraints (15):
    c: Coincident(g0,g1)
    c: Coincident(g1,g2)
    c: Coincident(g2,g3)
    c: Coincident(g3,g4)
    c: Coincident(g4,g0)
    c: Equal(g0, g1-g4) x4
    c: PointOnObject(g0,g5)
    c: PointOnObject(g1,g5)
    c: PointOnObject(g2,g5)
    c: PointOnObject(g3,g5)
    c: PointOnObject(g4,g5)
    c: Horizontal(g4)
    c: DistanceX(g4,g4) = 75
    c: DistanceX(g5) = 0
    c: DistanceY(g5) = -300
FEATURE [Part::Extrusion] Extrude036  label="legPart1"
  Base = -> Sketch132
  Dir = (0,0,1)
  DirMode = 2
  FaceMakerClass = Part::FaceMakerBullseye
  LengthFwd = 110
  LengthRev = 0
  Solid = true
  Symmetric = false
FEATURE [Sketcher::SketchObject] Sketch133  label="SketchBottom018"
  FullyConstrained = true
  Placement = pos=(0,0,-126) rot=(0,0,1;0rad)
  sketch-geometry (2):
    g0: Circle CenterX=0 CenterY=-300 CenterZ=0 NormalX=0 NormalY=0 NormalZ=1 AngleXU=0 Radius=63.8
    g1: Circle CenterX=0 CenterY=-300 CenterZ=0 NormalX=0 NormalY=0 NormalZ=1 AngleXU=0 Radius=55
  constraints (5):
    c: Diameter(g1) = 110
    c: Diameter(g0) = 127.6
    c: DistanceY(g0) = -300
    c: DistanceX(g0) = 0
    c: Coincident(g0,g1)
FEATURE [Part::Extrusion] Extrude037  label="legPart002"
  Base = -> Sketch133
  Dir = (0,0,1)
  DirMode = 2
  FaceMakerClass = Part::FaceMakerBullseye
  LengthFwd = 110
  LengthRev = 0
  Solid = true
  Symmetric = false
FEATURE [Part::MultiCommon] Common  label="legs"
  Shapes = -> [Extrude037,Extrude036]
FEATURE [Part::Extrusion] Extrude035  label="srsCut"
  Base = -> Sketch130
  Dir = (0,0,1)
  DirMode = 2
  FaceMakerClass = Part::FaceMakerBullseye
  LengthFwd = 38
  LengthRev = 0
  Solid = true
  Symmetric = false
FEATURE [Part::MultiFuse] Fusion  label="logoLevels"
  Shapes = -> [Fillet050,Fillet054]
FEATURE [Part::Cut] Cut051  label="srsLogoLevels"
  Base = -> Fusion
  Tool = -> Extrude035
FEATURE [Part::MultiFuse] Fusion093  label="legeLevels"
  Shapes = -> [Cut051,Extrude034]
FEATURE [Part::Cut] Cut052  label="srsLogoLevels001"
  Base = -> Fusion093
  Tool = -> Part__Feature154
FEATURE [Part::MultiFuse] Fusion094  label="srsPentagon"
  Shapes = -> [Cut052,Fillet058,Fillet046,Fillet042,Fillet038,Fillet034,Common,Extrude]
FEATURE [Sketcher::SketchObject] Sketch134
  FullyConstrained = true
  Placement = pos=(0,-234,0) rot=(1,0,0;1.5708rad)
  sketch-geometry (8):
    g0: LineSegment StartX=-13 StartY=10 StartZ=0 EndX=13 EndY=10 EndZ=0
    g1: LineSegment StartX=13 StartY=10 StartZ=0 EndX=13 EndY=-16 EndZ=0
    g2: LineSegment StartX=13 StartY=-16 StartZ=0 EndX=-13 EndY=-16 EndZ=0
    g3: LineSegment StartX=-13 StartY=-16 StartZ=0 EndX=-13 EndY=10 EndZ=0
    g4: LineSegment StartX=-20 StartY=-20 StartZ=0 EndX=-20 EndY=17 EndZ=0
    g5: LineSegment StartX=-20 StartY=17 StartZ=0 EndX=20 EndY=17 EndZ=0
    g6: LineSegment StartX=20 StartY=17 StartZ=0 EndX=20 EndY=-20 EndZ=0
    g7: LineSegment StartX=-20 StartY=-20 StartZ=0 EndX=20 EndY=-20 EndZ=0
  constraints (24):
    c: Coincident(g0,g1)
    c: Coincident(g1,g2)
    c: Coincident(g2,g3)
    c: Coincident(g3,g0)
    c: Horizontal(g0)
    c: Horizontal(g2)
    c: Vertical(g1)
    c: Vertical(g3)
    c: DistanceY(g2,g0) = 26
    c: DistanceX(g0,g0) = 26
    c: DistanceX(g0) = -13
    c: Vertical(g4)
    c: Coincident(g5,g4)
    c: Horizontal(g5)
    c: DistanceX(g4,g0) = 7
    c: DistanceY(g0,g4) = 7
    c: DistanceX(g0,g5) = 7
    c: DistanceY(g4) = -20
    c: Coincident(g6,g5)
    c: Vertical(g6)
    c: Coincident(g7,g4)
    c: Coincident(g7,g6)
    c: Horizontal(g7)
    c: DistanceY(g2) = -16
FEATURE [Part::Extrusion] Extrude038  label="tSlotHold"
  Base = -> Sketch134
  Dir = (0,-1,2e-16)
  DirMode = 2
  FaceMakerClass = Part::FaceMakerBullseye
  LengthFwd = 45
  LengthRev = 0
  Solid = true
  Symmetric = false
FEATURE [Part::Feature] Part__Feature204  label="PH Pan head screw M2x0.40 x 6"
  Placement = pos=(101.945,-83.8381,-1.82512) rot=(0,0,1;3.14159rad)
  shape: bbox 4.006 x 4.006 x 7.57 mm, 32 faces (baked)
FEATURE [Part::Feature] Part__Feature205  label="Part 8"
  Placement = pos=(178.445,24.1619,-39.4251) rot=(0,1,0;3.14159rad)
  shape: bbox 166 x 27.4 x 2 mm, 14 faces (baked)
FEATURE [Part::Feature] Part__Feature206  label="event gore PMF100320"
  Placement = pos=(79.1369,-76.58,11.5741) rot=(0,-1,0;0.037482rad)
  shape: bbox 2.468 x 15.31 x 15.29 mm, 4 faces (baked)
FEATURE [Part::Feature] Part__Feature207  label="event gore PMF100321"
  Placement = pos=(79.1369,-76.58,11.5741) rot=(0,-1,0;0.037482rad)
  shape: bbox 15.95 x 18.27 x 18.26 mm, 114 faces (baked)
FEATURE [Part::Feature] Part__Feature208  label="PH Pan head screw M2x0.40 x 007"
  Placement = pos=(101.945,24.1619,-1.82512) rot=(0,0,1;0rad)
  shape: bbox 4.006 x 4.006 x 7.57 mm, 32 faces (baked)
FEATURE [Part::Feature] Part__Feature209  label="WPB20-28-7_3D"
  Placement = pos=(178.445,24.1619,30.5749) rot=(0,0,1;0rad)
  shape: bbox 200.6 x 280.6 x 46.01 mm, 1035 faces (baked)
FEATURE [Part::Feature] Part__Feature210  label="PH Pan head screw M2x0.40 x 008"
  Placement = pos=(254.945,-83.8381,-1.82512) rot=(0,0,1;3.14159rad)
  shape: bbox 4.006 x 4.006 x 7.57 mm, 32 faces (baked)
FEATURE [Part::Feature] Part__Feature211  label="Cable Gland PG7-PG19 Lock Nut_PG13.5"
  Placement = pos=(223.445,-112.627,11.6686) rot=(1,0,0;0.037482rad)
  shape: bbox 29.02 x 6.449 x 29 mm, 29 faces (baked)
FEATURE [Part::Feature] Part__Feature212  label="Cable Gland PG7-PG19 Body_PG13.5"
  Placement = pos=(223.445,-118.923,11.4325) rot=(0,-0.01874,0.999824;3.14159rad)
  shape: bbox 25.06 x 36.36 x 23.18 mm, 156 faces (baked)
FEATURE [Part::Feature] Part__Feature213  label="Cable Gland PG7-PG19 Washer_PG13.5"
  Placement = pos=(223.445,-115.725,11.5524) rot=(0,-0.01874,0.999824;3.14159rad)
  shape: bbox 25 x 2.136 x 25.03 mm, 4 faces (baked)
FEATURE [Part::Feature] Part__Feature214  label="Cable Gland PG7-PG19 Gland Nut_PG13.5"
  Placement = pos=(223.445,-132.014,10.9416) rot=(0.825324,-0.010582,0.56456;3.17253rad)
  shape: bbox 25.82 x 20.19 x 25.8 mm, 50 faces (baked)
FEATURE [Part::Feature] Part__Feature215  label="Cable Gland PG7-PG19 Sleeve_PG13.5"
  Placement = pos=(223.445,-137.51,10.7355) rot=(0,-0.01874,0.999824;3.14159rad)
  shape: bbox 15.7 x 8.583 x 15.99 mm, 4 faces (baked)
FEATURE [App::Part] Cable_Gland_PG7_PG19__PG13_5__1_  label="Cable Gland PG7-PG19, PG13.5 <1>"
  Group = -> [Part__Feature211,Part__Feature212,Part__Feature213,Part__Feature214,Part__Feature215]
  Origin = -> Origin054
FEATURE [Part::Feature] Part__Feature216  label="WPMB-M4-2"
  Placement = pos=(178.445,24.1619,-13.4251) rot=(0,1,0;3.14159rad)
  shape: bbox 91.99 x 91.99 x 12.05 mm, 899 faces (baked)
FEATURE [Part::Feature] Part__Feature217  label="Micro_USB_Plug v10"
  Placement = pos=(255.557,33.7719,7.31475) rot=(0.577351,0.577352,-0.577348;4.18879rad)
  shape: bbox 4.78 x 0.2 x 0.4672 mm, 14 faces (baked)
FEATURE [Part::Feature] Part__Feature218  label="Micro_USB_Plug_Connector"
  Placement = pos=(255.557,33.7719,7.31475) rot=(0.577351,0.577352,-0.577348;4.18879rad)
  shape: bbox 7.5 x 6.85 x 1.85 mm, 68 faces (baked)
FEATURE [Part::Feature] Part__Feature219  label="Micro_USB_Plug v011"
  Placement = pos=(255.557,33.7719,7.31475) rot=(0.577351,0.577352,-0.577348;4.18879rad)
  shape: bbox 4.78 x 0.2 x 0.4672 mm, 14 faces (baked)
FEATURE [Part::Feature] Part__Feature220  label="Micro_USB_Plug_Connector001"
  Placement = pos=(255.557,33.7719,7.31475) rot=(0.577351,0.577352,-0.577348;4.18879rad)
  shape: bbox 4.574 x 0.32 x 1.625 mm, 11 faces (baked)
FEATURE [Part::Feature] Part__Feature221  label="micro_usb_plug rt angle"
  Placement = pos=(255.557,33.7719,7.31475) rot=(0.577351,0.577352,-0.577348;4.18879rad)
  shape: bbox 12.25 x 19.75 x 7.006 mm, 151 faces (baked)
FEATURE [Part::Feature] Part__Feature222  label="Micro_USB_Plug v012"
  Placement = pos=(255.557,33.7719,7.31475) rot=(0.577351,0.577352,-0.577348;4.18879rad)
  shape: bbox 4.78 x 0.2 x 0.4672 mm, 14 faces (baked)
FEATURE [Part::Feature] Part__Feature223  label="Micro_USB_Plug v013"
  Placement = pos=(255.557,33.7719,7.31475) rot=(0.577351,0.577352,-0.577348;4.18879rad)
  shape: bbox 4.78 x 0.2 x 0.4672 mm, 14 faces (baked)
FEATURE [Part::Feature] Part__Feature224  label="Wire"
  Placement = pos=(255.557,33.7719,7.31475) rot=(0.577351,0.577352,-0.577348;4.18879rad)
  shape: bbox 3.2 x 9.5 x 3.2 mm, 3 faces (baked)
FEATURE [Part::Feature] Part__Feature225  label="Micro_USB_Plug_Connector002"
  Placement = pos=(255.557,33.7719,7.31475) rot=(0.577351,0.577352,-0.577348;4.18879rad)
  shape: bbox 4.7 x 0.32 x 1.625 mm, 11 faces (baked)
FEATURE [Part::Feature] Part__Feature226  label="Micro_USB_Plug v014"
  Placement = pos=(255.557,33.7719,7.31475) rot=(0.577351,0.577352,-0.577348;4.18879rad)
  shape: bbox 4.78 x 0.2 x 0.4672 mm, 14 faces (baked)
FEATURE [Part::Feature] Part__Feature227  label="Micro_USB_Plug_Connector003"
  Placement = pos=(255.557,33.7719,7.31475) rot=(0.577351,0.577352,-0.577348;4.18879rad)
  shape: bbox 7.5 x 6.35 x 1.35 mm, 54 faces (baked)
FEATURE [Part::Feature] Part__Feature228  label="2_C_3_4_6_1_1"
  Placement = pos=(205.099,-19.2281,8.57488) rot=(-1,-3e-06,-3e-06;1.57079rad)
  shape: bbox 73.52 x 148.2 x 33.63 mm, 876 faces (baked)
FEATURE [Part::Feature] Part__Feature025  label="2_BAT_3_4_6_1_1"
  Placement = pos=(205.099,-19.2281,8.57488) rot=(-1,-3e-06,-3e-06;1.57079rad)
  shape: bbox 14.36 x 15.32 x 64.97 mm, 83 faces (baked)
FEATURE [Part::Feature] Part__Feature026  label="2_B_3_4_6_1_1"
  Placement = pos=(205.099,-19.2281,8.57488) rot=(-1,-3e-06,-3e-06;1.57079rad)
  shape: bbox 78.1 x 152 x 64.86 mm, 1086 faces (baked)
FEATURE [Part::Feature] Part__Feature027  label="2_A_3_4_6_2_1"
  Placement = pos=(205.099,-19.2281,8.57488) rot=(-1,-3e-06,-3e-06;1.57079rad)
  shape: bbox 73.51 x 148.2 x 58.23 mm, 268 faces (baked)
FEATURE [Part::Feature] Part__Feature028  label="PH Pan head screw M2x0.40 x 009"
  Placement = pos=(254.945,24.1619,-1.82512) rot=(0,0,1;0rad)
  shape: bbox 4.006 x 4.006 x 7.57 mm, 32 faces (baked)
FEATURE [Part::Feature] Part__Feature029  label="Part 009"
  Placement = pos=(178.445,-83.8381,-39.4251) rot=(1,0,0;3.14159rad)
  shape: bbox 166 x 27.4 x 2 mm, 14 faces (baked)
FEATURE [Part::Feature] Part__Feature030  label="WPC20-28_3D"
  Placement = pos=(178.435,24.1794,31.5749) rot=(0,0,1;0rad)
  shape: bbox 201.1 x 281.1 x 21.57 mm, 1217 faces (baked)
FEATURE [Part::Feature] Part__Feature031  label="Cable Gland PG7-PG19 Sleeve_PG9"
  Placement = pos=(133.445,-133.413,10.8891) rot=(0,-0.01874,0.999824;3.14159rad)
  shape: bbox 11 x 8.207 x 11.28 mm, 4 faces (baked)
FEATURE [Part::Feature] Part__Feature032  label="Cable Gland PG7-PG19 Washer_PG9"
  Placement = pos=(133.445,-115.725,11.5524) rot=(0,-0.01874,0.999824;3.14159rad)
  shape: bbox 19.7 x 1.937 x 19.73 mm, 4 faces (baked)
FEATURE [Part::Feature] Part__Feature033  label="Cable Gland PG7-PG19 Lock Nut_PG9"
  Placement = pos=(133.445,-112.627,11.6686) rot=(1,0,0;0.037482rad)
  shape: bbox 24.34 x 6.322 x 24.32 mm, 29 faces (baked)
FEATURE [Part::Feature] Part__Feature034  label="Cable Gland PG7-PG19 Body_PG9"
  Placement = pos=(133.445,-118.823,11.4362) rot=(0,-0.01874,0.999824;3.14159rad)
  shape: bbox 19.4 x 32.49 x 17.68 mm, 129 faces (baked)
FEATURE [Part::Feature] Part__Feature035  label="Cable Gland PG7-PG19 Gland Nut_PG9"
  Placement = pos=(133.445,-130.065,11.0147) rot=(0.825324,-0.010582,0.56456;3.17253rad)
  shape: bbox 20.81 x 16.04 x 20.8 mm, 48 faces (baked)
FEATURE [App::Part] Cable_Gland_PG7_PG19__PG9__1_  label="Cable Gland PG7-PG19, PG9 <1>"
  Group = -> [Part__Feature031,Part__Feature032,Part__Feature033,Part__Feature034,Part__Feature035]
  Origin = -> Origin056
FEATURE [Part::Feature] Part__Feature036  label="id2"
  shape: bbox 274 x 229.5 x 2.5 mm, 53 faces (baked)
FEATURE [Part::Feature] Part__Feature037  label="id5"
  shape: bbox 251.2 x 70.58 x 83.44 mm, 48 faces (baked)
FEATURE [Part::Feature] Part__Feature038  label="id8"
  shape: bbox 253.5 x 2.737 x 2.883 mm, 6 faces (baked)
FEATURE [Part::MultiFuse] Fusion095  label="solarPanelMount"
  Placement = pos=(0,0,0) rot=(1,0,0;0.698132rad)
  Shapes = -> [Part__Feature036,Part__Feature037,Part__Feature038]
FEATURE [Part::Feature] Part__Feature039  label="Part 2"
  Placement = pos=(-0.595807,44.562,74.9733) rot=(1,0,0;3.14159rad)
  shape: bbox 272 x 434 x 1.1 mm, 24 faces (baked)
FEATURE [Part::Feature] Part__Feature041  label="id16"
  Placement = pos=(-0.595807,44.562,69.8733) rot=(0,0,1;0rad)
  shape: bbox 4 x 8.79 x 2 mm, 10 faces (baked)
FEATURE [Part::Feature] Part__Feature042  label="id21"
  Placement = pos=(-0.595807,44.562,69.8733) rot=(0,0,1;0rad)
  shape: bbox 125 x 42.28 x 0.1 mm, 8 faces (baked)
FEATURE [Part::Feature] Part__Feature043  label="id26"
  Placement = pos=(-0.595807,44.562,69.8733) rot=(0,0,1;0rad)
  shape: bbox 125 x 42.28 x 0.1 mm, 8 faces (baked)
FEATURE [Part::Feature] Part__Feature044  label="id31"
  Placement = pos=(-0.595807,44.562,69.8733) rot=(0,0,1;0rad)
  shape: bbox 4 x 8.79 x 2 mm, 10 faces (baked)
FEATURE [Part::Feature] Part__Feature045  label="id36"
  Placement = pos=(-0.595807,44.562,69.8733) rot=(0,0,1;0rad)
  shape: bbox 125 x 42.28 x 0.1 mm, 8 faces (baked)
FEATURE [Part::Feature] Part__Feature046  label="id41"
  Placement = pos=(-0.595807,44.562,69.8733) rot=(0,0,1;0rad)
  shape: bbox 4 x 4 x 2 mm, 4 faces (baked)
FEATURE [Part::Feature] Part__Feature047  label="id46"
  Placement = pos=(-0.595807,44.562,69.8733) rot=(0,0,1;0rad)
  shape: bbox 4 x 4 x 2 mm, 4 faces (baked)
FEATURE [Part::Feature] Part__Feature048  label="id51"
  Placement = pos=(-0.595807,44.562,69.8733) rot=(0,0,1;0rad)
  shape: bbox 125 x 42.28 x 0.1 mm, 8 faces (baked)
FEATURE [Part::Feature] Part__Feature229  label="id56"
  Placement = pos=(-0.595807,44.562,69.8733) rot=(0,0,1;0rad)
  shape: bbox 125 x 42.28 x 0.1 mm, 8 faces (baked)
FEATURE [Part::Feature] Part__Feature050  label="id61"
  Placement = pos=(-0.595807,44.562,69.8733) rot=(0,0,1;0rad)
  shape: bbox 4 x 4 x 2 mm, 4 faces (baked)
FEATURE [Part::Feature] Part__Feature051  label="id66"
  Placement = pos=(-0.595807,44.562,69.8733) rot=(0,0,1;0rad)
  shape: bbox 125 x 42.28 x 0.1 mm, 8 faces (baked)
FEATURE [Part::Feature] Part__Feature052  label="id71"
  Placement = pos=(-0.595807,44.562,69.8733) rot=(0,0,1;0rad)
  shape: bbox 125 x 40.44 x 0.1 mm, 6 faces (baked)
FEATURE [Part::Feature] Part__Feature053  label="id76"
  Placement = pos=(-0.595807,44.562,69.8733) rot=(0,0,1;0rad)
  shape: bbox 125 x 40.44 x 0.1 mm, 6 faces (baked)
FEATURE [Part::Feature] Part__Feature054  label="id81"
  Placement = pos=(-0.595807,44.562,69.8733) rot=(0,0,1;0rad)
  shape: bbox 125 x 42.28 x 0.1 mm, 8 faces (baked)
FEATURE [Part::Feature] Part__Feature055  label="id86"
  Placement = pos=(-0.595807,44.562,69.8733) rot=(0,0,1;0rad)
  shape: bbox 125 x 42.28 x 0.1 mm, 8 faces (baked)
FEATURE [Part::Feature] Part__Feature056  label="id91"
  Placement = pos=(-0.595807,44.562,69.8733) rot=(0,0,1;0rad)
  shape: bbox 125 x 42.28 x 0.1 mm, 8 faces (baked)
FEATURE [Part::Feature] Part__Feature057  label="id96"
  Placement = pos=(-0.595807,44.562,69.8733) rot=(0,0,1;0rad)
  shape: bbox 272 x 434 x 2 mm, 24 faces (baked)
FEATURE [Part::Feature] Part__Feature058  label="id101"
  Placement = pos=(-0.595807,44.562,69.8733) rot=(0,0,1;0rad)
  shape: bbox 125 x 42.28 x 0.1 mm, 8 faces (baked)
FEATURE [Part::Feature] Part__Feature059  label="id106"
  Placement = pos=(-0.595807,44.562,69.8733) rot=(0,0,1;0rad)
  shape: bbox 125 x 42.28 x 0.1 mm, 8 faces (baked)
FEATURE [Part::Feature] Part__Feature060  label="id111"
  Placement = pos=(-0.595807,44.562,69.8733) rot=(0,0,1;0rad)
  shape: bbox 125 x 42.28 x 0.1 mm, 8 faces (baked)
FEATURE [Part::Feature] Part__Feature061  label="id116"
  Placement = pos=(-0.595807,44.562,69.8733) rot=(0,0,1;0rad)
  shape: bbox 4 x 4 x 2 mm, 4 faces (baked)
FEATURE [Part::Feature] Part__Feature062  label="id121"
  Placement = pos=(-0.595807,44.562,69.8733) rot=(0,0,1;0rad)
  shape: bbox 4 x 4 x 2 mm, 4 faces (baked)
FEATURE [Part::Feature] Part__Feature063  label="id126"
  Placement = pos=(-0.595807,44.562,69.8733) rot=(0,0,1;0rad)
  shape: bbox 125 x 42.28 x 0.1 mm, 8 faces (baked)
FEATURE [Part::Feature] Part__Feature064  label="id131"
  Placement = pos=(-0.595807,44.562,69.8733) rot=(0,0,1;0rad)
  shape: bbox 4 x 4 x 2 mm, 4 faces (baked)
FEATURE [Part::Feature] Part__Feature065  label="id136"
  Placement = pos=(-0.595807,44.562,69.8733) rot=(0,0,1;0rad)
  shape: bbox 125 x 40.44 x 0.1 mm, 6 faces (baked)
FEATURE [Part::Feature] Part__Feature066  label="id141"
  Placement = pos=(-0.595807,44.562,69.8733) rot=(0,0,1;0rad)
  shape: bbox 274 x 436 x 2 mm, 18 faces (baked)
FEATURE [Part::Feature] Part__Feature067  label="id146"
  Placement = pos=(-0.595807,44.562,69.8733) rot=(0,0,1;0rad)
  shape: bbox 125 x 42.28 x 0.1 mm, 8 faces (baked)
FEATURE [Part::Feature] Part__Feature068  label="id151"
  Placement = pos=(-0.595807,44.562,69.8733) rot=(0,0,1;0rad)
  shape: bbox 125 x 42.28 x 0.1 mm, 8 faces (baked)
FEATURE [Part::Feature] Part__Feature069  label="id156"
  Placement = pos=(-0.595807,44.562,69.8733) rot=(0,0,1;0rad)
  shape: bbox 125 x 42.28 x 0.1 mm, 8 faces (baked)
FEATURE [Part::Feature] Part__Feature070  label="id161"
  Placement = pos=(-0.595807,44.562,69.8733) rot=(0,0,1;0rad)
  shape: bbox 125 x 40.44 x 0.1 mm, 6 faces (baked)
FEATURE [Part::Feature] Part__Feature076  label="Part 1"
  Placement = pos=(-0.595807,44.562,74.9733) rot=(1,0,0;3.14159rad)
  shape: bbox 274 x 436 x 1.1 mm, 18 faces (baked)
FEATURE [Part::Feature] Part__Feature077  label="JBox - 30 mm"
  Placement = pos=(-50.5959,-43.7114,69.8733) rot=(0,1,0;3.14159rad)
  shape: bbox 30.01 x 30.09 x 5.866 mm, 175 faces (baked)
FEATURE [App::Part] P120  label="solarPanel"
  Group = -> [Part__Feature039,Part__Feature041,Part__Feature042,Part__Feature043,Part__Feature044,Part__Feature045,Part__Feature046,Part__Feature047,Part__Feature048,Part__Feature229,Part__Feature050,Part__Feature051,Part__Feature052,Part__Feature053,Part__Feature054,Part__Feature055,Part__Feature056,Part__Feature057,Part__Feature058,Part__Feature059,Part__Feature060,Part__Feature061,Part__Feature062,+10 more]
  Origin = -> Origin058
  Placement = pos=(0.6,-120,-180) rot=(1,0,0;0.698132rad)
FEATURE [App::Part] V75_ASM__1_  label="V75 ASM <1>"
  Group = -> [Part__Feature217,Part__Feature218,Part__Feature219,Part__Feature220,Part__Feature221,Part__Feature222,Part__Feature223,Part__Feature224,Part__Feature225,Part__Feature226,Part__Feature227,Part__Feature228,Part__Feature025,Part__Feature026,Part__Feature027]
  Origin = -> Origin055
  Placement = pos=(6,15.97,20) rot=(0,0,1;0rad)
FEATURE [App::Part] E305__20x28x7cm_  label="box"
  Group = -> [Part__Feature204,Part__Feature205,Part__Feature206,Part__Feature207,Part__Feature208,Part__Feature209,Part__Feature210,Cable_Gland_PG7_PG19__PG13_5__1_,Part__Feature216,V75_ASM__1_,Part__Feature028,Part__Feature029,Part__Feature030,Cable_Gland_PG7_PG19__PG9__1_]
  Origin = -> Origin057
  Placement = pos=(175.533,-124.11,-130.152) rot=(0,-0.939693,-0.34202;3.14159rad)
FEATURE [Part::Cylinder] Cylinder161
  Angle = 360
  AttacherType = Attacher::AttachEngine3D
  FirstAngle = 0
  Height = 10
  Placement = pos=(0,-21,0) rot=(0,0,1;0rad)
  Radius = 2
  SecondAngle = 0
FEATURE [Part::Cylinder] Cylinder162
  Angle = 360
  AttacherType = Attacher::AttachEngine3D
  FirstAngle = 0
  Height = 10
  Placement = pos=(0,-290.956,1.7236) rot=(1,0,0;0.698132rad)
  Radius = 1.63
  SecondAngle = 0
FEATURE [Part::Feature] Part__Feature230  label="ANT-868-PW-QW-UFL-BODY002"
  shape: bbox 15.69 x 84 x 15.69 mm, 56 faces (baked)
FEATURE [Part::Feature] Part__Feature231  label="Screw002"
  Placement = pos=(0,-7.05,0) rot=(0,0,1;0rad)
  shape: bbox 7.002 x 7.052 x 7.002 mm, 20 faces (baked)
FEATURE [Part::Feature] Part__Feature232  label="Ring002"
  shape: bbox 9.2 x 6 x 9.2 mm, 8 faces, 2 solids (baked)
FEATURE [Part::Compound] Compound003  label="loraAntenna001"
  Links = -> [Part__Feature232,Part__Feature230,Part__Feature231]
  Placement = pos=(-0.5,-512,-305.5) rot=(0.57735,-0.57735,-0.57735;2.0944rad)
FEATURE [Sketcher::SketchObject] Sketch136
  FullyConstrained = true
  Placement = pos=(-20,0,0) rot=(0.57735,0.57735,0.57735;2.0944rad)
  sketch-geometry (8):
    g0: LineSegment StartX=-299.827 StartY=3.70134 StartZ=0 EndX=-297.77 EndY=1.25 EndZ=0
    g1: LineSegment StartX=-297.77 StartY=1.25 StartZ=0 EndX=-279 EndY=17 EndZ=0
    g2: LineSegment StartX=-299.827 StartY=3.70134 StartZ=0 EndX=-328.073 EndY=-20 EndZ=0
    g3: LineSegment StartX=-328.073 StartY=-20 StartZ=0 EndX=-279 EndY=-20 EndZ=0
    g4: LineSegment StartX=-279 StartY=-20 StartZ=0 EndX=-279 EndY=17 EndZ=0
    g5: LineSegment StartX=-305 StartY=-10 StartZ=0 EndX=-285 EndY=-10 EndZ=0
    g6: LineSegment StartX=-285 StartY=-10 StartZ=0 EndX=-285 EndY=6.78199 EndZ=0
    g7: LineSegment StartX=-285 StartY=6.78199 StartZ=0 EndX=-305 EndY=-10 EndZ=0
  constraints (24):
    c: Coincident(g1,g0)
    c: DistanceX(g1) = -279
    c: DistanceY(g1) = 17
    c: Angle(g1,g0) = 1.5708
    c: Angle(g1) = 0.698132
    c: Distance(g0) = 3.2
    c: DistanceY(g0) = 1.25
    c: Coincident(g2,g0)
    c: DistanceY(g2) = -20
    c: Coincident(g3,g2)
    c: Horizontal(g3)
    c: Coincident(g4,g3)
    c: Coincident(g4,g1)
    c: Vertical(g4)
    c: Angle(g3,g2) = 0.698132
    c: Horizontal(g5)
    c: Coincident(g6,g5)
    c: Vertical(g6)
    c: Coincident(g7,g6)
    c: Coincident(g7,g5)
    c: DistanceY(g2,g5) = 10
    c: Angle(g5,g7) = 0.698132
    c: DistanceX(g5,g5) = 20
    c: DistanceX(g5) = -305
FEATURE [Sketcher::SketchObject] Sketch137
  FullyConstrained = true
  Placement = pos=(0,0,-20) rot=(0,0,1;0rad)
  sketch-geometry (5):
    g0: LineSegment StartX=20 StartY=-256.531 StartZ=0 EndX=20 EndY=-234 EndZ=0
    g1: LineSegment StartX=20 StartY=-234 StartZ=0 EndX=-20 EndY=-234 EndZ=0
    g2: LineSegment StartX=-20 StartY=-234 StartZ=0 EndX=-20 EndY=-256.531 EndZ=0
    g3: LineSegment StartX=-20 StartY=-256.531 StartZ=0 EndX=0 EndY=-242 EndZ=0
    g4: LineSegment StartX=0 StartY=-242 StartZ=0 EndX=20 EndY=-256.531 EndZ=0
  constraints (15):
    c: Vertical(g0)
    c: Coincident(g1,g0)
    c: Horizontal(g1)
    c: Coincident(g2,g1)
    c: Vertical(g2)
    c: Coincident(g3,g2)
    c: PointOnObject(g3,g-2)
    c: Coincident(g4,g3)
    c: Coincident(g4,g0)
    c: Angle(g3,g4) = 1.88496
    c: DistanceY(g3) = -242
    c: DistanceY(g2,g0) = 0
    c: DistanceX(g2) = -20
    c: DistanceX(g0) = 20
    c: DistanceY(g1) = -234
FEATURE [Part::Extrusion] Extrude040  label="tSllotHoldCut"
  Base = -> Sketch137
  Dir = (0,0,1)
  DirMode = 2
  FaceMakerClass = Part::FaceMakerBullseye
  LengthFwd = 37
  LengthRev = 0
  Solid = true
  Symmetric = false
FEATURE [Part::Extrusion] Extrude041  label="solarPanelMount002"
  Base = -> Sketch136
  Dir = (1,0,0)
  DirMode = 2
  FaceMakerClass = Part::FaceMakerBullseye
  LengthFwd = 40
  LengthRev = 0
  Solid = true
  Symmetric = false
FEATURE [Part::Cut] Cut056  label="tSlotHold001"
  Base = -> Extrude038
  Tool = -> Extrude040
FEATURE [Part::MultiFuse] Fusion106  label="srs"
  Shapes = -> [Fusion094,Extrude041,Cut056]
FEATURE [Part::Cylinder] Cylinder167  label="m6Cut"
  Angle = 360
  AttacherType = Attacher::AttachEngine3D
  FirstAngle = 0
  Height = 10
  Placement = pos=(0,-263.25,14.5) rot=(0,0,1;0rad)
  Radius = 5.75
  SecondAngle = 0
FEATURE [Sketcher::SketchObject] Sketch067
  FullyConstrained = true
  Placement = pos=(0,0,-20) rot=(0,0,1;0rad)
  sketch-geometry (6):
    g0: LineSegment StartX=9 StartY=-360 StartZ=0 EndX=9 EndY=-400 EndZ=0
    g1: LineSegment StartX=9 StartY=-400 StartZ=0 EndX=-9 EndY=-400 EndZ=0
    g2: Circle CenterX=0 CenterY=-390 CenterZ=0 NormalX=0 NormalY=0 NormalZ=1 AngleXU=0 Radius=3.25
    g3: Circle CenterX=0 CenterY=-371 CenterZ=0 NormalX=0 NormalY=0 NormalZ=1 AngleXU=0 Radius=3.25
    g4: LineSegment StartX=9 StartY=-360 StartZ=0 EndX=-9 EndY=-360 EndZ=0
    g5: LineSegment StartX=-9 StartY=-360 StartZ=0 EndX=-9 EndY=-400 EndZ=0
  constraints (18):
    c: Vertical(g0)
    c: Coincident(g1,g0)
    c: Horizontal(g1)
    c: Distance(g1) = 18
    c: Distance(g0) = 40
    c: DistanceY(g2,g3) = 19
    c: Radius(g2) = 3.25
    c: Radius(g3) = 3.25
    c: DistanceX(g2,g3) = 0
    c: Coincident(g4,g0)
    c: Horizontal(g4)
    c: Coincident(g5,g4)
    c: Coincident(g5,g1)
    c: Vertical(g5)
    c: DistanceX(g1,g2) = 9
    c: DistanceY(g1,g2) = 10
    c: DistanceY(g4) = -360
    c: DistanceX(g3) = 0
FEATURE [Part::Cut] Cut042  label="SLS"
  Base = -> Cut041
  Tool = -> Box042
FEATURE [Part::Cylinder] Cylinder168
  Angle = 360
  AttacherType = Attacher::AttachEngine3D
  FirstAngle = 0
  Height = 14.5
  Placement = pos=(0,0,0) rot=(0,1,0;3.14159rad)
  Radius = 35.35
  SecondAngle = 0
FEATURE [Sketcher::SketchObject] Sketch138
  FullyConstrained = true
  sketch-geometry (6):
    g0: Circle CenterX=0 CenterY=56.295 CenterZ=0 NormalX=0 NormalY=0 NormalZ=1 AngleXU=0 Radius=3.2
    g1: Circle CenterX=0 CenterY=75.345 CenterZ=0 NormalX=0 NormalY=0 NormalZ=1 AngleXU=0 Radius=3.2
    g2: LineSegment StartX=-12 StartY=84.875 StartZ=0 EndX=12 EndY=84.875 EndZ=0
    g3: LineSegment StartX=12 StartY=84.875 StartZ=0 EndX=12 EndY=0 EndZ=0
    g4: LineSegment StartX=12 StartY=0 StartZ=0 EndX=-12 EndY=0 EndZ=0
    g5: LineSegment StartX=-12 StartY=0 StartZ=0 EndX=-12 EndY=84.875 EndZ=0
  constraints (18):
    c: PointOnObject(g0,g-2)
    c: PointOnObject(g1,g-2)
    c: DistanceY(g0,g1) = 19.05
    c: Equal(g0,g1)
    c: Diameter(g0) = 6.4
    c: Coincident(g2,g3)
    c: Coincident(g3,g4)
    c: Coincident(g4,g5)
    c: Coincident(g5,g2)
    c: Horizontal(g2)
    c: Horizontal(g4)
    c: Vertical(g3)
    c: Vertical(g5)
    c: DistanceY(g1,g2) = 9.53
    c: DistanceX(g2,g2) = 24
    c: DistanceX(g2,g1) = 12
    c: DistanceY(g4,g2) = 84.875
    c: DistanceY(g4,g-1) = 0
FEATURE [Part::Extrusion] Extrude042
  Base = -> Sketch138
  Dir = (0,0,1)
  DirMode = 2
  FaceMakerClass = Part::FaceMakerBullseye
  LengthFwd = 14.5
  LengthRev = 0
  Reversed = true
  Solid = true
  Symmetric = false
FEATURE [Sketcher::SketchObject] Sketch001
  FullyConstrained = true
  Placement = pos=(0,0,-14.5) rot=(0,0,1;0rad)
  sketch-geometry (4):
    g0: LineSegment StartX=-9.58 StartY=84.875 StartZ=0 EndX=9.58 EndY=84.875 EndZ=0
    g1: LineSegment StartX=9.58 StartY=84.875 StartZ=0 EndX=9.58 EndY=35.355 EndZ=0
    g2: LineSegment StartX=9.58 StartY=35.355 StartZ=0 EndX=-9.58 EndY=35.355 EndZ=0
    g3: LineSegment StartX=-9.58 StartY=35.355 StartZ=0 EndX=-9.58 EndY=84.875 EndZ=0
  constraints (12):
    c: Coincident(g0,g1)
    c: Coincident(g1,g2)
    c: Coincident(g2,g3)
    c: Coincident(g3,g0)
    c: Horizontal(g0)
    c: Horizontal(g2)
    c: Vertical(g1)
    c: Vertical(g3)
    c: DistanceX(g0,g0) = 19.16
    c: DistanceX(g2) = -9.58
    c: DistanceY(g2) = 35.355
    c: DistanceY(g3,g3) = 49.52
FEATURE [Part::Extrusion] Extrude001
  Base = -> Sketch001
  Dir = (0,0,1)
  DirMode = 2
  FaceMakerClass = Part::FaceMakerBullseye
  LengthFwd = 10
  LengthRev = 0
  Solid = true
  Symmetric = false
FEATURE [Part::Sphere] Sphere
  Angle1 = 0
  Angle2 = 90
  Angle3 = 360
  AttacherType = Attacher::AttachEngine3D
  Radius = 35.35
FEATURE [Part::MultiFuse] Fusion107
  Shapes = -> [Sphere,Extrude042,Cylinder168]
FEATURE [Part::Cut] Cut057  label="rg15"
  Base = -> Fusion107
  Placement = pos=(0,-450,-5.5) rot=(0,0,1;0rad)
  Tool = -> Extrude001
FEATURE [Sketcher::SketchObject] Sketch139
  FullyConstrained = true
  Placement = pos=(0,0,-20) rot=(0,0,1;0rad)
  sketch-geometry (6):
    g0: LineSegment StartX=-9.25 StartY=-279 StartZ=0 EndX=9.25 EndY=-279 EndZ=0
    g1: LineSegment StartX=9.25 StartY=-279 StartZ=0 EndX=9.25 EndY=-403 EndZ=0
    g2: LineSegment StartX=9.25 StartY=-403 StartZ=0 EndX=-9.25 EndY=-403 EndZ=0
    g3: LineSegment StartX=-9.25 StartY=-403 StartZ=0 EndX=-9.25 EndY=-279 EndZ=0
    g4: Circle CenterX=0 CenterY=-393.7 CenterZ=0 NormalX=0 NormalY=0 NormalZ=1 AngleXU=0 Radius=3.5
    g5: Circle CenterX=0 CenterY=-374.65 CenterZ=0 NormalX=0 NormalY=0 NormalZ=1 AngleXU=0 Radius=3.5
  constraints (18):
    c: Coincident(g0,g1)
    c: Coincident(g1,g2)
    c: Coincident(g2,g3)
    c: Horizontal(g0)
    c: Horizontal(g2)
    c: Vertical(g1)
    c: Vertical(g3)
    c: DistanceX(g2,g2) = 18.5
    c: DistanceX(g2) = -9.25
    c: DistanceY(g2) = -403
    c: PointOnObject(g4,g-2)
    c: PointOnObject(g5,g-2)
    c: Equal(g4,g5)
    c: Diameter(g4) = 7
    c: DistanceY(g4,g5) = 19.05
    c: DistanceY(g4) = -393.7
    c: DistanceY(g0) = -279
    c: Coincident(g0,g3)
FEATURE [Part::Feature] Part__Feature233  label="m6s001"
  Placement = pos=(0,-409.05,-16.5) rot=(0,0,1;0rad)
  shape: bbox 10.31 x 10.31 x 31.75 mm, 372 faces (baked)
FEATURE [Part::Feature] Part__Feature234  label="m6s"
  Placement = pos=(0,-390,-16.5) rot=(0,0,1;0rad)
  shape: bbox 10.31 x 10.31 x 31.75 mm, 372 faces (baked)
FEATURE [Part::MultiFuse] Fusion108  label="m6s002"
  Placement = pos=(0,15.35,0) rot=(0,0,1;0rad)
  Shapes = -> [Part__Feature233,Part__Feature234]
FEATURE [Part::Feature] Part__Feature235  label="M6Nut"
  Placement = pos=(0,-393.7,-20) rot=(1,0,0;3.14159rad)
  shape: bbox 25.4 x 11.25 x 3.15 mm, 18 faces (baked)
FEATURE [Part::Feature] Part__Feature236  label="M6Nut001"
  Placement = pos=(0,-374.65,-20) rot=(1,0,0;3.14159rad)
  shape: bbox 25.4 x 11.25 x 3.15 mm, 18 faces (baked)
FEATURE [Part::Extrusion] Extrude043  label="beam"
  Base = -> Sketch139
  Dir = (0,0,1)
  DirMode = 2
  FaceMakerClass = Part::FaceMakerBullseye
  LengthFwd = 10
  LengthRev = 0
  Solid = true
  Symmetric = false
FEATURE [Part::MultiFuse] Fusion109  label="m6Nuts"
  Shapes = -> [Part__Feature235,Part__Feature236]
FEATURE [Part::MultiFuse] Fusion110  label="m6s003"
  Shapes = -> [Fusion108,Fusion109]
FEATURE [Part::Feature] Part__Feature237  label="m4Nut"
  Placement = pos=(0,-393.75,-15) rot=(-1,0,0;1.5708rad)
  shape: bbox 8.084 x 2.201 x 8.084 mm, 26 faces (baked)
FEATURE [Part::Cylinder] Cylinder169  label="m2HeatSetInsets020"
  Angle = 360
  AttacherType = Attacher::AttachEngine3D
  FirstAngle = 0
  Height = 10
  Placement = pos=(-35,0,65) rot=(0,0,1;0rad)
  Radius = 2
  SecondAngle = 0
  expr: Radius = 2
FEATURE [Part::Cylinder] Cylinder170  label="m2HeatSetInsets021"
  Angle = 360
  AttacherType = Attacher::AttachEngine3D
  FirstAngle = 0
  Height = 10
  Placement = pos=(35,0,65) rot=(0,0,1;0rad)
  Radius = 2
  SecondAngle = 0
FEATURE [Part::Cylinder] Cylinder171  label="m2HeatSetInsets022"
  Angle = 360
  AttacherType = Attacher::AttachEngine3D
  FirstAngle = 0
  Height = 10
  Placement = pos=(0,35,65) rot=(0,0,1;0rad)
  Radius = 2
  SecondAngle = 0
FEATURE [Part::Cylinder] Cylinder172  label="m2HeatSetInsets023"
  Angle = 360
  AttacherType = Attacher::AttachEngine3D
  FirstAngle = 0
  Height = 10
  Placement = pos=(0,-35,65) rot=(0,0,1;0rad)
  Radius = 2
  SecondAngle = 0
  expr: Radius = 2
FEATURE [Part::MultiFuse] Fusion111  label="m3DomeCuts"
  Placement = pos=(0,-374,-75) rot=(0,0,-1;0.785398rad)
  Shapes = -> [Cylinder169,Cylinder170,Cylinder171,Cylinder172]
FEATURE [Part::Cylinder] Cylinder173  label="base015"
  Angle = 360
  AttacherType = Attacher::AttachEngine3D
  FirstAngle = 0
  Height = 4.5
  Placement = pos=(136,0,65) rot=(0,0,1;0rad)
  Radius = 40
  SecondAngle = 0
FEATURE [Part::Cylinder] Cylinder174  label="baseCut004"
  Angle = 360
  AttacherType = Attacher::AttachEngine3D
  FirstAngle = 0
  Height = 7
  Placement = pos=(5,0,74) rot=(0,0,1;0rad)
  Radius = 24
  SecondAngle = 0
FEATURE [Part::Cylinder] Cylinder176
  Angle = 360
  AttacherType = Attacher::AttachEngine3D
  FirstAngle = 0
  Height = 5.82
  Placement = pos=(0,-21,0) rot=(0,0,1;0rad)
  Radius = 5
  SecondAngle = 0
FEATURE [Part::Cylinder] Cylinder177
  Angle = 360
  AttacherType = Attacher::AttachEngine3D
  FirstAngle = 0
  Height = 5.82
  Placement = pos=(20.5,-21,0) rot=(0,0,1;0rad)
  Radius = 5
  SecondAngle = 0
  expr: Radius = 5
FEATURE [Part::Cylinder] Cylinder178
  Angle = 360
  AttacherType = Attacher::AttachEngine3D
  FirstAngle = 0
  Height = 5.82
  Placement = pos=(0,-21,0) rot=(0,0,1;0rad)
  Radius = 5
  SecondAngle = 0
FEATURE [Part::Cylinder] Cylinder179
  Angle = 360
  AttacherType = Attacher::AttachEngine3D
  FirstAngle = 0
  Height = 5.82
  Placement = pos=(20.5,-21,0) rot=(0,0,1;0rad)
  Radius = 5
  SecondAngle = 0
FEATURE [Part::Cylinder] Cylinder180
  Angle = 360
  AttacherType = Attacher::AttachEngine3D
  FirstAngle = 0
  Height = 10
  Placement = pos=(0,-21,0) rot=(0,0,1;0rad)
  Radius = 2
  SecondAngle = 0
FEATURE [Part::Cylinder] Cylinder181
  Angle = 360
  AttacherType = Attacher::AttachEngine3D
  FirstAngle = 0
  Height = 10
  Placement = pos=(20.5,-21,0) rot=(0,0,1;0rad)
  Radius = 2
  SecondAngle = 0
FEATURE [Part::Cylinder] Cylinder182
  Angle = 360
  AttacherType = Attacher::AttachEngine3D
  FirstAngle = 0
  Height = 10
  Placement = pos=(0,-21,0) rot=(0,0,1;0rad)
  Radius = 2
  SecondAngle = 0
FEATURE [Part::Cylinder] Cylinder183
  Angle = 360
  AttacherType = Attacher::AttachEngine3D
  FirstAngle = 0
  Height = 10
  Placement = pos=(20.5,-21,0) rot=(0,0,1;0rad)
  Radius = 2
  SecondAngle = 0
FEATURE [Part::MultiFuse] Fusion112  label="m3HeatSetCuts027"
  Placement = pos=(-5,39,70) rot=(0,0,1;0rad)
  Shapes = -> [Cylinder177,Cylinder176]
FEATURE [Part::MultiFuse] Fusion113  label="m3HeatSetCuts028"
  Placement = pos=(-5,3,70) rot=(0,0,1;0rad)
  Shapes = -> [Cylinder179,Cylinder178]
FEATURE [Part::MultiFuse] Fusion114  label="m3HeatSetCuts029"
  Placement = pos=(128.75,10,-1) rot=(0,0,1;0rad)
  Shapes = -> [Fusion113,Fusion112]
FEATURE [Part::MultiFuse] Fusion118  label="m3HeatSetCuts031"
  Placement = pos=(-5,39,70) rot=(0,0,1;0rad)
  Shapes = -> [Cylinder181,Cylinder180]
FEATURE [Part::MultiFuse] Fusion119  label="m3HeatSetCuts032"
  Placement = pos=(-5,3,70) rot=(0,0,1;0rad)
  Shapes = -> [Cylinder183,Cylinder182]
FEATURE [Part::MultiFuse] Fusion117  label="m3HeatSetCuts030"
  Placement = pos=(128.75,10,-1) rot=(0,0,1;0rad)
  Shapes = -> [Fusion119,Fusion118]
FEATURE [Part::Sphere] Sphere006  label="SphereBase004"
  Angle1 = 0
  Angle2 = 12
  Angle3 = 360
  AttacherType = Attacher::AttachEngine3D
  Placement = pos=(5,0,74) rot=(0,0,1;0rad)
  Radius = 27.5
FEATURE [Part::Cut] Cut058
  Base = -> Sphere006
  Placement = pos=(131,0,-5) rot=(0,0,1;0rad)
  Tool = -> Cylinder174
FEATURE [Part::MultiFuse] Fusion115  label="Base004"
  Placement = pos=(-2,10,0) rot=(0,0,1;0rad)
  Shapes = -> [Cut058,Cylinder173]
FEATURE [Part::MultiFuse] Fusion116  label="lightModule012"
  Shapes = -> [Fusion115,Fusion114]
FEATURE [Part::MultiFuse] Fusion120
  Shapes = -> [Fusion111,Fusion117]
FEATURE [Part::MultiFuse] Fusion096  label="mainModule"
  Placement = pos=(0,0,239.25) rot=(0,0,1;0rad)
  Shapes = -> [E305__20x28x7cm_,Fusion095,P120]
FEATURE [Part::Cut] Cut059
  Base = -> Fusion116
  Placement = pos=(-134,-384,-74.75) rot=(0,0,1;0rad)
  Tool = -> Fusion120
FEATURE [Part::Cylinder] Cylinder184  label="m2HeatSetInsets024"
  Angle = 360
  AttacherType = Attacher::AttachEngine3D
  FirstAngle = 0
  Height = 10
  Placement = pos=(-35,0,65) rot=(0,0,1;0rad)
  Radius = 2
  SecondAngle = 0
  expr: Radius = 2
FEATURE [Part::Cylinder] Cylinder185  label="m2HeatSetInsets025"
  Angle = 360
  AttacherType = Attacher::AttachEngine3D
  FirstAngle = 0
  Height = 10
  Placement = pos=(35,0,65) rot=(0,0,1;0rad)
  Radius = 2
  SecondAngle = 0
FEATURE [Part::Cylinder] Cylinder186  label="m2HeatSetInsets026"
  Angle = 360
  AttacherType = Attacher::AttachEngine3D
  FirstAngle = 0
  Height = 10
  Placement = pos=(0,35,65) rot=(0,0,1;0rad)
  Radius = 2
  SecondAngle = 0
FEATURE [Part::Cylinder] Cylinder187  label="m2HeatSetInsets027"
  Angle = 360
  AttacherType = Attacher::AttachEngine3D
  FirstAngle = 0
  Height = 10
  Placement = pos=(0,-35,65) rot=(0,0,1;0rad)
  Radius = 2
  SecondAngle = 0
  expr: Radius = 2
FEATURE [Part::MultiFuse] Fusion121
  Placement = pos=(0,-374,-75) rot=(0,0,-1;0.785398rad)
  Shapes = -> [Cylinder184,Cylinder185,Cylinder186,Cylinder187]
FEATURE [Part::Cut] Cut060  label="lightModule"
  Base = -> Cut059
  Tool = -> Fusion121
FEATURE [Sketcher::SketchObject] Sketch140
  FullyConstrained = true
  Placement = pos=(0,-370,0) rot=(1,0,0;1.5708rad)
  sketch-geometry (8):
    g0: LineSegment StartX=-13.5 StartY=-9.75 StartZ=0 EndX=-9.5 EndY=-9.75 EndZ=0
    g1: LineSegment StartX=-9.5 StartY=-9.75 StartZ=0 EndX=-9.5 EndY=-20.25 EndZ=0
    g2: LineSegment StartX=-9.5 StartY=-20.25 StartZ=0 EndX=9.5 EndY=-20.25 EndZ=0
    g3: LineSegment StartX=9.5 StartY=-20.25 StartZ=0 EndX=9.5 EndY=-9.75 EndZ=0
    g4: LineSegment StartX=9.5 StartY=-9.75 StartZ=0 EndX=13.5 EndY=-9.75 EndZ=0
    g5: LineSegment StartX=13.5 StartY=-9.75 StartZ=0 EndX=13.5 EndY=-24.25 EndZ=0
    g6: LineSegment StartX=13.5 StartY=-24.25 StartZ=0 EndX=-13.5 EndY=-24.25 EndZ=0
    g7: LineSegment StartX=-13.5 StartY=-24.25 StartZ=0 EndX=-13.5 EndY=-9.75 EndZ=0
  constraints (24):
    c: Horizontal(g0)
    c: Coincident(g1,g0)
    c: Vertical(g1)
    c: Coincident(g2,g1)
    c: Horizontal(g2)
    c: Coincident(g3,g2)
    c: Vertical(g3)
    c: Coincident(g4,g3)
    c: Horizontal(g4)
    c: Coincident(g5,g4)
    c: Vertical(g5)
    c: Coincident(g6,g5)
    c: Horizontal(g6)
    c: Coincident(g7,g6)
    c: Coincident(g7,g0)
    c: Vertical(g7)
    c: DistanceY(g0) = -9.75
    c: DistanceX(g0) = -13.5
    c: DistanceX(g0) = -9.5
    c: DistanceY(g6) = -24.25
    c: DistanceX(g5) = 13.5
    c: DistanceY(g2) = -20.25
    c: DistanceX(g2) = 9.5
    c: DistanceY(g3,g0) = 0
FEATURE [Part::Extrusion] Extrude044
  Base = -> Sketch140
  Dir = (0,-1,2e-16)
  DirMode = 2
  FaceMakerClass = Part::FaceMakerBullseye
  LengthFwd = 33
  LengthRev = 0
  Solid = true
  Symmetric = false
FEATURE [Sketcher::SketchObject] Sketch141
  FullyConstrained = true
  Placement = pos=(0,-403,0) rot=(1,0,0;1.5708rad)
  sketch-geometry (5):
    g0: LineSegment StartX=-13.5 StartY=-9.75 StartZ=0 EndX=13.5 EndY=-9.75 EndZ=0
    g1: LineSegment StartX=13.5 StartY=-9.75 StartZ=0 EndX=13.5 EndY=-24.25 EndZ=0
    g2: LineSegment StartX=13.5 StartY=-24.25 StartZ=0 EndX=-13.5 EndY=-24.25 EndZ=0
    g3: LineSegment StartX=-13.5 StartY=-24.25 StartZ=0 EndX=-13.5 EndY=-9.75 EndZ=0
    g4: Circle CenterX=0 CenterY=-15 CenterZ=0 NormalX=0 NormalY=0 NormalZ=1 AngleXU=0 Radius=2.125
  constraints (15):
    c: Coincident(g0,g1)
    c: Coincident(g1,g2)
    c: Coincident(g2,g3)
    c: Coincident(g3,g0)
    c: Horizontal(g0)
    c: Horizontal(g2)
    c: Vertical(g1)
    c: Vertical(g3)
    c: DistanceY(g0) = -9.75
    c: DistanceX(g0) = -13.5
    c: DistanceX(g1) = 13.5
    c: DistanceY(g1) = -24.25
    c: PointOnObject(g4,g-2)
    c: Diameter(g4) = 4.25
    c: DistanceY(g2,g4) = 9.25
FEATURE [Part::Extrusion] Extrude045
  Base = -> Sketch141
  Dir = (0,-1,2e-16)
  DirMode = 2
  FaceMakerClass = Part::FaceMakerBullseye
  LengthFwd = 4
  LengthRev = 0
  Solid = true
  Symmetric = false
FEATURE [Part::MultiFuse] Fusion122  label="lightModule013"
  Shapes = -> [Extrude045,Cut060,Extrude044]
FEATURE [Sketcher::SketchObject] Sketch142
  FullyConstrained = true
  Placement = pos=(0,0,-24.25) rot=(0,0,1;0rad)
  sketch-geometry (1):
    g0: Circle CenterX=18.5 CenterY=-375 CenterZ=0 NormalX=0 NormalY=0 NormalZ=1 AngleXU=0 Radius=2.5
  constraints (3):
    c: Diameter(g0) = 5
    c: DistanceY(g0) = -375
    c: DistanceX(g0) = 18.5
FEATURE [Sketcher::SketchObject] Sketch143
  FullyConstrained = true
  Placement = pos=(0,0,-24.25) rot=(0,0,1;0rad)
  sketch-geometry (4):
    g0: ArcOfCircle CenterX=18.5 CenterY=-375 CenterZ=0 NormalX=0 NormalY=0 NormalZ=1 AngleXU=0 Radius=5 StartAngle=4.71239 EndAngle=7.85398
    g1: LineSegment StartX=18.5 StartY=-380 StartZ=0 EndX=13.5 EndY=-380 EndZ=0
    g2: LineSegment StartX=13.5 StartY=-380 StartZ=0 EndX=13.5 EndY=-370 EndZ=0
    g3: LineSegment StartX=13.5 StartY=-370 StartZ=0 EndX=18.5 EndY=-370 EndZ=0
  constraints (13):
    c: DistanceX(g0) = 18.5
    c: DistanceY(g0) = -375
    c: DistanceX(g0,g0) = 0
    c: Angle(g0) = 3.14159
    c: Coincident(g1,g0)
    c: Horizontal(g1)
    c: Coincident(g2,g1)
    c: Vertical(g2)
    c: Coincident(g3,g2)
    c: Coincident(g3,g0)
    c: Horizontal(g3)
    c: DistanceX(g1) = 13.5
    c: Diameter(g0) = 10
FEATURE [Part::Extrusion] Extrude046  label="lightWire"
  Base = -> Sketch142
  Dir = (0,0,1)
  DirMode = 2
  FaceMakerClass = Part::FaceMakerBullseye
  LengthFwd = 19
  LengthRev = 0
  Solid = true
  Symmetric = false
FEATURE [Part::Extrusion] Extrude047
  Base = -> Sketch143
  Dir = (0,0,1)
  DirMode = 2
  FaceMakerClass = Part::FaceMakerBullseye
  LengthFwd = 19
  LengthRev = 0
  Solid = true
  Symmetric = false
FEATURE [Part::MultiFuse] Fusion123  label="lightModule014"
  Shapes = -> [Fusion122,Extrude047]
FEATURE [Part::Cut] Cut061  label="lightModule015"
  Base = -> Fusion123
  Tool = -> Extrude046
FEATURE [Part::Feature] Part__Feature238  label="m4"
  Placement = pos=(0,-393,-15) rot=(-1,0,0;1.5708rad)
  shape: bbox 7.001 x 18.15 x 7.001 mm, 110 faces (baked)
FEATURE [Sketcher::SketchObject] Sketch144
  FullyConstrained = true
  Placement = pos=(0,-392.25,0) rot=(1,0,0;1.5708rad)
  sketch-geometry (5):
    g0: LineSegment StartX=-3.75 StartY=-10 StartZ=0 EndX=-3.75 EndY=-17.0849 EndZ=0
    g1: LineSegment StartX=-3.75 StartY=-17.0849 StartZ=0 EndX=0 EndY=-19.25 EndZ=0
    g2: LineSegment StartX=0 StartY=-19.25 StartZ=0 EndX=3.75 EndY=-17.0849 EndZ=0
    g3: LineSegment StartX=3.75 StartY=-17.0849 StartZ=0 EndX=3.75 EndY=-10 EndZ=0
    g4: LineSegment StartX=-3.75 StartY=-10 StartZ=0 EndX=3.75 EndY=-10 EndZ=0
  constraints (15):
    c: Vertical(g0)
    c: Coincident(g1,g0)
    c: PointOnObject(g1,g-2)
    c: Coincident(g2,g1)
    c: Coincident(g3,g2)
    c: Vertical(g3)
    c: Angle(g2,g1) = 2.0944
    c: DistanceY(g1) = -19.25
    c: DistanceY(g2,g0) = 0
    c: Angle(g3,g2) = 2.0944
    c: DistanceX(g2) = 3.75
    c: Coincident(g4,g0)
    c: Coincident(g4,g3)
    c: Horizontal(g4)
    c: DistanceY(g3) = -10
FEATURE [Part::Extrusion] Extrude048
  Base = -> Sketch144
  Dir = (0,-1,2e-16)
  DirMode = 2
  FaceMakerClass = Part::FaceMakerBullseye
  LengthFwd = 3
  LengthRev = 0
  Solid = true
  Symmetric = false
FEATURE [Part::Cut] Cut062  label="beam001"
  Base = -> Extrude043
  Tool = -> Extrude048
FEATURE [Sketcher::SketchObject] Sketch145
  FullyConstrained = true
  Placement = pos=(0,-392.25,0) rot=(1,0,0;1.5708rad)
  sketch-geometry (7):
    g0: LineSegment StartX=3.68061 StartY=-17.125 StartZ=0 EndX=3.68061 EndY=-12.875 EndZ=0
    g1: LineSegment StartX=3.68061 StartY=-12.875 StartZ=0 EndX=-1.628e-12 EndY=-10.75 EndZ=0
    g2: LineSegment StartX=-1.628e-12 StartY=-10.75 StartZ=0 EndX=-3.68061 EndY=-12.875 EndZ=0
    g3: LineSegment StartX=-3.68061 StartY=-12.875 StartZ=0 EndX=-3.68061 EndY=-17.125 EndZ=0
    g4: LineSegment StartX=-3.68061 StartY=-17.125 StartZ=0 EndX=-1.6276e-12 EndY=-19.25 EndZ=0
    g5: LineSegment StartX=-1.6276e-12 StartY=-19.25 StartZ=0 EndX=3.68061 EndY=-17.125 EndZ=0
    g6: Circle CenterX=0 CenterY=-15 CenterZ=0 NormalX=0 NormalY=0 NormalZ=1 AngleXU=0 Radius=4.25
  constraints (17):
    c: Coincident(g0,g1)
    c: Coincident(g1,g2)
    c: Coincident(g2,g3)
    c: Coincident(g3,g4)
    c: Coincident(g4,g5)
    c: Coincident(g5,g0)
    c: Equal(g0, g1-g5) x5
    c: PointOnObject(g0,g6)
    c: PointOnObject(g1,g6)
    c: PointOnObject(g2,g6)
    c: PointOnObject(g3,g6)
    c: PointOnObject(g4,g6)
    c: PointOnObject(g5,g6)
    c: PointOnObject(g6,g-2)
    c: DistanceY(g4) = -19.25
    c: Vertical(g0)
    c: DistanceY(g1) = -10.75
FEATURE [Part::Extrusion] Extrude049
  Base = -> Sketch145
  Dir = (0,-1,2e-16)
  DirMode = 2
  FaceMakerClass = Part::FaceMakerBullseye
  LengthFwd = 3
  LengthRev = 0
  Placement = pos=(0,-2,0) rot=(0,0,1;0rad)
  Solid = true
  Symmetric = false
FEATURE [Part::Cut] Cut063  label="beam002"
  Base = -> Cut062
  Tool = -> Extrude049
FEATURE [Part::Cut] Cut064  label="srs001"
  Base = -> Fusion106
  Tool = -> Cylinder162
FEATURE [Sketcher::SketchObject] Sketch146
  FullyConstrained = true
  sketch-geometry (14):
    g0: LineSegment StartX=5 StartY=-8.66025 StartZ=0 EndX=10 EndY=3.2e-14 EndZ=0
    g1: LineSegment StartX=10 StartY=3.2e-14 StartZ=0 EndX=5 EndY=8.66025 EndZ=0
    g2: LineSegment StartX=5 StartY=8.66025 StartZ=0 EndX=-5 EndY=8.66025 EndZ=0
    g3: LineSegment StartX=-5 StartY=8.66025 StartZ=0 EndX=-10 EndY=-4.26e-14 EndZ=0
    g4: LineSegment StartX=-10 StartY=-4.26e-14 StartZ=0 EndX=-5 EndY=-8.66025 EndZ=0
    g5: LineSegment StartX=-5 StartY=-8.66025 StartZ=0 EndX=5 EndY=-8.66025 EndZ=0
    g6: Circle CenterX=0 CenterY=0 CenterZ=0 NormalX=0 NormalY=0 NormalZ=1 AngleXU=0 Radius=10
    g7: LineSegment StartX=1.75 StartY=-3.03109 StartZ=0 EndX=3.5 EndY=-8.26e-14 EndZ=0
    g8: LineSegment StartX=3.5 StartY=-8.26e-14 StartZ=0 EndX=1.75 EndY=3.03109 EndZ=0
    g9: LineSegment StartX=1.75 StartY=3.03109 StartZ=0 EndX=-1.75 EndY=3.03109 EndZ=0
    g10: LineSegment StartX=-1.75 StartY=3.03109 StartZ=0 EndX=-3.5 EndY=8.08e-14 EndZ=0
    g11: LineSegment StartX=-3.5 StartY=8.08e-14 StartZ=0 EndX=-1.75 EndY=-3.03109 EndZ=0
    g12: LineSegment StartX=-1.75 StartY=-3.03109 StartZ=0 EndX=1.75 EndY=-3.03109 EndZ=0
    g13: Circle CenterX=0 CenterY=0 CenterZ=0 NormalX=0 NormalY=0 NormalZ=1 AngleXU=0 Radius=3.5
  constraints (33):
    c: Coincident(g0,g1)
    c: Coincident(g1,g2)
    c: Coincident(g2,g3)
    c: Coincident(g3,g4)
    c: Coincident(g4,g5)
    c: Coincident(g5,g0)
    c: Equal(g0, g1-g5) x5
    c: PointOnObject(g0,g6)
    c: PointOnObject(g1,g6)
    c: PointOnObject(g2,g6)
    c: PointOnObject(g3,g6)
    c: PointOnObject(g4,g6)
    c: PointOnObject(g5,g6)
    c: DistanceX(g6) = 0
    c: DistanceY(g6) = 0
    c: Horizontal(g5)
    c: Coincident(g7,g8)
    c: Coincident(g8,g9)
    c: Coincident(g9,g10)
    c: Coincident(g10,g11)
    c: Coincident(g11,g12)
    c: Coincident(g12,g7)
    c: Equal(g7, g8-g12) x5
    c: PointOnObject(g7,g13)
    c: PointOnObject(g8,g13)
    c: PointOnObject(g9,g13)
    c: PointOnObject(g10,g13)
    c: PointOnObject(g11,g13)
    c: PointOnObject(g12,g13)
    c: Coincident(g13,g6)
    c: Horizontal(g12)
    c: Diameter(g13) = 7
    c: Diameter(g6) = 20
FEATURE [Part::Feature] Part__Feature239  label="m3"
  Placement = pos=(0,0,1) rot=(0,0,-1;0.523599rad)
  shape: bbox 6.352 x 6.352 x 2.188 mm, 35 faces (baked)
FEATURE [Part::Extrusion] Extrude050  label="m4Cover"
  Base = -> Sketch146
  Dir = (0,0,1)
  DirMode = 2
  FaceMakerClass = Part::FaceMakerBullseye
  LengthFwd = 3
  LengthRev = 0
  Placement = pos=(0,-291.803,2.70756) rot=(1,0,0;3.83972rad)
  Solid = true
  Symmetric = false
FEATURE [Part::MultiFuse] Fusion124  label="srs002"
  Shapes = -> [Extrude050,Cut064]
FEATURE [Sketcher::SketchObject] Sketch147
  FullyConstrained = true
  MapMode = 2
  Support = -> [Fusion124]
  sketch-geometry (4):
    g0: LineSegment StartX=24 StartY=-259.3 StartZ=0 EndX=24 EndY=-323.3 EndZ=0
    g1: LineSegment StartX=24 StartY=-323.3 StartZ=0 EndX=28 EndY=-323.3 EndZ=0
    g2: LineSegment StartX=28 StartY=-323.3 StartZ=0 EndX=28 EndY=-262.206 EndZ=0
    g3: LineSegment StartX=24 StartY=-259.3 StartZ=0 EndX=28 EndY=-262.206 EndZ=0
  constraints (12):
    c: Vertical(g0)
    c: Coincident(g1,g0)
    c: Coincident(g2,g1)
    c: Vertical(g2)
    c: Horizontal(g1)
    c: DistanceX(g0) = 24
    c: DistanceX(g1,g1) = 4
    c: DistanceY(g0) = -323.3
    c: Coincident(g3,g0)
    c: Coincident(g3,g2)
    c: Angle(g0,g3) = 0.942478
    c: DistanceY(g0) = -259.3
FEATURE [Part::Extrusion] Extrude051  label="rail"
  Base = -> Sketch147
  Dir = (0,0,1)
  DirMode = 2
  FaceMakerClass = Part::FaceMakerBullseye
  LengthFwd = 4
  LengthRev = 0
  Placement = pos=(0,0,-16) rot=(0,0,1;0rad)
  Solid = true
  Symmetric = false
FEATURE [Part::Cylinder] Cylinder188  label="m6Cut001"
  Angle = 360
  AttacherType = Attacher::AttachEngine3D
  FirstAngle = 0
  Height = 10
  Placement = pos=(0,-263.25,14.5) rot=(0,0,1;0rad)
  Radius = 6.25
  SecondAngle = 0
FEATURE [Sketcher::SketchObject] Sketch148  label="SketchTop017"
  FullyConstrained = true
  sketch-geometry (6):
    g0: LineSegment StartX=50 StartY=-368.819 StartZ=0 EndX=80.9017 EndY=-273.713 EndZ=0
    g1: LineSegment StartX=80.9017 StartY=-273.713 StartZ=0 EndX=0 EndY=-214.935 EndZ=0
    g2: LineSegment StartX=0 StartY=-214.935 StartZ=0 EndX=-80.9017 EndY=-273.713 EndZ=0
    g3: LineSegment StartX=-80.9017 StartY=-273.713 StartZ=0 EndX=-50 EndY=-368.819 EndZ=0
    g4: LineSegment StartX=-50 StartY=-368.819 StartZ=0 EndX=50 EndY=-368.819 EndZ=0
    g5: Circle CenterX=0 CenterY=-300 CenterZ=0 NormalX=0 NormalY=0 NormalZ=1 AngleXU=0 Radius=85.0651
  constraints (15):
    c: Coincident(g0,g1)
    c: Coincident(g1,g2)
    c: Coincident(g2,g3)
    c: Coincident(g3,g4)
    c: Coincident(g4,g0)
    c: Equal(g0, g1-g4) x4
    c: PointOnObject(g0,g5)
    c: PointOnObject(g1,g5)
    c: PointOnObject(g2,g5)
    c: PointOnObject(g3,g5)
    c: PointOnObject(g4,g5)
    c: Horizontal(g4)
    c: DistanceX(g4,g4) = 100
    c: DistanceY(g5) = -300
    c: DistanceX(g5) = 0
FEATURE [Sketcher::SketchObject] Sketch149  label="SketchBottom019"
  FullyConstrained = true
  Placement = pos=(0,0,20) rot=(0,0,1;0rad)
  sketch-geometry (6):
    g0: LineSegment StartX=37.5 StartY=-351.614 StartZ=0 EndX=60.6763 EndY=-280.285 EndZ=0
    g1: LineSegment StartX=60.6763 StartY=-280.285 StartZ=0 EndX=0 EndY=-236.201 EndZ=0
    g2: LineSegment StartX=0 StartY=-236.201 StartZ=0 EndX=-60.6763 EndY=-280.285 EndZ=0
    g3: LineSegment StartX=-60.6763 StartY=-280.285 StartZ=0 EndX=-37.5 EndY=-351.614 EndZ=0
    g4: LineSegment StartX=-37.5 StartY=-351.614 StartZ=0 EndX=37.5 EndY=-351.614 EndZ=0
    g5: Circle CenterX=0 CenterY=-300 CenterZ=0 NormalX=0 NormalY=0 NormalZ=1 AngleXU=0 Radius=63.7988
  constraints (15):
    c: Coincident(g0,g1)
    c: Coincident(g1,g2)
    c: Coincident(g2,g3)
    c: Coincident(g3,g4)
    c: Coincident(g4,g0)
    c: Equal(g0, g1-g4) x4
    c: PointOnObject(g0,g5)
    c: PointOnObject(g1,g5)
    c: PointOnObject(g2,g5)
    c: PointOnObject(g3,g5)
    c: PointOnObject(g4,g5)
    c: Horizontal(g4)
    c: DistanceX(g4,g4) = 75
    c: DistanceX(g5) = 0
    c: DistanceY(g5) = -300
FEATURE [Part::Loft] Loft036
  Closed = false
  MaxDegree = 5
  Ruled = false
  Sections = -> [Sketch148,Sketch149]
  Solid = true
FEATURE [Sketcher::SketchObject] Sketch150  label="SketchTop018"
  FullyConstrained = true
  sketch-geometry (6):
    g0: LineSegment StartX=47.5 StartY=-365.378 StartZ=0 EndX=76.8566 EndY=-275.028 EndZ=0
    g1: LineSegment StartX=76.8566 StartY=-275.028 StartZ=0 EndX=1.9185e-12 EndY=-219.188 EndZ=0
    g2: LineSegment StartX=1.9185e-12 StartY=-219.188 StartZ=0 EndX=-76.8566 EndY=-275.028 EndZ=0
    g3: LineSegment StartX=-76.8566 StartY=-275.028 StartZ=0 EndX=-47.5 EndY=-365.378 EndZ=0
    g4: LineSegment StartX=-47.5 StartY=-365.378 StartZ=0 EndX=47.5 EndY=-365.378 EndZ=0
    g5: Circle CenterX=0 CenterY=-300 CenterZ=0 NormalX=0 NormalY=0 NormalZ=1 AngleXU=0 Radius=80.8118
  constraints (15):
    c: Coincident(g0,g1)
    c: Coincident(g1,g2)
    c: Coincident(g2,g3)
    c: Coincident(g3,g4)
    c: Coincident(g4,g0)
    c: Equal(g0, g1-g4) x4
    c: PointOnObject(g0,g5)
    c: PointOnObject(g1,g5)
    c: PointOnObject(g2,g5)
    c: PointOnObject(g3,g5)
    c: PointOnObject(g4,g5)
    c: Horizontal(g4)
    c: DistanceX(g4,g4) = 95
    c: DistanceY(g5) = -300
    c: DistanceX(g5) = 0
FEATURE [Sketcher::SketchObject] Sketch151  label="SketchBottom020"
  FullyConstrained = true
  Placement = pos=(0,0,20) rot=(0,0,1;0rad)
  sketch-geometry (6):
    g0: LineSegment StartX=35 StartY=-348.173 StartZ=0 EndX=56.6312 EndY=-281.599 EndZ=0
    g1: LineSegment StartX=56.6312 StartY=-281.599 StartZ=0 EndX=0 EndY=-240.454 EndZ=0
    g2: LineSegment StartX=0 StartY=-240.454 StartZ=0 EndX=-56.6312 EndY=-281.599 EndZ=0
    g3: LineSegment StartX=-56.6312 StartY=-281.599 StartZ=0 EndX=-35 EndY=-348.173 EndZ=0
    g4: LineSegment StartX=-35 StartY=-348.173 StartZ=0 EndX=35 EndY=-348.173 EndZ=0
    g5: Circle CenterX=0 CenterY=-300 CenterZ=0 NormalX=0 NormalY=0 NormalZ=1 AngleXU=0 Radius=59.5456
  constraints (15):
    c: Coincident(g0,g1)
    c: Coincident(g1,g2)
    c: Coincident(g2,g3)
    c: Coincident(g3,g4)
    c: Coincident(g4,g0)
    c: Equal(g0, g1-g4) x4
    c: PointOnObject(g0,g5)
    c: PointOnObject(g1,g5)
    c: PointOnObject(g2,g5)
    c: PointOnObject(g3,g5)
    c: PointOnObject(g4,g5)
    c: Horizontal(g4)
    c: DistanceX(g4,g4) = 70
    c: DistanceX(g5) = 0
    c: DistanceY(g5) = -300
FEATURE [Part::Loft] Loft037
  Closed = false
  MaxDegree = 5
  Ruled = false
  Sections = -> [Sketch150,Sketch151]
  Solid = true
FEATURE [Part::Cut] Cut065  label="srsCone014"
  Base = -> Loft036
  Placement = pos=(0,0,-36) rot=(0,0,1;0rad)
  Tool = -> Loft037
FEATURE [Part::Fillet] Fillet059
  Base = -> Cut065
  Edges = 5 edges r=1.5: [Edge3,Edge15,Edge16,Edge17,Edge18]
FEATURE [Part::Fillet] Fillet060
  Base = -> Fillet059
  Edges = 5 edges r=1.5: [Edge4,Edge7,Edge11,Edge12,Edge13]
FEATURE [Part::Fillet] Fillet061
  Base = -> Fillet060
  Edges = 5 edges r=2: [Edge1,Edge3,Edge5,Edge15,Edge17]
FEATURE [Part::Fillet] Fillet062  label="srsCone015"
  Base = -> Fillet061
  Edges = 5 edges r=1.5: [Edge63,Edge64,Edge65,Edge66,Edge67]
  Placement = pos=(0,0,-112.25) rot=(0,0,1;0rad)
FEATURE [Sketcher::SketchObject] Sketch152  label="SketchBottom021"
  FullyConstrained = true
  Placement = pos=(0,0,20) rot=(0,0,1;0rad)
  sketch-geometry (6):
    g0: LineSegment StartX=37.5 StartY=-351.614 StartZ=0 EndX=60.6763 EndY=-280.285 EndZ=0
    g1: LineSegment StartX=60.6763 StartY=-280.285 StartZ=0 EndX=0 EndY=-236.201 EndZ=0
    g2: LineSegment StartX=0 StartY=-236.201 StartZ=0 EndX=-60.6763 EndY=-280.285 EndZ=0
    g3: LineSegment StartX=-60.6763 StartY=-280.285 StartZ=0 EndX=-37.5 EndY=-351.614 EndZ=0
    g4: LineSegment StartX=-37.5 StartY=-351.614 StartZ=0 EndX=37.5 EndY=-351.614 EndZ=0
    g5: Circle CenterX=0 CenterY=-300 CenterZ=0 NormalX=0 NormalY=0 NormalZ=1 AngleXU=0 Radius=63.7988
  constraints (15):
    c: Coincident(g0,g1)
    c: Coincident(g1,g2)
    c: Coincident(g2,g3)
    c: Coincident(g3,g4)
    c: Coincident(g4,g0)
    c: Equal(g0, g1-g4) x4
    c: PointOnObject(g0,g5)
    c: PointOnObject(g1,g5)
    c: PointOnObject(g2,g5)
    c: PointOnObject(g3,g5)
    c: PointOnObject(g4,g5)
    c: Horizontal(g4)
    c: DistanceX(g4,g4) = 75
    c: DistanceX(g5) = 0
    c: DistanceY(g5) = -300
FEATURE [Part::Extrusion] Extrude052  label="top001"
  Base = -> Sketch152
  Dir = (0,0,1)
  DirMode = 2
  FaceMakerClass = Part::FaceMakerBullseye
  LengthFwd = 4
  LengthRev = 0
  Placement = pos=(0,0,-152.25) rot=(0,0,1;0rad)
  Solid = true
  Symmetric = false
FEATURE [Part::Fillet] Fillet063
  Base = -> Extrude052
  Edges = 5 edges r=1: [Edge4,Edge7,Edge10,Edge13,Edge15]
FEATURE [Part::MultiFuse] Fusion125  label="base"
  Shapes = -> [Fillet062,Fillet063]
FEATURE [Sketcher::SketchObject] Sketch019
  FullyConstrained = true
  Placement = pos=(0,-295,0) rot=(1,0,0;1.5708rad)
  sketch-geometry (14):
    g0: LineSegment StartX=28 StartY=-309 StartZ=0 EndX=28 EndY=-301 EndZ=0
    g1: LineSegment StartX=-19 StartY=-309 StartZ=0 EndX=28 EndY=-309 EndZ=0
    g2: LineSegment StartX=-19 StartY=-309 StartZ=0 EndX=-19 EndY=-284 EndZ=0
    g3: LineSegment StartX=-19 StartY=-284 StartZ=0 EndX=-13 EndY=-284 EndZ=0
    g4: LineSegment StartX=-13 StartY=-284 StartZ=0 EndX=-13 EndY=-301 EndZ=0
    g5: Circle CenterX=-15.96 CenterY=-286.8 CenterZ=0 NormalX=0 NormalY=0 NormalZ=1 AngleXU=0 Radius=1.125
    g6: Circle CenterX=-0.15 CenterY=-304.37 CenterZ=0 NormalX=0 NormalY=0 NormalZ=1 AngleXU=0 Radius=1.125
    g7: Circle CenterX=20.15 CenterY=-304.37 CenterZ=0 NormalX=0 NormalY=0 NormalZ=1 AngleXU=0 Radius=1.125
    g8: LineSegment StartX=-13 StartY=-301 StartZ=0 EndX=11 EndY=-301 EndZ=0
    g9: LineSegment StartX=11 StartY=-301 StartZ=0 EndX=11 EndY=-263 EndZ=0
    g10: LineSegment StartX=11 StartY=-263 StartZ=0 EndX=19 EndY=-263 EndZ=0
    g11: LineSegment StartX=19 StartY=-263 StartZ=0 EndX=19 EndY=-301 EndZ=0
    g12: LineSegment StartX=19 StartY=-301 StartZ=0 EndX=28 EndY=-301 EndZ=0
    g13: Circle CenterX=16.04 CenterY=-270.55 CenterZ=0 NormalX=0 NormalY=0 NormalZ=1 AngleXU=0 Radius=1.125
  constraints (42):
    c: Vertical(g0)
    c: Coincident(g1,g0)
    c: Horizontal(g1)
    c: DistanceX(g0) = 28
    c: Vertical(g2)
    c: Coincident(g3,g2)
    c: Horizontal(g3)
    c: Coincident(g4,g3)
    c: Vertical(g4)
    c: DistanceY(g1,g6) = 4.63
    c: DistanceY(g6,g7) = 0
    c: DistanceX(g6,g7) = 20.3
    c: DistanceY(g1) = -309
    c: Coincident(g2,g1)
    c: Coincident(g8,g4)
    c: Horizontal(g8)
    c: DistanceX(g4) = -13
    c: Vertical(g9)
    c: Distance(g3) = 6
    c: Coincident(g10,g9)
    c: Horizontal(g10)
    c: Coincident(g11,g10)
    c: Vertical(g11)
    c: Coincident(g12,g0)
    c: Horizontal(g12)
    c: DistanceY(g8,g11) = 0
    c: Coincident(g11,g12)
    c: DistanceX(g10) = 19
    c: DistanceX(g10,g10) = 8
    c: Coincident(g8,g9)
    c: DistanceY(g9) = -263
    c: DistanceY(g1,g4) = 8
    c: DistanceY(g1,g2) = 25
    c: DistanceX(g5,g13) = 32
    c: DistanceY(g5,g13) = 16.25
    c: DistanceY(g1,g5) = 22.2
    c: DistanceX(g1,g5) = 3.04
    c: Equal(g6,g7)
    c: Equal(g6,g5)
    c: Equal(g6,g13)
    c: Diameter(g6) = 2.25
    c: DistanceX(g6) = -0.15
FEATURE [Part::Extrusion] Extrude003  label="i2cHold"
  Base = -> Sketch019
  Dir = (0,-1,2e-16)
  DirMode = 2
  FaceMakerClass = Part::FaceMakerBullseye
  LengthFwd = 5
  LengthRev = 0
  Solid = true
  Symmetric = false
FEATURE [Sketcher::SketchObject] Sketch020
  FullyConstrained = true
  Placement = pos=(0,0,-263) rot=(0,0,1;0rad)
  sketch-geometry (6):
    g0: LineSegment StartX=11 StartY=-281.5 StartZ=0 EndX=19 EndY=-281.5 EndZ=0
    g1: LineSegment StartX=11 StartY=-281.5 StartZ=0 EndX=11 EndY=-307 EndZ=0
    g2: LineSegment StartX=11 StartY=-307 StartZ=0 EndX=19 EndY=-307 EndZ=0
    g3: LineSegment StartX=19 StartY=-307 StartZ=0 EndX=19 EndY=-281.5 EndZ=0
    g4: Circle CenterX=15 CenterY=-284.1 CenterZ=0 NormalX=0 NormalY=0 NormalZ=1 AngleXU=0 Radius=1.625
    g5: Circle CenterX=15 CenterY=-304.5 CenterZ=0 NormalX=0 NormalY=0 NormalZ=1 AngleXU=0 Radius=1.625
  constraints (18):
    c: Horizontal(g0)
    c: Coincident(g1,g0)
    c: Vertical(g1)
    c: Coincident(g2,g1)
    c: Horizontal(g2)
    c: Coincident(g3,g2)
    c: Coincident(g3,g0)
    c: Vertical(g3)
    c: DistanceX(g1,g2) = 8
    c: DistanceY(g1,g0) = 25.5
    c: Equal(g5,g4)
    c: Diameter(g5) = 3.25
    c: DistanceY(g5,g4) = 20.4
    c: DistanceX(g5,g4) = 0
    c: DistanceY(g1) = -307
    c: DistanceX(g1) = 11
    c: DistanceX(g1,g5) = 4
    c: DistanceY(g1,g5) = 2.5
FEATURE [Part::Extrusion] Extrude004  label="gpsHold"
  Base = -> Sketch020
  Dir = (0,0,1)
  DirMode = 2
  FaceMakerClass = Part::FaceMakerBullseye
  LengthFwd = 5
  LengthRev = 0
  Solid = true
  Symmetric = false
FEATURE [Sketcher::SketchObject] Sketch021
  FullyConstrained = true
  MapMode = 3
  Placement = pos=(0,0,0) rot=(1,0,0;1.5708rad)
  Support = -> [Extrude003]
  sketch-geometry (8):
    g0: LineSegment StartX=-25 StartY=-309 StartZ=0 EndX=-25 EndY=-301 EndZ=0
    g1: LineSegment StartX=-25 StartY=-301 StartZ=0 EndX=16.5 EndY=-301 EndZ=0
    g2: LineSegment StartX=16.5 StartY=-301 StartZ=0 EndX=16.5 EndY=-263 EndZ=0
    g3: LineSegment StartX=16.5 StartY=-263 StartZ=0 EndX=24.5 EndY=-263 EndZ=0
    g4: LineSegment StartX=24.5 StartY=-263 StartZ=0 EndX=24.5 EndY=-309 EndZ=0
    g5: LineSegment StartX=-25 StartY=-309 StartZ=0 EndX=24.5 EndY=-309 EndZ=0
    g6: Circle CenterX=-20.4 CenterY=-304.4 CenterZ=0 NormalX=0 NormalY=0 NormalZ=1 AngleXU=0 Radius=1.125
    g7: Circle CenterX=20.4 CenterY=-267.6 CenterZ=0 NormalX=0 NormalY=0 NormalZ=1 AngleXU=0 Radius=1.125
  constraints (24):
    c: Vertical(g0)
    c: Coincident(g1,g0)
    c: Horizontal(g1)
    c: Coincident(g2,g1)
    c: Vertical(g2)
    c: Coincident(g3,g2)
    c: Horizontal(g3)
    c: Coincident(g4,g3)
    c: Vertical(g4)
    c: Coincident(g5,g0)
    c: Coincident(g5,g4)
    c: Horizontal(g5)
    c: DistanceX(g0) = -25
    c: DistanceY(g0,g0) = 8
    c: DistanceX(g0,g1) = 41.5
    c: DistanceX(g1,g3) = 8
    c: DistanceY(g1,g2) = 38
    c: Equal(g7,g6)
    c: Diameter(g7) = 2.25
    c: DistanceX(g0,g6) = 4.6
    c: DistanceX(g6,g7) = 40.8
    c: DistanceY(g6,g7) = 36.8
    c: DistanceY(g0,g6) = 4.6
    c: DistanceY(g0) = -309
FEATURE [Part::Extrusion] Extrude005  label="ipsHold"
  Base = -> Sketch021
  Dir = (0,-1,2e-16)
  DirMode = 2
  FaceMakerClass = Part::FaceMakerBullseye
  LengthFwd = 5
  LengthRev = 0
  Placement = pos=(0,-262.5,0) rot=(0,0,1;0rad)
  Solid = true
  Symmetric = false
FEATURE [Sketcher::SketchObject] Sketch093  label="base010"
  FullyConstrained = true
  sketch-geometry (16):
    g0: LineSegment StartX=-41 StartY=-249 StartZ=0 EndX=41 EndY=-249 EndZ=0
    g1: LineSegment StartX=41 StartY=-249 StartZ=0 EndX=41 EndY=-321 EndZ=0
    g2: LineSegment StartX=41 StartY=-321 StartZ=0 EndX=-41 EndY=-321 EndZ=0
    g3: LineSegment StartX=-41 StartY=-249 StartZ=0 EndX=-41 EndY=-321 EndZ=0
    g4: Circle CenterX=-35 CenterY=-315 CenterZ=0 NormalX=0 NormalY=0 NormalZ=1 AngleXU=0 Radius=1.625
    g5: Circle CenterX=35 CenterY=-315 CenterZ=0 NormalX=0 NormalY=0 NormalZ=1 AngleXU=0 Radius=1.625
    g6: Circle CenterX=35 CenterY=-255 CenterZ=0 NormalX=0 NormalY=0 NormalZ=1 AngleXU=0 Radius=1.625
    g7: Circle CenterX=-35 CenterY=-255 CenterZ=0 NormalX=0 NormalY=0 NormalZ=1 AngleXU=0 Radius=1.625
    g8: ArcOfCircle CenterX=-7.5 CenterY=-288.5 CenterZ=0 NormalX=0 NormalY=0 NormalZ=1 AngleXU=0 Radius=5 StartAngle=0.694498 EndAngle=5.58869
    g9: ArcOfCircle CenterX=0 CenterY=-288.5 CenterZ=0 NormalX=0 NormalY=0 NormalZ=1 AngleXU=0 Radius=3.2 StartAngle=4.58731 EndAngle=7.97906
    g10: LineSegment StartX=-0.399218 StartY=-291.675 StartZ=0 EndX=-3.65813 EndY=-291.7 EndZ=0
    g11: LineSegment StartX=-0.399218 StartY=-285.325 StartZ=0 EndX=-3.65813 EndY=-285.3 EndZ=0
    g12: ArcOfCircle CenterX=-2 CenterY=-255 CenterZ=0 NormalX=0 NormalY=0 NormalZ=1 AngleXU=0 Radius=2 StartAngle=1.5708 EndAngle=4.71239
    g13: ArcOfCircle CenterX=2 CenterY=-255 CenterZ=0 NormalX=0 NormalY=0 NormalZ=1 AngleXU=0 Radius=3 StartAngle=4.71239 EndAngle=7.85398
    g14: LineSegment StartX=-2 StartY=-253 StartZ=0 EndX=2 EndY=-252 EndZ=0
    g15: LineSegment StartX=2 StartY=-258 StartZ=0 EndX=-2 EndY=-257 EndZ=0
  constraints (52):
    c: Coincident(g0,g1)
    c: Coincident(g1,g2)
    c: Horizontal(g0)
    c: Horizontal(g2)
    c: Vertical(g1)
    c: DistanceX(g2) = -41
    c: DistanceX(g1) = 41
    c: DistanceY(g2) = -321
    c: Coincident(g3,g0)
    c: Coincident(g3,g2)
    c: Vertical(g3)
    c: DistanceY(g3,g3) = 72
    c: Equal(g4,g5)
    c: Equal(g4,g6)
    c: Equal(g4,g7)
    c: Diameter(g4) = 3.25
    c: DistanceY(g4,g5) = 0
    c: DistanceX(g7,g4) = 0
    c: DistanceX(g5,g6) = 0
    c: DistanceY(g7,g6) = 0
    c: DistanceX(g4) = -35
    c: DistanceY(g4) = -315
    c: DistanceX(g5) = 35
    c: DistanceY(g7) = -255
    c: DistanceX(g8) = -7.5
    c: DistanceY(g8) = -288.5
    c: DistanceX(g8,g8) = 0
    c: DistanceY(g8,g8) = 6.4
    c: Diameter(g8) = 10
    c: PointOnObject(g9,g-2)
    c: DistanceY(g9,g9) = 6.35
    c: DistanceX(g9,g9) = 0
    c: DistanceY(g9) = -288.5
    c: Coincident(g10,g9)
    c: Coincident(g10,g8)
    c: Coincident(g11,g9)
    c: Coincident(g11,g8)
    c: Diameter(g9) = 6.4
    c: DistanceX(g12,g12) = 0
    c: DistanceX(g12,g12) = 0
    c: DistanceY(g12,g13) = 0
    c: DistanceY(g12) = -255
    c: Coincident(g14,g12)
    c: Coincident(g14,g13)
    c: Coincident(g15,g13)
    c: Coincident(g15,g12)
    c: DistanceX(g13,g13) = 0
    c: DistanceY(g13,g13) = 3
    c: DistanceX(g13,g13) = 0
    c: DistanceX(g12) = -2
    c: DistanceY(g12,g12) = 4
    c: DistanceX(g13) = 2
FEATURE [Part::Extrusion] Extrude030  label="base016"
  Base = -> Sketch093
  Dir = (0,0,1)
  DirMode = 2
  FaceMakerClass = Part::FaceMakerBullseye
  LengthFwd = 4.5
  LengthRev = 0
  Placement = pos=(0,0,-313.5) rot=(0,0,1;0rad)
  Solid = true
  Symmetric = false
FEATURE [Part::MultiFuse] Fusion078  label="base011"
  Shapes = -> [Extrude030,Extrude005,Extrude004,Extrude003]
FEATURE [Sketcher::SketchObject] Sketch094
  FullyConstrained = true
  sketch-geometry (4):
    g0: ArcOfCircle CenterX=-7.5 CenterY=-288.5 CenterZ=0 NormalX=0 NormalY=0 NormalZ=1 AngleXU=0 Radius=5 StartAngle=1.5708 EndAngle=4.71239
    g1: ArcOfCircle CenterX=0 CenterY=-288.5 CenterZ=0 NormalX=0 NormalY=0 NormalZ=1 AngleXU=0 Radius=5 StartAngle=4.71239 EndAngle=7.85398
    g2: LineSegment StartX=-7.5 StartY=-293.5 StartZ=0 EndX=-9e-16 EndY=-293.5 EndZ=0
    g3: LineSegment StartX=1.5e-15 StartY=-283.5 StartZ=0 EndX=-7.5 EndY=-283.5 EndZ=0
  constraints (10):
    c: Tangent(g0,g2) = -1.5708
    c: Tangent(g2,g1) = -1.5708
    c: Tangent(g1,g3) = -1.5708
    c: Tangent(g3,g0) = -1.5708
    c: Equal(g0,g1)
    c: Horizontal(g2)
    c: DistanceX(g1) = 0
    c: Diameter(g1) = 10
    c: DistanceX(g0) = -7.5
    c: DistanceY(g0) = -288.5
FEATURE [Part::Extrusion] Extrude031  label="baseMicCut"
  Base = -> Sketch094
  Dir = (0,0,1)
  DirMode = 2
  FaceMakerClass = Part::FaceMakerBullseye
  LengthFwd = 5
  LengthRev = 0
  Placement = pos=(0,0,-309.75) rot=(0,0,1;0rad)
  Solid = true
  Symmetric = false
FEATURE [Part::Cut] Cut035  label="base012"
  Base = -> Fusion078
  Tool = -> Extrude031
FEATURE [Part::Cone] Cone
  Angle = 360
  AttacherType = Attacher::AttachEngine3D
  Height = 1.5
  Placement = pos=(0,0,25.5) rot=(0,0,1;0rad)
  Radius1 = 4
  Radius2 = 3.5
FEATURE [Part::Cylinder] Cylinder020
  Angle = 360
  AttacherType = Attacher::AttachEngine3D
  FirstAngle = 0
  Height = 22
  Placement = pos=(0,0,5) rot=(0,0,1;0rad)
  Radius = 3.2
  SecondAngle = 0
FEATURE [Part::Cylinder] Cylinder021
  Angle = 360
  AttacherType = Attacher::AttachEngine3D
  FirstAngle = 0
  Height = 2
  Placement = pos=(0,0,5) rot=(0,0,1;0rad)
  Radius = 3.55
  SecondAngle = 0
FEATURE [Part::Cylinder] Cylinder022
  Angle = 360
  AttacherType = Attacher::AttachEngine3D
  FirstAngle = 0
  Height = 1
  Placement = pos=(0,0,11) rot=(0,0,1;0rad)
  Radius = 3.55
  SecondAngle = 0
FEATURE [Part::Cylinder] Cylinder023
  Angle = 360
  AttacherType = Attacher::AttachEngine3D
  FirstAngle = 0
  Height = 8
  Placement = pos=(0,0,12) rot=(0,0,1;0rad)
  Radius = 3.25
  SecondAngle = 0
FEATURE [Part::Cylinder] Cylinder024
  Angle = 360
  AttacherType = Attacher::AttachEngine3D
  FirstAngle = 0
  Height = 5.5
  Placement = pos=(0,0,20) rot=(0,0,1;0rad)
  Radius = 4
  SecondAngle = 0
FEATURE [Part::Cylinder] Cylinder025
  Angle = 360
  AttacherType = Attacher::AttachEngine3D
  FirstAngle = 0
  Height = 2
  Placement = pos=(0,0,3) rot=(0,0,1;0rad)
  Radius = 1
  SecondAngle = 0
FEATURE [Part::MultiFuse] Fusion002
  Shapes = -> [Cone,Cylinder020,Cylinder021,Cylinder022,Cylinder023,Cylinder024]
FEATURE [Part::MultiFuse] Fusion044  label="mic"
  Placement = pos=(0,-288.5,-302.5) rot=(0,1,0;3.14159rad)
  Shapes = -> [Cylinder025,Fusion002]
FEATURE [Part::Cone] Cone001
  Angle = 360
  AttacherType = Attacher::AttachEngine3D
  Height = 1.5
  Placement = pos=(0,0,25.5) rot=(0,0,1;0rad)
  Radius1 = 4
  Radius2 = 3.5
FEATURE [Part::Cylinder] Cylinder189
  Angle = 360
  AttacherType = Attacher::AttachEngine3D
  FirstAngle = 0
  Height = 22
  Placement = pos=(0,0,5) rot=(0,0,1;0rad)
  Radius = 3.2
  SecondAngle = 0
FEATURE [Part::Cylinder] Cylinder190
  Angle = 360
  AttacherType = Attacher::AttachEngine3D
  FirstAngle = 0
  Height = 2
  Placement = pos=(0,0,5) rot=(0,0,1;0rad)
  Radius = 3.55
  SecondAngle = 0
FEATURE [Part::Cylinder] Cylinder191
  Angle = 360
  AttacherType = Attacher::AttachEngine3D
  FirstAngle = 0
  Height = 1
  Placement = pos=(0,0,11) rot=(0,0,1;0rad)
  Radius = 3.55
  SecondAngle = 0
FEATURE [Part::Cylinder] Cylinder192
  Angle = 360
  AttacherType = Attacher::AttachEngine3D
  FirstAngle = 0
  Height = 8
  Placement = pos=(0,0,12) rot=(0,0,1;0rad)
  Radius = 3.25
  SecondAngle = 0
FEATURE [Part::Cylinder] Cylinder193
  Angle = 360
  AttacherType = Attacher::AttachEngine3D
  FirstAngle = 0
  Height = 5.5
  Placement = pos=(0,0,20) rot=(0,0,1;0rad)
  Radius = 4
  SecondAngle = 0
FEATURE [Part::Cylinder] Cylinder194
  Angle = 360
  AttacherType = Attacher::AttachEngine3D
  FirstAngle = 0
  Height = 2
  Placement = pos=(0,0,3) rot=(0,0,1;0rad)
  Radius = 1
  SecondAngle = 0
FEATURE [Part::MultiFuse] Fusion126
  Shapes = -> [Cone001,Cylinder189,Cylinder190,Cylinder191,Cylinder192,Cylinder193]
FEATURE [Part::MultiFuse] Fusion127  label="mic001"
  Placement = pos=(0,-260,-121.25) rot=(0,1,0;3.14159rad)
  Shapes = -> [Cylinder194,Fusion126]
FEATURE [Sketcher::SketchObject] Sketch154  label="base018"
  FullyConstrained = true
  Placement = pos=(0,0,-132.25) rot=(0,0,1;0rad)
  sketch-geometry (4):
    g0: ArcOfCircle CenterX=-7.5 CenterY=-260 CenterZ=0 NormalX=0 NormalY=0 NormalZ=1 AngleXU=0 Radius=5 StartAngle=0.694498 EndAngle=5.58869
    g1: ArcOfCircle CenterX=0 CenterY=-260 CenterZ=0 NormalX=0 NormalY=0 NormalZ=1 AngleXU=0 Radius=3.2 StartAngle=4.58731 EndAngle=7.97906
    g2: LineSegment StartX=-0.399218 StartY=-263.175 StartZ=0 EndX=-3.65813 EndY=-263.2 EndZ=0
    g3: LineSegment StartX=-0.399218 StartY=-256.825 StartZ=0 EndX=-3.65813 EndY=-256.8 EndZ=0
  constraints (14):
    c: DistanceX(g0) = -7.5
    c: DistanceY(g0) = -260
    c: DistanceX(g0,g0) = 0
    c: DistanceY(g0,g0) = 6.4
    c: Diameter(g0) = 10
    c: PointOnObject(g1,g-2)
    c: DistanceY(g1,g1) = 6.35
    c: DistanceX(g1,g1) = 0
    c: DistanceY(g1) = -260
    c: Coincident(g2,g1)
    c: Coincident(g2,g0)
    c: Coincident(g3,g1)
    c: Coincident(g3,g0)
    c: Diameter(g1) = 6.4
FEATURE [Part::Extrusion] Extrude054  label="micCut"
  Base = -> Sketch154
  Dir = (0,0,1)
  DirMode = 2
  FaceMakerClass = Part::FaceMakerBullseye
  LengthFwd = 4
  LengthRev = 0
  Solid = true
  Symmetric = false
FEATURE [Part::Cut] Cut066  label="base019"
  Base = -> Fusion125
  Tool = -> Extrude054
FEATURE [Sketcher::SketchObject] Sketch155
  FullyConstrained = true
  Placement = pos=(0,-295,0) rot=(1,0,0;1.5708rad)
  sketch-geometry (14):
    g0: LineSegment StartX=28 StartY=-309 StartZ=0 EndX=28 EndY=-301 EndZ=0
    g1: LineSegment StartX=-19 StartY=-309 StartZ=0 EndX=28 EndY=-309 EndZ=0
    g2: LineSegment StartX=-19 StartY=-309 StartZ=0 EndX=-19 EndY=-284 EndZ=0
    g3: LineSegment StartX=-19 StartY=-284 StartZ=0 EndX=-13 EndY=-284 EndZ=0
    g4: LineSegment StartX=-13 StartY=-284 StartZ=0 EndX=-13 EndY=-301 EndZ=0
    g5: Circle CenterX=-15.96 CenterY=-286.8 CenterZ=0 NormalX=0 NormalY=0 NormalZ=1 AngleXU=0 Radius=1.125
    g6: Circle CenterX=-0.15 CenterY=-304.37 CenterZ=0 NormalX=0 NormalY=0 NormalZ=1 AngleXU=0 Radius=1.125
    g7: Circle CenterX=20.15 CenterY=-304.37 CenterZ=0 NormalX=0 NormalY=0 NormalZ=1 AngleXU=0 Radius=1.125
    g8: LineSegment StartX=-13 StartY=-301 StartZ=0 EndX=11 EndY=-301 EndZ=0
    g9: LineSegment StartX=11 StartY=-301 StartZ=0 EndX=11 EndY=-263 EndZ=0
    g10: LineSegment StartX=11 StartY=-263 StartZ=0 EndX=19 EndY=-263 EndZ=0
    g11: LineSegment StartX=19 StartY=-263 StartZ=0 EndX=19 EndY=-301 EndZ=0
    g12: LineSegment StartX=19 StartY=-301 StartZ=0 EndX=28 EndY=-301 EndZ=0
    g13: Circle CenterX=16.04 CenterY=-270.55 CenterZ=0 NormalX=0 NormalY=0 NormalZ=1 AngleXU=0 Radius=1.125
  constraints (42):
    c: Vertical(g0)
    c: Coincident(g1,g0)
    c: Horizontal(g1)
    c: DistanceX(g0) = 28
    c: Vertical(g2)
    c: Coincident(g3,g2)
    c: Horizontal(g3)
    c: Coincident(g4,g3)
    c: Vertical(g4)
    c: DistanceY(g1,g6) = 4.63
    c: DistanceY(g6,g7) = 0
    c: DistanceX(g6,g7) = 20.3
    c: DistanceY(g1) = -309
    c: Coincident(g2,g1)
    c: Coincident(g8,g4)
    c: Horizontal(g8)
    c: DistanceX(g4) = -13
    c: Vertical(g9)
    c: Distance(g3) = 6
    c: Coincident(g10,g9)
    c: Horizontal(g10)
    c: Coincident(g11,g10)
    c: Vertical(g11)
    c: Coincident(g12,g0)
    c: Horizontal(g12)
    c: DistanceY(g8,g11) = 0
    c: Coincident(g11,g12)
    c: DistanceX(g10) = 19
    c: DistanceX(g10,g10) = 8
    c: Coincident(g8,g9)
    c: DistanceY(g9) = -263
    c: DistanceY(g1,g4) = 8
    c: DistanceY(g1,g2) = 25
    c: DistanceX(g5,g13) = 32
    c: DistanceY(g5,g13) = 16.25
    c: DistanceY(g1,g5) = 22.2
    c: DistanceX(g1,g5) = 3.04
    c: Equal(g6,g7)
    c: Equal(g6,g5)
    c: Equal(g6,g13)
    c: Diameter(g6) = 2.25
    c: DistanceX(g6) = -0.15
FEATURE [Part::Extrusion] Extrude055  label="i2cHold001"
  Base = -> Sketch155
  Dir = (0,-1,2e-16)
  DirMode = 2
  FaceMakerClass = Part::FaceMakerBullseye
  LengthFwd = 5
  LengthRev = 0
  Solid = true
  Symmetric = false
FEATURE [Sketcher::SketchObject] Sketch156
  AttachmentOffset = pos=(0,0,274) rot=(0,0,1;0rad)
  FullyConstrained = true
  MapMode = 3
  Placement = pos=(0,-274,6.08e-14) rot=(1,0,0;1.5708rad)
  Support = -> [Extrude055]
  sketch-geometry (10):
    g0: LineSegment StartX=-24.4 StartY=-132.25 StartZ=0 EndX=-24.4 EndY=-113.4 EndZ=0
    g1: LineSegment StartX=16.4 StartY=-132.25 StartZ=0 EndX=16.4 EndY=-76.6 EndZ=0
    g2: LineSegment StartX=16.4 StartY=-76.6 StartZ=0 EndX=24.4 EndY=-76.6 EndZ=0
    g3: LineSegment StartX=24.4 StartY=-76.6 StartZ=0 EndX=24.4 EndY=-132.25 EndZ=0
    g4: Circle CenterX=-20.4 CenterY=-117.4 CenterZ=0 NormalX=0 NormalY=0 NormalZ=1 AngleXU=0 Radius=1.125
    g5: Circle CenterX=20.4 CenterY=-80.6 CenterZ=0 NormalX=0 NormalY=0 NormalZ=1 AngleXU=0 Radius=1.125
    g6: LineSegment StartX=-24.4 StartY=-113.4 StartZ=0 EndX=-16.4 EndY=-113.4 EndZ=0
    g7: LineSegment StartX=-16.4 StartY=-113.4 StartZ=0 EndX=-16.4 EndY=-132.25 EndZ=0
    g8: LineSegment StartX=-24.4 StartY=-132.25 StartZ=0 EndX=-16.4 EndY=-132.25 EndZ=0
    g9: LineSegment StartX=16.4 StartY=-132.25 StartZ=0 EndX=24.4 EndY=-132.25 EndZ=0
  constraints (30):
    c: Vertical(g0)
    c: Vertical(g1)
    c: Coincident(g2,g1)
    c: Horizontal(g2)
    c: Coincident(g3,g2)
    c: Vertical(g3)
    c: DistanceX(g1,g2) = 8
    c: Equal(g5,g4)
    c: Diameter(g5) = 2.25
    c: DistanceY(g4,g5) = 36.8
    c: DistanceY(g0) = -132.25
    c: Coincident(g6,g0)
    c: Horizontal(g6)
    c: Vertical(g7)
    c: Coincident(g8,g0)
    c: Coincident(g8,g7)
    c: Horizontal(g8)
    c: Coincident(g9,g1)
    c: Coincident(g9,g3)
    c: Horizontal(g9)
    c: DistanceY(g0,g1) = 0
    c: DistanceX(g6,g6) = 8
    c: DistanceX(g4) = -20.4
    c: DistanceX(g5) = 20.4
    c: DistanceY(g0,g4) = 14.85
    c: DistanceX(g0,g4) = 4
    c: Coincident(g6,g7)
    c: DistanceY(g5,g1) = 4
    c: DistanceY(g4,g0) = 4
    c: DistanceX(g1,g5) = 4
FEATURE [Part::Extrusion] Extrude056  label="ips7100"
  Base = -> Sketch156
  Dir = (0,-1,2e-16)
  DirMode = 2
  FaceMakerClass = Part::FaceMakerBullseye
  LengthFwd = 8
  LengthRev = 0
  Reversed = true
  Solid = true
  Symmetric = false
FEATURE [Sketcher::SketchObject] Sketch157  label="bmeHold"
  FullyConstrained = true
  Placement = pos=(0,-342,0) rot=(1,0,0;1.5708rad)
  sketch-geometry (10):
    g0: Circle CenterX=-0.15 CenterY=-117.75 CenterZ=0 NormalX=0 NormalY=0 NormalZ=1 AngleXU=0 Radius=1.125
    g1: Circle CenterX=20.15 CenterY=-117.75 CenterZ=0 NormalX=0 NormalY=0 NormalZ=1 AngleXU=0 Radius=1.125
    g2: LineSegment StartX=-4.15 StartY=-113.75 StartZ=0 EndX=3.85 EndY=-113.75 EndZ=0
    g3: LineSegment StartX=3.85 StartY=-113.75 StartZ=0 EndX=3.85 EndY=-132.25 EndZ=0
    g4: LineSegment StartX=3.85 StartY=-132.25 StartZ=0 EndX=-4.15 EndY=-132.25 EndZ=0
    g5: LineSegment StartX=-4.15 StartY=-132.25 StartZ=0 EndX=-4.15 EndY=-113.75 EndZ=0
    g6: LineSegment StartX=16.15 StartY=-113.75 StartZ=0 EndX=24.15 EndY=-113.75 EndZ=0
    g7: LineSegment StartX=24.15 StartY=-113.75 StartZ=0 EndX=24.15 EndY=-132.25 EndZ=0
    g8: LineSegment StartX=24.15 StartY=-132.25 StartZ=0 EndX=16.15 EndY=-132.25 EndZ=0
    g9: LineSegment StartX=16.15 StartY=-132.25 StartZ=0 EndX=16.15 EndY=-113.75 EndZ=0
  constraints (30):
    c: DistanceY(g0,g1) = 0
    c: DistanceX(g0,g1) = 20.3
    c: Equal(g0,g1)
    c: Diameter(g0) = 2.25
    c: DistanceX(g0) = -0.15
    c: Coincident(g2,g3)
    c: Coincident(g3,g4)
    c: Coincident(g4,g5)
    c: Coincident(g5,g2)
    c: Horizontal(g2)
    c: Horizontal(g4)
    c: Vertical(g3)
    c: Vertical(g5)
    c: Coincident(g6,g7)
    c: Coincident(g7,g8)
    c: Coincident(g8,g9)
    c: Coincident(g9,g6)
    c: Horizontal(g6)
    c: Horizontal(g8)
    c: Vertical(g7)
    c: Vertical(g9)
    c: DistanceY(g4) = -132.25
    c: DistanceX(g4,g0) = 4
    c: DistanceX(g0,g2) = 4
    c: DistanceY(g0,g2) = 4
    c: DistanceY(g2,g6) = 0
    c: DistanceX(g6,g1) = 4
    c: DistanceX(g1,g6) = 4
    c: DistanceY(g3,g8) = 0
    c: DistanceY(g4,g0) = 14.5
FEATURE [Sketcher::SketchObject] Sketch158  label="scdHold"
  FullyConstrained = true
  Placement = pos=(0,-312,0) rot=(1,0,0;1.5708rad)
  sketch-geometry (10):
    g0: Circle CenterX=-16.23 CenterY=-116.8 CenterZ=0 NormalX=0 NormalY=0 NormalZ=1 AngleXU=0 Radius=1.125
    g1: Circle CenterX=15.77 CenterY=-100.55 CenterZ=0 NormalX=0 NormalY=0 NormalZ=1 AngleXU=0 Radius=1.125
    g2: LineSegment StartX=-20.23 StartY=-112.8 StartZ=0 EndX=-12.23 EndY=-112.8 EndZ=0
    g3: LineSegment StartX=-12.23 StartY=-112.8 StartZ=0 EndX=-12.23 EndY=-132.25 EndZ=0
    g4: LineSegment StartX=-12.23 StartY=-132.25 StartZ=0 EndX=-20.23 EndY=-132.25 EndZ=0
    g5: LineSegment StartX=-20.23 StartY=-132.25 StartZ=0 EndX=-20.23 EndY=-112.8 EndZ=0
    g6: LineSegment StartX=11.77 StartY=-96.55 StartZ=0 EndX=19.77 EndY=-96.55 EndZ=0
    g7: LineSegment StartX=19.77 StartY=-96.55 StartZ=0 EndX=19.77 EndY=-132.25 EndZ=0
    g8: LineSegment StartX=19.77 StartY=-132.25 StartZ=0 EndX=11.77 EndY=-132.25 EndZ=0
    g9: LineSegment StartX=11.77 StartY=-132.25 StartZ=0 EndX=11.77 EndY=-96.55 EndZ=0
  constraints (30):
    c: DistanceX(g0,g1) = 32
    c: DistanceY(g0,g1) = 16.25
    c: Coincident(g2,g3)
    c: Coincident(g3,g4)
    c: Coincident(g4,g5)
    c: Coincident(g5,g2)
    c: Horizontal(g2)
    c: Horizontal(g4)
    c: Vertical(g3)
    c: Vertical(g5)
    c: Coincident(g6,g7)
    c: Coincident(g7,g8)
    c: Coincident(g8,g9)
    c: Coincident(g9,g6)
    c: Horizontal(g6)
    c: Horizontal(g8)
    c: Vertical(g7)
    c: Vertical(g9)
    c: DistanceY(g4) = -132.25
    c: DistanceY(g4,g0) = 15.45
    c: DistanceY(g0,g2) = 4
    c: DistanceX(g2,g0) = 4
    c: DistanceX(g0,g2) = 4
    c: DistanceX(g0) = -16.23
    c: DistanceX(g6,g1) = 4
    c: DistanceX(g1,g6) = 4
    c: DistanceY(g1,g6) = 4
    c: DistanceY(g8,g3) = 0
    c: Equal(g1,g0)
    c: Diameter(g1) = 2.25
FEATURE [Part::Feature] Part__Feature105  label="Printed Circuit Board"
  shape: bbox 25.4 x 17.78 x 1.6 mm, 42 faces (baked)
FEATURE [Part::Feature] Part__Feature106  label="EAHC2835WD6"
  shape: bbox 3.513 x 2.813 x 0.7485 mm, 108 faces, 4 solids (baked)
FEATURE [Part::Feature] Part__Feature107  label="AS7341 v2"
  Placement = pos=(0,-0.339822,1.6) rot=(0,0,1;0rad)
  shape: bbox 2 x 3.1 x 1.1 mm, 267 faces, 26 solids (baked)
FEATURE [Part::Feature] Part__Feature108  label="CAPC-0805-T0.95-BN v1"
  Placement = pos=(-5.01759,-3.15294,1.6) rot=(0,0,1;0rad)
  shape: bbox 2.1 x 1.35 x 0.95 mm, 42 faces (baked)
FEATURE [Part::Feature] Part__Feature109  label="CAPC-0805-T0.95-BN v002"
  Placement = pos=(-5.48627,2.66154,1.6) rot=(0,0,-1;1.5708rad)
  shape: bbox 1.35 x 2.1 x 0.95 mm, 42 faces (baked)
FEATURE [Part::Feature] Part__Feature110  label="CAPC-0805-T0.95-BN v003"
  Placement = pos=(-3.43627,2.66154,1.6) rot=(0,0,-1;1.5708rad)
  shape: bbox 1.35 x 2.1 x 0.95 mm, 42 faces (baked)
FEATURE [Part::Feature] Part__Feature111  label="CAPC-0603-T0.9-BN v1"
  Placement = pos=(-1.69987,-3.28475,1.6) rot=(0,0,1;0rad)
  shape: bbox 1.7 x 0.9 x 0.9 mm, 42 faces (baked)
FEATURE [Part::Feature] Part__Feature112  label="BODY_MF06A"
  Placement = pos=(0,0,0.762) rot=(0.57735,-0.57735,-0.57735;2.0944rad)
  shape: bbox 1.601 x 2.921 x 1.016 mm, 42 faces (baked)
FEATURE [Part::Feature] Part__Feature113  label="LEAD_MF06A"
  Placement = pos=(-0.9652,-0.9525,0.1016) rot=(0.57735,-0.57735,-0.57735;2.0944rad)
  shape: bbox 0.6223 x 0.3749 x 0.8636 mm, 14 faces (baked)
FEATURE [Part::Feature] Part__Feature114  label="LEAD_MF06A001"
  Placement = pos=(-0.9652,0,0.1016) rot=(0.57735,-0.57735,-0.57735;2.0944rad)
  shape: bbox 0.6223 x 0.3749 x 0.8636 mm, 14 faces (baked)
FEATURE [Part::Feature] Part__Feature115  label="LEAD_MF06A002"
  Placement = pos=(-0.9652,0.9525,0.1016) rot=(0.57735,-0.57735,-0.57735;2.0944rad)
  shape: bbox 0.6223 x 0.3749 x 0.8636 mm, 14 faces (baked)
FEATURE [Part::Feature] Part__Feature116  label="LEAD_MF06A003"
  Placement = pos=(0.9652,-0.9525,0.1016) rot=(0.57735,0.57735,0.57735;2.0944rad)
  shape: bbox 0.6223 x 0.3749 x 0.8636 mm, 14 faces (baked)
FEATURE [Part::Feature] Part__Feature117  label="LEAD_MF06A004"
  Placement = pos=(0.9652,0,0.1016) rot=(0.57735,0.57735,0.57735;2.0944rad)
  shape: bbox 0.6223 x 0.3749 x 0.8636 mm, 14 faces (baked)
FEATURE [Part::Feature] Part__Feature118  label="LEAD_MF06A005"
  Placement = pos=(0.9652,0.9525,0.1016) rot=(0.57735,0.57735,0.57735;2.0944rad)
  shape: bbox 0.6223 x 0.3749 x 0.8636 mm, 14 faces (baked)
FEATURE [Part::Feature] Part__Feature119  label="SOT363 v2"
  Placement = pos=(4.97054,-0.645171,1.675) rot=(0,0,1;3.14159rad)
  shape: bbox 2.1 x 2 x 1.1 mm, 94 faces, 7 solids (baked)
FEATURE [Part::Feature] Part__Feature120  label="LED 0603 single color v1"
  Placement = pos=(-9.18406,3.72778,1.60762) rot=(0,0,1;1.5708rad)
  shape: bbox 1.961 x 0.7932 x 0.7145 mm, 63 faces, 5 solids (baked)
FEATURE [Part::Feature] Part__Feature121  label="RESC-0603 v1"
  Placement = pos=(4.83432,-3.67461,1.6) rot=(0,0,1;0rad)
  shape: bbox 1.7 x 0.9 x 0.55 mm, 52 faces, 3 solids (baked)
FEATURE [Part::Feature] Part__Feature122  label="RESC-0603 v002"
  Placement = pos=(-7.14949,3.61248,1.6) rot=(0,0,-1;1.5708rad)
  shape: bbox 0.9 x 1.7 x 0.55 mm, 52 faces, 3 solids (baked)
FEATURE [Part::Feature] Part__Feature123  label="YC164_RESPACK v1"
  Placement = pos=(2.99591,1.52916,1.6) rot=(0,0,1;0rad)
  shape: bbox 3.2 x 1.6 x 0.61 mm, 172 faces (baked)
FEATURE [Part::Feature] Part__Feature124  label="qwicc v2"
  Placement = pos=(-10.8364,0.0607456,1.65) rot=(0,0,-1;1.5708rad)
  shape: bbox 4.95 x 6 x 2.96 mm, 229 faces, 7 solids (baked)
FEATURE [Part::Feature] Part__Feature125  label="qwicc v003"
  Placement = pos=(10.8256,0.00556102,1.65) rot=(0,0,1;1.5708rad)
  shape: bbox 4.95 x 6 x 2.96 mm, 229 faces, 7 solids (baked)
FEATURE [App::Part] sot_23_6_v2  label="sot-23-6 v2"
  Group = -> [Part__Feature112,Part__Feature113,Part__Feature114,Part__Feature115,Part__Feature116,Part__Feature117,Part__Feature118]
  Origin = -> Origin059
  Placement = pos=(-4.47945,-0.603742,1.69152) rot=(0,0,1;0rad)
FEATURE [Part::Extrusion] Extrude057  label="bmeHold001"
  Base = -> Sketch157
  Dir = (0,-1,2e-16)
  DirMode = 2
  FaceMakerClass = Part::FaceMakerBullseye
  LengthFwd = 8
  LengthRev = 0
  Reversed = true
  Solid = true
  Symmetric = false
FEATURE [Part::Extrusion] Extrude058  label="scdHold001"
  Base = -> Sketch158
  Dir = (0,-1,2e-16)
  DirMode = 2
  FaceMakerClass = Part::FaceMakerBullseye
  LengthFwd = 8
  LengthRev = 0
  Reversed = true
  Solid = true
  Symmetric = false
FEATURE [Part::MultiFuse] Fusion128  label="base020"
  Shapes = -> [Extrude058,Extrude057,Extrude056,Cut066]
FEATURE [App::Part] Adafruit_AS7341_STEMMA_QT_v2  label="bme280"
  Group = -> [Part__Feature105,Part__Feature106,Part__Feature107,Part__Feature108,Part__Feature109,Part__Feature110,Part__Feature111,sot_23_6_v2,Part__Feature119,Part__Feature120,Part__Feature121,Part__Feature122,Part__Feature123,Part__Feature124,Part__Feature125]
  Origin = -> Origin060
  Placement = pos=(10,-343,-111.4) rot=(-1,0,0;4.71239rad)
FEATURE [Sketcher::SketchObject] Sketch161  label="SketchTop020"
  FullyConstrained = true
  sketch-geometry (17):
    g0: LineSegment StartX=42.5 StartY=-358.496 StartZ=0 EndX=68.7664 EndY=-277.656 EndZ=0
    g1: LineSegment StartX=68.7664 StartY=-277.656 StartZ=0 EndX=0 EndY=-227.695 EndZ=0
    g2: LineSegment StartX=0 StartY=-227.695 StartZ=0 EndX=-68.7664 EndY=-277.656 EndZ=0
    g3: LineSegment StartX=-68.7664 StartY=-277.656 StartZ=0 EndX=-42.5 EndY=-358.496 EndZ=0
    g4: LineSegment StartX=-42.5 StartY=-358.496 StartZ=0 EndX=42.5 EndY=-358.496 EndZ=0
    g5: Circle CenterX=0 CenterY=-300 CenterZ=0 NormalX=0 NormalY=0 NormalZ=1 AngleXU=0 Radius=72.3053
    g6: LineSegment StartX=-34.3832 StartY=-252.676 StartZ=0 EndX=-55.6332 EndY=-318.076 EndZ=0
    g7: LineSegment StartX=-55.6332 StartY=-318.076 StartZ=0 EndX=0 EndY=-358.496 EndZ=0
    g8: LineSegment StartX=0 StartY=-358.496 StartZ=0 EndX=55.6332 EndY=-318.076 EndZ=0
    g9: LineSegment StartX=55.6332 StartY=-318.076 StartZ=0 EndX=34.3832 EndY=-252.676 EndZ=0
    g10: LineSegment StartX=34.3832 StartY=-252.676 StartZ=0 EndX=-34.3832 EndY=-252.676 EndZ=0
    g11: Circle CenterX=0 CenterY=-300 CenterZ=0 NormalX=0 NormalY=0 NormalZ=1 AngleXU=0 Radius=58.4962
    g12: Circle CenterX=34.3832 CenterY=-252.676 CenterZ=0 NormalX=0 NormalY=0 NormalZ=1 AngleXU=0 Radius=6
    g13: Circle CenterX=55.6332 CenterY=-318.076 CenterZ=0 NormalX=0 NormalY=0 NormalZ=1 AngleXU=0 Radius=6
    g14: Circle CenterX=0 CenterY=-358.496 CenterZ=0 NormalX=0 NormalY=0 NormalZ=1 AngleXU=0 Radius=6
    g15: Circle CenterX=-55.6332 CenterY=-318.076 CenterZ=0 NormalX=0 NormalY=0 NormalZ=1 AngleXU=0 Radius=6
    g16: Circle CenterX=-34.3832 CenterY=-252.676 CenterZ=0 NormalX=0 NormalY=0 NormalZ=1 AngleXU=0 Radius=6
  constraints (39):
    c: Coincident(g0,g1)
    c: Coincident(g1,g2)
    c: Coincident(g2,g3)
    c: Coincident(g3,g4)
    c: Coincident(g4,g0)
    c: Equal(g0, g1-g4) x4
    c: PointOnObject(g0,g5)
    c: PointOnObject(g1,g5)
    c: PointOnObject(g2,g5)
    c: PointOnObject(g3,g5)
    c: PointOnObject(g4,g5)
    c: Horizontal(g4)
    c: DistanceY(g5) = -300
    c: DistanceX(g5) = 0
    c: DistanceX(g4,g4) = 85
    c: Coincident(g6,g7)
    c: Coincident(g7,g8)
    c: Coincident(g8,g9)
    c: Coincident(g9,g10)
    c: Coincident(g10,g6)
    c: Equal(g6, g7-g10) x4
    c: PointOnObject(g6,g11)
    c: PointOnObject(g7,g11)
    c: PointOnObject(g8,g11)
    c: PointOnObject(g9,g11)
    c: PointOnObject(g10,g11)
    c: Coincident(g11,g5)
    c: PointOnObject(g10,g2)
    c: Horizontal(g10)
    c: Coincident(g12,g9)
    c: Coincident(g13,g8)
    c: Coincident(g14,g7)
    c: Coincident(g15,g6)
    c: Coincident(g16,g6)
    c: Equal(g13,g14)
    c: Equal(g13,g15)
    c: Equal(g13,g16)
    c: Equal(g13,g12)
    c: Diameter(g13) = 12
FEATURE [Sketcher::SketchObject] Sketch160  label="m4Mounts"
  FullyConstrained = true
  Placement = pos=(0,0,-145) rot=(0,0,1;0rad)
  sketch-geometry (4):
    g0: Circle CenterX=34.38 CenterY=-252.68 CenterZ=0 NormalX=0 NormalY=0 NormalZ=1 AngleXU=0 Radius=6
    g1: Circle CenterX=55.63 CenterY=-318.08 CenterZ=0 NormalX=0 NormalY=0 NormalZ=1 AngleXU=0 Radius=6
    g2: Circle CenterX=-55.63 CenterY=-318.08 CenterZ=0 NormalX=0 NormalY=0 NormalZ=1 AngleXU=0 Radius=6
    g3: Circle CenterX=-34.38 CenterY=-252.68 CenterZ=0 NormalX=0 NormalY=0 NormalZ=1 AngleXU=0 Radius=6
  constraints (12):
    c: Equal(g1,g2)
    c: Equal(g1,g3)
    c: Equal(g1,g0)
    c: Diameter(g1) = 12
    c: DistanceY(g1) = -318.08
    c: DistanceY(g0) = -252.68
    c: DistanceY(g3) = -252.68
    c: DistanceX(g3) = -34.38
    c: DistanceX(g0) = 34.38
    c: DistanceX(g1) = 55.63
    c: DistanceX(g2) = -55.63
    c: DistanceY(g2) = -318.08
FEATURE [Part::Feature] Part__Feature240  label="90695A033_Steel Thin Hex Nut"
  Placement = pos=(0,-358.5,-127.25) rot=(0,0,1;0rad)
  shape: bbox 6.352 x 6.352 x 2.188 mm, 35 faces (baked)
FEATURE [Part::Feature] Part__Feature243  label="90348A009_18-8 Stainless Steel Socket Head Screws"
  Placement = pos=(0,-358.5,-125.25) rot=(0,0,1;0rad)
  shape: bbox 5.501 x 5.501 x 23.02 mm, 189 faces (baked)
FEATURE [Sketcher::SketchObject] Sketch162  label="m4Mounts003"
  FullyConstrained = true
  Placement = pos=(0,0,-128.5) rot=(0,0,1;0rad)
  sketch-geometry (28):
    g0: LineSegment StartX=-55.63 StartY=-314.455 StartZ=0 EndX=-58.7693 EndY=-316.267 EndZ=0
    g1: LineSegment StartX=-58.7693 StartY=-316.267 StartZ=0 EndX=-58.7693 EndY=-319.892 EndZ=0
    g2: LineSegment StartX=-58.7693 StartY=-319.892 StartZ=0 EndX=-55.63 EndY=-321.705 EndZ=0
    g3: LineSegment StartX=-55.63 StartY=-321.705 StartZ=0 EndX=-52.4907 EndY=-319.892 EndZ=0
    g4: LineSegment StartX=-52.4907 StartY=-319.892 StartZ=0 EndX=-52.4907 EndY=-316.267 EndZ=0
    g5: LineSegment StartX=-52.4907 StartY=-316.267 StartZ=0 EndX=-55.63 EndY=-314.455 EndZ=0
    g6: Circle CenterX=-55.63 CenterY=-318.08 CenterZ=0 NormalX=0 NormalY=0 NormalZ=1 AngleXU=0 Radius=3.625
    g7: LineSegment StartX=55.63 StartY=-314.455 StartZ=0 EndX=52.4907 EndY=-316.267 EndZ=0
    g8: LineSegment StartX=52.4907 StartY=-316.267 StartZ=0 EndX=52.4907 EndY=-319.892 EndZ=0
    g9: LineSegment StartX=52.4907 StartY=-319.892 StartZ=0 EndX=55.63 EndY=-321.705 EndZ=0
    g10: LineSegment StartX=55.63 StartY=-321.705 StartZ=0 EndX=58.7693 EndY=-319.892 EndZ=0
    g11: LineSegment StartX=58.7693 StartY=-319.892 StartZ=0 EndX=58.7693 EndY=-316.267 EndZ=0
    g12: LineSegment StartX=58.7693 StartY=-316.267 StartZ=0 EndX=55.63 EndY=-314.455 EndZ=0
    g13: Circle CenterX=55.63 CenterY=-318.08 CenterZ=0 NormalX=0 NormalY=0 NormalZ=1 AngleXU=0 Radius=3.625
    g14: LineSegment StartX=34.38 StartY=-249.055 StartZ=0 EndX=31.2407 EndY=-250.868 EndZ=0
    g15: LineSegment StartX=31.2407 StartY=-250.868 StartZ=0 EndX=31.2407 EndY=-254.493 EndZ=0
    g16: LineSegment StartX=31.2407 StartY=-254.493 StartZ=0 EndX=34.38 EndY=-256.305 EndZ=0
    g17: LineSegment StartX=34.38 StartY=-256.305 StartZ=0 EndX=37.5193 EndY=-254.493 EndZ=0
    g18: LineSegment StartX=37.5193 StartY=-254.493 StartZ=0 EndX=37.5193 EndY=-250.868 EndZ=0
    g19: LineSegment StartX=37.5193 StartY=-250.868 StartZ=0 EndX=34.38 EndY=-249.055 EndZ=0
    g20: Circle CenterX=34.38 CenterY=-252.68 CenterZ=0 NormalX=0 NormalY=0 NormalZ=1 AngleXU=0 Radius=3.625
    g21: LineSegment StartX=-34.38 StartY=-249.055 StartZ=0 EndX=-37.5193 EndY=-250.868 EndZ=0
    g22: LineSegment StartX=-37.5193 StartY=-250.868 StartZ=0 EndX=-37.5193 EndY=-254.493 EndZ=0
    g23: LineSegment StartX=-37.5193 StartY=-254.493 StartZ=0 EndX=-34.38 EndY=-256.305 EndZ=0
    g24: LineSegment StartX=-34.38 StartY=-256.305 StartZ=0 EndX=-31.2407 EndY=-254.493 EndZ=0
    g25: LineSegment StartX=-31.2407 StartY=-254.493 StartZ=0 EndX=-31.2407 EndY=-250.868 EndZ=0
    g26: LineSegment StartX=-31.2407 StartY=-250.868 StartZ=0 EndX=-34.38 EndY=-249.055 EndZ=0
    g27: Circle CenterX=-34.38 CenterY=-252.68 CenterZ=0 NormalX=0 NormalY=0 NormalZ=1 AngleXU=0 Radius=3.625
  constraints (68):
    c: Coincident(g0,g1)
    c: Coincident(g1,g2)
    c: Coincident(g2,g3)
    c: Coincident(g3,g4)
    c: Coincident(g4,g5)
    c: Coincident(g5,g0)
    c: Equal(g0, g1-g5) x5
    c: PointOnObject(g0,g6)
    c: PointOnObject(g1,g6)
    c: PointOnObject(g2,g6)
    c: PointOnObject(g3,g6)
    c: PointOnObject(g4,g6)
    c: PointOnObject(g5,g6)
    c: Coincident(g7,g8)
    c: Coincident(g8,g9)
    c: Coincident(g9,g10)
    c: Coincident(g10,g11)
    c: Coincident(g11,g12)
    c: Coincident(g12,g7)
    c: Equal(g7, g8-g12) x5
    c: PointOnObject(g7,g13)
    c: PointOnObject(g8,g13)
    c: PointOnObject(g9,g13)
    c: PointOnObject(g10,g13)
    c: PointOnObject(g11,g13)
    c: PointOnObject(g12,g13)
    c: Coincident(g14,g15)
    c: Coincident(g15,g16)
    c: Coincident(g16,g17)
    c: Coincident(g17,g18)
    c: Coincident(g18,g19)
    c: Coincident(g19,g14)
    c: Equal(g14, g15-g19) x5
    c: PointOnObject(g14,g20)
    c: PointOnObject(g15,g20)
    c: PointOnObject(g16,g20)
    c: PointOnObject(g17,g20)
    c: PointOnObject(g18,g20)
    c: PointOnObject(g19,g20)
    c: Coincident(g21,g22)
    c: Coincident(g22,g23)
    c: Coincident(g23,g24)
    c: Coincident(g24,g25)
    c: Coincident(g25,g26)
    c: Coincident(g26,g21)
    c: Equal(g21, g22-g26) x5
    c: PointOnObject(g21,g27)
    c: PointOnObject(g22,g27)
    c: PointOnObject(g23,g27)
    c: PointOnObject(g24,g27)
    c: PointOnObject(g25,g27)
    c: PointOnObject(g26,g27)
    c: Vertical(g1)
    c: Vertical(g8)
    c: Vertical(g22)
    c: Vertical(g15)
    c: DistanceY(g6,g13) = 0
    c: DistanceY(g6) = -318.08
    c: DistanceY(g27,g20) = 0
    c: DistanceY(g27) = -252.68
    c: DistanceX(g27) = -34.38
    c: DistanceX(g20) = 34.38
    c: DistanceX(g6) = -55.63
    c: DistanceX(g13) = 55.63
    c: Equal(g13,g20)
    c: Equal(g13,g27)
    c: Equal(g13,g6)
    c: Diameter(g13) = 7.25
FEATURE [Part::Extrusion] Extrude060  label="m4NutCutsFinal"
  Base = -> Sketch162
  Dir = (0,0,1)
  DirMode = 2
  FaceMakerClass = Part::FaceMakerBullseye
  LengthFwd = 1.5
  LengthRev = 0
  Solid = true
  Symmetric = false
FEATURE [Part::Extrusion] Extrude059  label="m4Mounts001"
  Base = -> Sketch160
  Dir = (0,0,1)
  DirMode = 2
  FaceMakerClass = Part::FaceMakerBullseye
  LengthFwd = 16.75
  LengthRev = 0
  Solid = true
  Symmetric = false
FEATURE [Sketcher::SketchObject] Sketch164  label="m4Mounts006"
  FullyConstrained = true
  Placement = pos=(0,0,-144) rot=(0,0,1;0rad)
  sketch-geometry (4):
    g0: Circle CenterX=34.38 CenterY=-252.68 CenterZ=0 NormalX=0 NormalY=0 NormalZ=1 AngleXU=0 Radius=6
    g1: Circle CenterX=55.63 CenterY=-318.08 CenterZ=0 NormalX=0 NormalY=0 NormalZ=1 AngleXU=0 Radius=6
    g2: Circle CenterX=-55.63 CenterY=-318.08 CenterZ=0 NormalX=0 NormalY=0 NormalZ=1 AngleXU=0 Radius=6
    g3: Circle CenterX=-34.38 CenterY=-252.68 CenterZ=0 NormalX=0 NormalY=0 NormalZ=1 AngleXU=0 Radius=6
  constraints (12):
    c: Equal(g1,g2)
    c: Equal(g1,g3)
    c: Equal(g1,g0)
    c: Diameter(g1) = 12
    c: DistanceY(g1) = -318.08
    c: DistanceY(g0) = -252.68
    c: DistanceY(g3) = -252.68
    c: DistanceX(g3) = -34.38
    c: DistanceX(g0) = 34.38
    c: DistanceX(g1) = 55.63
    c: DistanceX(g2) = -55.63
    c: DistanceY(g2) = -318.08
FEATURE [Part::Extrusion] Extrude062  label="m4Mounts005"
  Base = -> Sketch164
  Dir = (0,0,1)
  DirMode = 2
  FaceMakerClass = Part::FaceMakerBullseye
  LengthFwd = 18
  LengthRev = 0
  Solid = true
  Symmetric = false
FEATURE [Part::MultiFuse] Fusion129  label="base021"
  Shapes = -> [Extrude059,Fusion128]
FEATURE [Sketcher::SketchObject] Sketch165  label="m4Mounts008"
  FullyConstrained = true
  Placement = pos=(0,0,-145) rot=(0,0,1;0rad)
  sketch-geometry (4):
    g0: Circle CenterX=34.38 CenterY=-252.68 CenterZ=0 NormalX=0 NormalY=0 NormalZ=1 AngleXU=0 Radius=1.625
    g1: Circle CenterX=55.63 CenterY=-318.08 CenterZ=0 NormalX=0 NormalY=0 NormalZ=1 AngleXU=0 Radius=1.625
    g2: Circle CenterX=-55.63 CenterY=-318.08 CenterZ=0 NormalX=0 NormalY=0 NormalZ=1 AngleXU=0 Radius=1.625
    g3: Circle CenterX=-34.38 CenterY=-252.68 CenterZ=0 NormalX=0 NormalY=0 NormalZ=1 AngleXU=0 Radius=1.625
  constraints (12):
    c: Equal(g1,g2)
    c: Equal(g1,g3)
    c: Equal(g1,g0)
    c: Diameter(g1) = 3.25
    c: DistanceY(g1) = -318.08
    c: DistanceY(g0) = -252.68
    c: DistanceY(g3) = -252.68
    c: DistanceX(g3) = -34.38
    c: DistanceX(g0) = 34.38
    c: DistanceX(g1) = 55.63
    c: DistanceX(g2) = -55.63
    c: DistanceY(g2) = -318.08
FEATURE [Part::Extrusion] Extrude063  label="m3Cuts"
  Base = -> Sketch165
  Dir = (0,0,1)
  DirMode = 2
  FaceMakerClass = Part::FaceMakerBullseye
  LengthFwd = 18
  LengthRev = 0
  Solid = true
  Symmetric = false
FEATURE [Sketcher::SketchObject] Sketch166  label="m4Mounts009"
  FullyConstrained = true
  Placement = pos=(0,0,-145) rot=(0,0,1;0rad)
  sketch-geometry (4):
    g0: Circle CenterX=34.38 CenterY=-252.68 CenterZ=0 NormalX=0 NormalY=0 NormalZ=1 AngleXU=0 Radius=1.625
    g1: Circle CenterX=55.63 CenterY=-318.08 CenterZ=0 NormalX=0 NormalY=0 NormalZ=1 AngleXU=0 Radius=1.625
    g2: Circle CenterX=-55.63 CenterY=-318.08 CenterZ=0 NormalX=0 NormalY=0 NormalZ=1 AngleXU=0 Radius=1.625
    g3: Circle CenterX=-34.38 CenterY=-252.68 CenterZ=0 NormalX=0 NormalY=0 NormalZ=1 AngleXU=0 Radius=1.625
  constraints (12):
    c: Equal(g1,g2)
    c: Equal(g1,g3)
    c: Equal(g1,g0)
    c: Diameter(g1) = 3.25
    c: DistanceY(g1) = -318.08
    c: DistanceY(g0) = -252.68
    c: DistanceY(g3) = -252.68
    c: DistanceX(g3) = -34.38
    c: DistanceX(g0) = 34.38
    c: DistanceX(g1) = 55.63
    c: DistanceX(g2) = -55.63
    c: DistanceY(g2) = -318.08
FEATURE [Part::Extrusion] Extrude064  label="m3Cuts001"
  Base = -> Sketch166
  Dir = (0,0,1)
  DirMode = 2
  FaceMakerClass = Part::FaceMakerBullseye
  LengthFwd = 18
  LengthRev = 0
  Solid = true
  Symmetric = false
FEATURE [Part::Cut] Cut069  label="base022"
  Base = -> Fusion129
  Tool = -> Extrude064
FEATURE [Sketcher::SketchObject] Sketch167  label="SketchTop021"
  FullyConstrained = true
  sketch-geometry (6):
    g0: LineSegment StartX=50 StartY=-368.819 StartZ=0 EndX=80.9017 EndY=-273.713 EndZ=0
    g1: LineSegment StartX=80.9017 StartY=-273.713 StartZ=0 EndX=0 EndY=-214.935 EndZ=0
    g2: LineSegment StartX=0 StartY=-214.935 StartZ=0 EndX=-80.9017 EndY=-273.713 EndZ=0
    g3: LineSegment StartX=-80.9017 StartY=-273.713 StartZ=0 EndX=-50 EndY=-368.819 EndZ=0
    g4: LineSegment StartX=-50 StartY=-368.819 StartZ=0 EndX=50 EndY=-368.819 EndZ=0
    g5: Circle CenterX=0 CenterY=-300 CenterZ=0 NormalX=0 NormalY=0 NormalZ=1 AngleXU=0 Radius=85.0651
  constraints (15):
    c: Coincident(g0,g1)
    c: Coincident(g1,g2)
    c: Coincident(g2,g3)
    c: Coincident(g3,g4)
    c: Coincident(g4,g0)
    c: Equal(g0, g1-g4) x4
    c: PointOnObject(g0,g5)
    c: PointOnObject(g1,g5)
    c: PointOnObject(g2,g5)
    c: PointOnObject(g3,g5)
    c: PointOnObject(g4,g5)
    c: Horizontal(g4)
    c: DistanceX(g4,g4) = 100
    c: DistanceY(g5) = -300
    c: DistanceX(g5) = 0
FEATURE [Sketcher::SketchObject] Sketch168  label="SketchBottom022"
  FullyConstrained = true
  Placement = pos=(0,0,20) rot=(0,0,1;0rad)
  sketch-geometry (6):
    g0: LineSegment StartX=37.5 StartY=-351.614 StartZ=0 EndX=60.6763 EndY=-280.285 EndZ=0
    g1: LineSegment StartX=60.6763 StartY=-280.285 StartZ=0 EndX=0 EndY=-236.201 EndZ=0
    g2: LineSegment StartX=0 StartY=-236.201 StartZ=0 EndX=-60.6763 EndY=-280.285 EndZ=0
    g3: LineSegment StartX=-60.6763 StartY=-280.285 StartZ=0 EndX=-37.5 EndY=-351.614 EndZ=0
    g4: LineSegment StartX=-37.5 StartY=-351.614 StartZ=0 EndX=37.5 EndY=-351.614 EndZ=0
    g5: Circle CenterX=0 CenterY=-300 CenterZ=0 NormalX=0 NormalY=0 NormalZ=1 AngleXU=0 Radius=63.7988
  constraints (15):
    c: Coincident(g0,g1)
    c: Coincident(g1,g2)
    c: Coincident(g2,g3)
    c: Coincident(g3,g4)
    c: Coincident(g4,g0)
    c: Equal(g0, g1-g4) x4
    c: PointOnObject(g0,g5)
    c: PointOnObject(g1,g5)
    c: PointOnObject(g2,g5)
    c: PointOnObject(g3,g5)
    c: PointOnObject(g4,g5)
    c: Horizontal(g4)
    c: DistanceX(g4,g4) = 75
    c: DistanceX(g5) = 0
    c: DistanceY(g5) = -300
FEATURE [Part::Loft] Loft038
  Closed = false
  MaxDegree = 5
  Ruled = false
  Sections = -> [Sketch167,Sketch168]
  Solid = true
FEATURE [Sketcher::SketchObject] Sketch169  label="SketchTop022"
  FullyConstrained = true
  sketch-geometry (6):
    g0: LineSegment StartX=47.5 StartY=-365.378 StartZ=0 EndX=76.8566 EndY=-275.028 EndZ=0
    g1: LineSegment StartX=76.8566 StartY=-275.028 StartZ=0 EndX=1.9185e-12 EndY=-219.188 EndZ=0
    g2: LineSegment StartX=1.9185e-12 StartY=-219.188 StartZ=0 EndX=-76.8566 EndY=-275.028 EndZ=0
    g3: LineSegment StartX=-76.8566 StartY=-275.028 StartZ=0 EndX=-47.5 EndY=-365.378 EndZ=0
    g4: LineSegment StartX=-47.5 StartY=-365.378 StartZ=0 EndX=47.5 EndY=-365.378 EndZ=0
    g5: Circle CenterX=0 CenterY=-300 CenterZ=0 NormalX=0 NormalY=0 NormalZ=1 AngleXU=0 Radius=80.8118
  constraints (15):
    c: Coincident(g0,g1)
    c: Coincident(g1,g2)
    c: Coincident(g2,g3)
    c: Coincident(g3,g4)
    c: Coincident(g4,g0)
    c: Equal(g0, g1-g4) x4
    c: PointOnObject(g0,g5)
    c: PointOnObject(g1,g5)
    c: PointOnObject(g2,g5)
    c: PointOnObject(g3,g5)
    c: PointOnObject(g4,g5)
    c: Horizontal(g4)
    c: DistanceX(g4,g4) = 95
    c: DistanceY(g5) = -300
    c: DistanceX(g5) = 0
FEATURE [Sketcher::SketchObject] Sketch170  label="SketchBottom023"
  FullyConstrained = true
  Placement = pos=(0,0,20) rot=(0,0,1;0rad)
  sketch-geometry (6):
    g0: LineSegment StartX=35 StartY=-348.173 StartZ=0 EndX=56.6312 EndY=-281.599 EndZ=0
    g1: LineSegment StartX=56.6312 StartY=-281.599 StartZ=0 EndX=0 EndY=-240.454 EndZ=0
    g2: LineSegment StartX=0 StartY=-240.454 StartZ=0 EndX=-56.6312 EndY=-281.599 EndZ=0
    g3: LineSegment StartX=-56.6312 StartY=-281.599 StartZ=0 EndX=-35 EndY=-348.173 EndZ=0
    g4: LineSegment StartX=-35 StartY=-348.173 StartZ=0 EndX=35 EndY=-348.173 EndZ=0
    g5: Circle CenterX=0 CenterY=-300 CenterZ=0 NormalX=0 NormalY=0 NormalZ=1 AngleXU=0 Radius=59.5456
  constraints (15):
    c: Coincident(g0,g1)
    c: Coincident(g1,g2)
    c: Coincident(g2,g3)
    c: Coincident(g3,g4)
    c: Coincident(g4,g0)
    c: Equal(g0, g1-g4) x4
    c: PointOnObject(g0,g5)
    c: PointOnObject(g1,g5)
    c: PointOnObject(g2,g5)
    c: PointOnObject(g3,g5)
    c: PointOnObject(g4,g5)
    c: Horizontal(g4)
    c: DistanceX(g4,g4) = 70
    c: DistanceX(g5) = 0
    c: DistanceY(g5) = -300
FEATURE [Part::Loft] Loft039
  Closed = false
  MaxDegree = 5
  Ruled = false
  Sections = -> [Sketch169,Sketch170]
  Solid = true
FEATURE [Part::Cut] Cut070  label="srsCone016"
  Base = -> Loft038
  Placement = pos=(0,0,-36) rot=(0,0,1;0rad)
  Tool = -> Loft039
FEATURE [Part::Fillet] Fillet064
  Base = -> Cut070
  Edges = 5 edges r=1.5: [Edge3,Edge15,Edge16,Edge17,Edge18]
FEATURE [Part::Fillet] Fillet065
  Base = -> Fillet064
  Edges = 5 edges r=1.5: [Edge4,Edge7,Edge11,Edge12,Edge13]
FEATURE [Part::Fillet] Fillet066
  Base = -> Fillet065
  Edges = 5 edges r=2: [Edge1,Edge3,Edge5,Edge15,Edge17]
FEATURE [Part::Fillet] Fillet067  label="srsCone017"
  Base = -> Fillet066
  Edges = 5 edges r=1.5: [Edge63,Edge64,Edge65,Edge66,Edge67]
  Placement = pos=(0,0,-108.5) rot=(0,0,1;0rad)
FEATURE [Sketcher::SketchObject] Sketch171  label="SketchTop023"
  FullyConstrained = true
  sketch-geometry (6):
    g0: LineSegment StartX=50 StartY=-368.819 StartZ=0 EndX=80.9017 EndY=-273.713 EndZ=0
    g1: LineSegment StartX=80.9017 StartY=-273.713 StartZ=0 EndX=0 EndY=-214.935 EndZ=0
    g2: LineSegment StartX=0 StartY=-214.935 StartZ=0 EndX=-80.9017 EndY=-273.713 EndZ=0
    g3: LineSegment StartX=-80.9017 StartY=-273.713 StartZ=0 EndX=-50 EndY=-368.819 EndZ=0
    g4: LineSegment StartX=-50 StartY=-368.819 StartZ=0 EndX=50 EndY=-368.819 EndZ=0
    g5: Circle CenterX=0 CenterY=-300 CenterZ=0 NormalX=0 NormalY=0 NormalZ=1 AngleXU=0 Radius=85.0651
  constraints (15):
    c: Coincident(g0,g1)
    c: Coincident(g1,g2)
    c: Coincident(g2,g3)
    c: Coincident(g3,g4)
    c: Coincident(g4,g0)
    c: Equal(g0, g1-g4) x4
    c: PointOnObject(g0,g5)
    c: PointOnObject(g1,g5)
    c: PointOnObject(g2,g5)
    c: PointOnObject(g3,g5)
    c: PointOnObject(g4,g5)
    c: Horizontal(g4)
    c: DistanceX(g4,g4) = 100
    c: DistanceY(g5) = -300
    c: DistanceX(g5) = 0
FEATURE [Sketcher::SketchObject] Sketch172  label="SketchBottom024"
  FullyConstrained = true
  Placement = pos=(0,0,20) rot=(0,0,1;0rad)
  sketch-geometry (6):
    g0: LineSegment StartX=37.5 StartY=-351.614 StartZ=0 EndX=60.6763 EndY=-280.285 EndZ=0
    g1: LineSegment StartX=60.6763 StartY=-280.285 StartZ=0 EndX=0 EndY=-236.201 EndZ=0
    g2: LineSegment StartX=0 StartY=-236.201 StartZ=0 EndX=-60.6763 EndY=-280.285 EndZ=0
    g3: LineSegment StartX=-60.6763 StartY=-280.285 StartZ=0 EndX=-37.5 EndY=-351.614 EndZ=0
    g4: LineSegment StartX=-37.5 StartY=-351.614 StartZ=0 EndX=37.5 EndY=-351.614 EndZ=0
    g5: Circle CenterX=0 CenterY=-300 CenterZ=0 NormalX=0 NormalY=0 NormalZ=1 AngleXU=0 Radius=63.7988
  constraints (15):
    c: Coincident(g0,g1)
    c: Coincident(g1,g2)
    c: Coincident(g2,g3)
    c: Coincident(g3,g4)
    c: Coincident(g4,g0)
    c: Equal(g0, g1-g4) x4
    c: PointOnObject(g0,g5)
    c: PointOnObject(g1,g5)
    c: PointOnObject(g2,g5)
    c: PointOnObject(g3,g5)
    c: PointOnObject(g4,g5)
    c: Horizontal(g4)
    c: DistanceX(g4,g4) = 75
    c: DistanceX(g5) = 0
    c: DistanceY(g5) = -300
FEATURE [Part::Loft] Loft040
  Closed = false
  MaxDegree = 5
  Ruled = false
  Sections = -> [Sketch171,Sketch172]
  Solid = true
FEATURE [Sketcher::SketchObject] Sketch173  label="SketchTop024"
  FullyConstrained = true
  sketch-geometry (6):
    g0: LineSegment StartX=47.5 StartY=-365.378 StartZ=0 EndX=76.8566 EndY=-275.028 EndZ=0
    g1: LineSegment StartX=76.8566 StartY=-275.028 StartZ=0 EndX=1.9185e-12 EndY=-219.188 EndZ=0
    g2: LineSegment StartX=1.9185e-12 StartY=-219.188 StartZ=0 EndX=-76.8566 EndY=-275.028 EndZ=0
    g3: LineSegment StartX=-76.8566 StartY=-275.028 StartZ=0 EndX=-47.5 EndY=-365.378 EndZ=0
    g4: LineSegment StartX=-47.5 StartY=-365.378 StartZ=0 EndX=47.5 EndY=-365.378 EndZ=0
    g5: Circle CenterX=0 CenterY=-300 CenterZ=0 NormalX=0 NormalY=0 NormalZ=1 AngleXU=0 Radius=80.8118
  constraints (15):
    c: Coincident(g0,g1)
    c: Coincident(g1,g2)
    c: Coincident(g2,g3)
    c: Coincident(g3,g4)
    c: Coincident(g4,g0)
    c: Equal(g0, g1-g4) x4
    c: PointOnObject(g0,g5)
    c: PointOnObject(g1,g5)
    c: PointOnObject(g2,g5)
    c: PointOnObject(g3,g5)
    c: PointOnObject(g4,g5)
    c: Horizontal(g4)
    c: DistanceX(g4,g4) = 95
    c: DistanceY(g5) = -300
    c: DistanceX(g5) = 0
FEATURE [Sketcher::SketchObject] Sketch174  label="SketchBottom025"
  FullyConstrained = true
  Placement = pos=(0,0,20) rot=(0,0,1;0rad)
  sketch-geometry (6):
    g0: LineSegment StartX=35 StartY=-348.173 StartZ=0 EndX=56.6312 EndY=-281.599 EndZ=0
    g1: LineSegment StartX=56.6312 StartY=-281.599 StartZ=0 EndX=0 EndY=-240.454 EndZ=0
    g2: LineSegment StartX=0 StartY=-240.454 StartZ=0 EndX=-56.6312 EndY=-281.599 EndZ=0
    g3: LineSegment StartX=-56.6312 StartY=-281.599 StartZ=0 EndX=-35 EndY=-348.173 EndZ=0
    g4: LineSegment StartX=-35 StartY=-348.173 StartZ=0 EndX=35 EndY=-348.173 EndZ=0
    g5: Circle CenterX=0 CenterY=-300 CenterZ=0 NormalX=0 NormalY=0 NormalZ=1 AngleXU=0 Radius=59.5456
  constraints (15):
    c: Coincident(g0,g1)
    c: Coincident(g1,g2)
    c: Coincident(g2,g3)
    c: Coincident(g3,g4)
    c: Coincident(g4,g0)
    c: Equal(g0, g1-g4) x4
    c: PointOnObject(g0,g5)
    c: PointOnObject(g1,g5)
    c: PointOnObject(g2,g5)
    c: PointOnObject(g3,g5)
    c: PointOnObject(g4,g5)
    c: Horizontal(g4)
    c: DistanceX(g4,g4) = 70
    c: DistanceX(g5) = 0
    c: DistanceY(g5) = -300
FEATURE [Part::Loft] Loft041
  Closed = false
  MaxDegree = 5
  Ruled = false
  Sections = -> [Sketch173,Sketch174]
  Solid = true
FEATURE [Part::Cut] Cut071  label="srsCone018"
  Base = -> Loft040
  Placement = pos=(0,0,-36) rot=(0,0,1;0rad)
  Tool = -> Loft041
FEATURE [Part::Fillet] Fillet068
  Base = -> Cut071
  Edges = 5 edges r=1.5: [Edge3,Edge15,Edge16,Edge17,Edge18]
FEATURE [Part::Fillet] Fillet069
  Base = -> Fillet068
  Edges = 5 edges r=1.5: [Edge4,Edge7,Edge11,Edge12,Edge13]
FEATURE [Part::Fillet] Fillet070
  Base = -> Fillet069
  Edges = 5 edges r=2: [Edge1,Edge3,Edge5,Edge15,Edge17]
FEATURE [Part::Fillet] Fillet071  label="srsCone019"
  Base = -> Fillet070
  Edges = 5 edges r=1.5: [Edge63,Edge64,Edge65,Edge66,Edge67]
  Placement = pos=(0,0,-108) rot=(0,0,1;0rad)
FEATURE [Sketcher::SketchObject] Sketch175  label="SketchTop025"
  FullyConstrained = true
  sketch-geometry (6):
    g0: LineSegment StartX=50 StartY=-368.819 StartZ=0 EndX=80.9017 EndY=-273.713 EndZ=0
    g1: LineSegment StartX=80.9017 StartY=-273.713 StartZ=0 EndX=0 EndY=-214.935 EndZ=0
    g2: LineSegment StartX=0 StartY=-214.935 StartZ=0 EndX=-80.9017 EndY=-273.713 EndZ=0
    g3: LineSegment StartX=-80.9017 StartY=-273.713 StartZ=0 EndX=-50 EndY=-368.819 EndZ=0
    g4: LineSegment StartX=-50 StartY=-368.819 StartZ=0 EndX=50 EndY=-368.819 EndZ=0
    g5: Circle CenterX=0 CenterY=-300 CenterZ=0 NormalX=0 NormalY=0 NormalZ=1 AngleXU=0 Radius=85.0651
  constraints (15):
    c: Coincident(g0,g1)
    c: Coincident(g1,g2)
    c: Coincident(g2,g3)
    c: Coincident(g3,g4)
    c: Coincident(g4,g0)
    c: Equal(g0, g1-g4) x4
    c: PointOnObject(g0,g5)
    c: PointOnObject(g1,g5)
    c: PointOnObject(g2,g5)
    c: PointOnObject(g3,g5)
    c: PointOnObject(g4,g5)
    c: Horizontal(g4)
    c: DistanceX(g4,g4) = 100
    c: DistanceY(g5) = -300
    c: DistanceX(g5) = 0
FEATURE [Sketcher::SketchObject] Sketch176  label="SketchBottom026"
  FullyConstrained = true
  Placement = pos=(0,0,20) rot=(0,0,1;0rad)
  sketch-geometry (6):
    g0: LineSegment StartX=37.5 StartY=-351.614 StartZ=0 EndX=60.6763 EndY=-280.285 EndZ=0
    g1: LineSegment StartX=60.6763 StartY=-280.285 StartZ=0 EndX=0 EndY=-236.201 EndZ=0
    g2: LineSegment StartX=0 StartY=-236.201 StartZ=0 EndX=-60.6763 EndY=-280.285 EndZ=0
    g3: LineSegment StartX=-60.6763 StartY=-280.285 StartZ=0 EndX=-37.5 EndY=-351.614 EndZ=0
    g4: LineSegment StartX=-37.5 StartY=-351.614 StartZ=0 EndX=37.5 EndY=-351.614 EndZ=0
    g5: Circle CenterX=0 CenterY=-300 CenterZ=0 NormalX=0 NormalY=0 NormalZ=1 AngleXU=0 Radius=63.7988
  constraints (15):
    c: Coincident(g0,g1)
    c: Coincident(g1,g2)
    c: Coincident(g2,g3)
    c: Coincident(g3,g4)
    c: Coincident(g4,g0)
    c: Equal(g0, g1-g4) x4
    c: PointOnObject(g0,g5)
    c: PointOnObject(g1,g5)
    c: PointOnObject(g2,g5)
    c: PointOnObject(g3,g5)
    c: PointOnObject(g4,g5)
    c: Horizontal(g4)
    c: DistanceX(g4,g4) = 75
    c: DistanceX(g5) = 0
    c: DistanceY(g5) = -300
FEATURE [Part::Loft] Loft042
  Closed = false
  MaxDegree = 5
  Ruled = false
  Sections = -> [Sketch175,Sketch176]
  Solid = true
FEATURE [Sketcher::SketchObject] Sketch177  label="SketchTop026"
  FullyConstrained = true
  sketch-geometry (6):
    g0: LineSegment StartX=47.5 StartY=-365.378 StartZ=0 EndX=76.8566 EndY=-275.028 EndZ=0
    g1: LineSegment StartX=76.8566 StartY=-275.028 StartZ=0 EndX=1.9185e-12 EndY=-219.188 EndZ=0
    g2: LineSegment StartX=1.9185e-12 StartY=-219.188 StartZ=0 EndX=-76.8566 EndY=-275.028 EndZ=0
    g3: LineSegment StartX=-76.8566 StartY=-275.028 StartZ=0 EndX=-47.5 EndY=-365.378 EndZ=0
    g4: LineSegment StartX=-47.5 StartY=-365.378 StartZ=0 EndX=47.5 EndY=-365.378 EndZ=0
    g5: Circle CenterX=0 CenterY=-300 CenterZ=0 NormalX=0 NormalY=0 NormalZ=1 AngleXU=0 Radius=80.8118
  constraints (15):
    c: Coincident(g0,g1)
    c: Coincident(g1,g2)
    c: Coincident(g2,g3)
    c: Coincident(g3,g4)
    c: Coincident(g4,g0)
    c: Equal(g0, g1-g4) x4
    c: PointOnObject(g0,g5)
    c: PointOnObject(g1,g5)
    c: PointOnObject(g2,g5)
    c: PointOnObject(g3,g5)
    c: PointOnObject(g4,g5)
    c: Horizontal(g4)
    c: DistanceX(g4,g4) = 95
    c: DistanceY(g5) = -300
    c: DistanceX(g5) = 0
FEATURE [Sketcher::SketchObject] Sketch178  label="SketchBottom027"
  FullyConstrained = true
  Placement = pos=(0,0,20) rot=(0,0,1;0rad)
  sketch-geometry (6):
    g0: LineSegment StartX=35 StartY=-348.173 StartZ=0 EndX=56.6312 EndY=-281.599 EndZ=0
    g1: LineSegment StartX=56.6312 StartY=-281.599 StartZ=0 EndX=0 EndY=-240.454 EndZ=0
    g2: LineSegment StartX=0 StartY=-240.454 StartZ=0 EndX=-56.6312 EndY=-281.599 EndZ=0
    g3: LineSegment StartX=-56.6312 StartY=-281.599 StartZ=0 EndX=-35 EndY=-348.173 EndZ=0
    g4: LineSegment StartX=-35 StartY=-348.173 StartZ=0 EndX=35 EndY=-348.173 EndZ=0
    g5: Circle CenterX=0 CenterY=-300 CenterZ=0 NormalX=0 NormalY=0 NormalZ=1 AngleXU=0 Radius=59.5456
  constraints (15):
    c: Coincident(g0,g1)
    c: Coincident(g1,g2)
    c: Coincident(g2,g3)
    c: Coincident(g3,g4)
    c: Coincident(g4,g0)
    c: Equal(g0, g1-g4) x4
    c: PointOnObject(g0,g5)
    c: PointOnObject(g1,g5)
    c: PointOnObject(g2,g5)
    c: PointOnObject(g3,g5)
    c: PointOnObject(g4,g5)
    c: Horizontal(g4)
    c: DistanceX(g4,g4) = 70
    c: DistanceX(g5) = 0
    c: DistanceY(g5) = -300
FEATURE [Part::Loft] Loft043
  Closed = false
  MaxDegree = 5
  Ruled = false
  Sections = -> [Sketch177,Sketch178]
  Solid = true
FEATURE [Part::Cut] Cut072  label="srsCone020"
  Base = -> Loft042
  Placement = pos=(0,0,-36) rot=(0,0,1;0rad)
  Tool = -> Loft043
FEATURE [Part::Fillet] Fillet072
  Base = -> Cut072
  Edges = 5 edges r=1.5: [Edge3,Edge15,Edge16,Edge17,Edge18]
FEATURE [Part::Fillet] Fillet073
  Base = -> Fillet072
  Edges = 5 edges r=1.5: [Edge4,Edge7,Edge11,Edge12,Edge13]
FEATURE [Part::Fillet] Fillet074
  Base = -> Fillet073
  Edges = 5 edges r=2: [Edge1,Edge3,Edge5,Edge15,Edge17]
FEATURE [Part::Fillet] Fillet075  label="srsCone021"
  Base = -> Fillet074
  Edges = 5 edges r=1.5: [Edge63,Edge64,Edge65,Edge66,Edge67]
  Placement = pos=(0,0,-112.25) rot=(0,0,1;0rad)
FEATURE [Sketcher::SketchObject] Sketch179  label="SketchBottom028"
  FullyConstrained = true
  Placement = pos=(0,0,20) rot=(0,0,1;0rad)
  sketch-geometry (6):
    g0: LineSegment StartX=37.5 StartY=-351.614 StartZ=0 EndX=60.6763 EndY=-280.285 EndZ=0
    g1: LineSegment StartX=60.6763 StartY=-280.285 StartZ=0 EndX=0 EndY=-236.201 EndZ=0
    g2: LineSegment StartX=0 StartY=-236.201 StartZ=0 EndX=-60.6763 EndY=-280.285 EndZ=0
    g3: LineSegment StartX=-60.6763 StartY=-280.285 StartZ=0 EndX=-37.5 EndY=-351.614 EndZ=0
    g4: LineSegment StartX=-37.5 StartY=-351.614 StartZ=0 EndX=37.5 EndY=-351.614 EndZ=0
    g5: Circle CenterX=0 CenterY=-300 CenterZ=0 NormalX=0 NormalY=0 NormalZ=1 AngleXU=0 Radius=63.7988
  constraints (15):
    c: Coincident(g0,g1)
    c: Coincident(g1,g2)
    c: Coincident(g2,g3)
    c: Coincident(g3,g4)
    c: Coincident(g4,g0)
    c: Equal(g0, g1-g4) x4
    c: PointOnObject(g0,g5)
    c: PointOnObject(g1,g5)
    c: PointOnObject(g2,g5)
    c: PointOnObject(g3,g5)
    c: PointOnObject(g4,g5)
    c: Horizontal(g4)
    c: DistanceX(g4,g4) = 75
    c: DistanceX(g5) = 0
    c: DistanceY(g5) = -300
FEATURE [Part::Extrusion] Extrude065  label="top002"
  Base = -> Sketch179
  Dir = (0,0,1)
  DirMode = 2
  FaceMakerClass = Part::FaceMakerBullseye
  LengthFwd = 4
  LengthRev = 0
  Placement = pos=(0,0,-152.25) rot=(0,0,1;0rad)
  Solid = true
  Symmetric = false
FEATURE [Part::Fillet] Fillet076
  Base = -> Extrude065
  Edges = 5 edges r=1: [Edge4,Edge7,Edge10,Edge13,Edge15]
FEATURE [Part::MultiFuse] Fusion131  label="base023"
  Shapes = -> [Fillet075,Fillet076]
FEATURE [Sketcher::SketchObject] Sketch182  label="SketchTop028"
  FullyConstrained = true
  sketch-geometry (6):
    g0: LineSegment StartX=50 StartY=-368.819 StartZ=0 EndX=80.9017 EndY=-273.713 EndZ=0
    g1: LineSegment StartX=80.9017 StartY=-273.713 StartZ=0 EndX=0 EndY=-214.935 EndZ=0
    g2: LineSegment StartX=0 StartY=-214.935 StartZ=0 EndX=-80.9017 EndY=-273.713 EndZ=0
    g3: LineSegment StartX=-80.9017 StartY=-273.713 StartZ=0 EndX=-50 EndY=-368.819 EndZ=0
    g4: LineSegment StartX=-50 StartY=-368.819 StartZ=0 EndX=50 EndY=-368.819 EndZ=0
    g5: Circle CenterX=0 CenterY=-300 CenterZ=0 NormalX=0 NormalY=0 NormalZ=1 AngleXU=0 Radius=85.0651
  constraints (15):
    c: Coincident(g0,g1)
    c: Coincident(g1,g2)
    c: Coincident(g2,g3)
    c: Coincident(g3,g4)
    c: Coincident(g4,g0)
    c: Equal(g0, g1-g4) x4
    c: PointOnObject(g0,g5)
    c: PointOnObject(g1,g5)
    c: PointOnObject(g2,g5)
    c: PointOnObject(g3,g5)
    c: PointOnObject(g4,g5)
    c: Horizontal(g4)
    c: DistanceX(g4,g4) = 100
    c: DistanceY(g5) = -300
    c: DistanceX(g5) = 0
FEATURE [Sketcher::SketchObject] Sketch183  label="SketchBottom030"
  FullyConstrained = true
  Placement = pos=(0,0,20) rot=(0,0,1;0rad)
  sketch-geometry (6):
    g0: LineSegment StartX=37.5 StartY=-351.614 StartZ=0 EndX=60.6763 EndY=-280.285 EndZ=0
    g1: LineSegment StartX=60.6763 StartY=-280.285 StartZ=0 EndX=0 EndY=-236.201 EndZ=0
    g2: LineSegment StartX=0 StartY=-236.201 StartZ=0 EndX=-60.6763 EndY=-280.285 EndZ=0
    g3: LineSegment StartX=-60.6763 StartY=-280.285 StartZ=0 EndX=-37.5 EndY=-351.614 EndZ=0
    g4: LineSegment StartX=-37.5 StartY=-351.614 StartZ=0 EndX=37.5 EndY=-351.614 EndZ=0
    g5: Circle CenterX=0 CenterY=-300 CenterZ=0 NormalX=0 NormalY=0 NormalZ=1 AngleXU=0 Radius=63.7988
  constraints (15):
    c: Coincident(g0,g1)
    c: Coincident(g1,g2)
    c: Coincident(g2,g3)
    c: Coincident(g3,g4)
    c: Coincident(g4,g0)
    c: Equal(g0, g1-g4) x4
    c: PointOnObject(g0,g5)
    c: PointOnObject(g1,g5)
    c: PointOnObject(g2,g5)
    c: PointOnObject(g3,g5)
    c: PointOnObject(g4,g5)
    c: Horizontal(g4)
    c: DistanceX(g4,g4) = 75
    c: DistanceX(g5) = 0
    c: DistanceY(g5) = -300
FEATURE [Part::Loft] Loft045
  Closed = false
  MaxDegree = 5
  Ruled = false
  Sections = -> [Sketch182,Sketch183]
  Solid = true
FEATURE [Part::Cylinder] Cylinder195
  Angle = 360
  AttacherType = Attacher::AttachEngine3D
  FirstAngle = 0
  Height = 20
  Placement = pos=(0,-300,0) rot=(0,0,1;0rad)
  Radius = 90
  SecondAngle = 0
FEATURE [Part::Cut] Cut073
  Base = -> Cylinder195
  Placement = pos=(0,0,-148.25) rot=(0,0,1;0rad)
  Tool = -> Loft045
FEATURE [Part::Cut] Cut074  label="base024Final"
  Base = -> Cut069
  Tool = -> Cut073
FEATURE [Sketcher::SketchObject] Sketch184  label="SketchTop029"
  FullyConstrained = true
  sketch-geometry (6):
    g0: LineSegment StartX=47.5 StartY=-365.378 StartZ=0 EndX=76.8566 EndY=-275.028 EndZ=0
    g1: LineSegment StartX=76.8566 StartY=-275.028 StartZ=0 EndX=1.9185e-12 EndY=-219.188 EndZ=0
    g2: LineSegment StartX=1.9185e-12 StartY=-219.188 StartZ=0 EndX=-76.8566 EndY=-275.028 EndZ=0
    g3: LineSegment StartX=-76.8566 StartY=-275.028 StartZ=0 EndX=-47.5 EndY=-365.378 EndZ=0
    g4: LineSegment StartX=-47.5 StartY=-365.378 StartZ=0 EndX=47.5 EndY=-365.378 EndZ=0
    g5: Circle CenterX=0 CenterY=-300 CenterZ=0 NormalX=0 NormalY=0 NormalZ=1 AngleXU=0 Radius=80.8118
  constraints (15):
    c: Coincident(g0,g1)
    c: Coincident(g1,g2)
    c: Coincident(g2,g3)
    c: Coincident(g3,g4)
    c: Coincident(g4,g0)
    c: Equal(g0, g1-g4) x4
    c: PointOnObject(g0,g5)
    c: PointOnObject(g1,g5)
    c: PointOnObject(g2,g5)
    c: PointOnObject(g3,g5)
    c: PointOnObject(g4,g5)
    c: Horizontal(g4)
    c: DistanceX(g4,g4) = 95
    c: DistanceY(g5) = -300
    c: DistanceX(g5) = 0
FEATURE [Sketcher::SketchObject] Sketch185  label="SketchBottom031"
  FullyConstrained = true
  Placement = pos=(0,0,20) rot=(0,0,1;0rad)
  sketch-geometry (6):
    g0: LineSegment StartX=35 StartY=-348.173 StartZ=0 EndX=56.6312 EndY=-281.599 EndZ=0
    g1: LineSegment StartX=56.6312 StartY=-281.599 StartZ=0 EndX=0 EndY=-240.454 EndZ=0
    g2: LineSegment StartX=0 StartY=-240.454 StartZ=0 EndX=-56.6312 EndY=-281.599 EndZ=0
    g3: LineSegment StartX=-56.6312 StartY=-281.599 StartZ=0 EndX=-35 EndY=-348.173 EndZ=0
    g4: LineSegment StartX=-35 StartY=-348.173 StartZ=0 EndX=35 EndY=-348.173 EndZ=0
    g5: Circle CenterX=0 CenterY=-300 CenterZ=0 NormalX=0 NormalY=0 NormalZ=1 AngleXU=0 Radius=59.5456
  constraints (15):
    c: Coincident(g0,g1)
    c: Coincident(g1,g2)
    c: Coincident(g2,g3)
    c: Coincident(g3,g4)
    c: Coincident(g4,g0)
    c: Equal(g0, g1-g4) x4
    c: PointOnObject(g0,g5)
    c: PointOnObject(g1,g5)
    c: PointOnObject(g2,g5)
    c: PointOnObject(g3,g5)
    c: PointOnObject(g4,g5)
    c: Horizontal(g4)
    c: DistanceX(g4,g4) = 70
    c: DistanceX(g5) = 0
    c: DistanceY(g5) = -300
FEATURE [Part::Loft] Loft046
  Closed = false
  MaxDegree = 5
  Placement = pos=(0,0,-144) rot=(0,0,1;0rad)
  Ruled = false
  Sections = -> [Sketch184,Sketch185]
  Solid = true
FEATURE [Sketcher::SketchObject] Sketch186  label="m4Mounts011"
  FullyConstrained = true
  Placement = pos=(0,0,-144) rot=(0,0,1;0rad)
  sketch-geometry (4):
    g0: Circle CenterX=34.38 CenterY=-252.68 CenterZ=0 NormalX=0 NormalY=0 NormalZ=1 AngleXU=0 Radius=6
    g1: Circle CenterX=55.63 CenterY=-318.08 CenterZ=0 NormalX=0 NormalY=0 NormalZ=1 AngleXU=0 Radius=6
    g2: Circle CenterX=-55.63 CenterY=-318.08 CenterZ=0 NormalX=0 NormalY=0 NormalZ=1 AngleXU=0 Radius=6
    g3: Circle CenterX=-34.38 CenterY=-252.68 CenterZ=0 NormalX=0 NormalY=0 NormalZ=1 AngleXU=0 Radius=6
  constraints (12):
    c: Equal(g1,g2)
    c: Equal(g1,g3)
    c: Equal(g1,g0)
    c: Diameter(g1) = 12
    c: DistanceY(g1) = -318.08
    c: DistanceY(g0) = -252.68
    c: DistanceY(g3) = -252.68
    c: DistanceX(g3) = -34.38
    c: DistanceX(g0) = 34.38
    c: DistanceX(g1) = 55.63
    c: DistanceX(g2) = -55.63
    c: DistanceY(g2) = -318.08
FEATURE [Part::Extrusion] Extrude066  label="m4Mounts010"
  Base = -> Sketch186
  Dir = (0,0,1)
  DirMode = 2
  FaceMakerClass = Part::FaceMakerBullseye
  LengthFwd = 17
  LengthRev = 0
  Solid = true
  Symmetric = false
FEATURE [Part::Cut] Cut075  label="m4Mounts012"
  Base = -> Extrude066
  Tool = -> Loft046
FEATURE [Part::MultiFuse] Fusion132
  Shapes = -> [Extrude063,Extrude060]
FEATURE [Part::Cut] Cut076  label="m4nutHolds"
  Base = -> Cut075
  Tool = -> Fusion132
FEATURE [Part::MultiFuse] Fusion133  label="srs003"
  Shapes = -> [Fusion124,Cut076]
FEATURE [Mesh::Feature] mintsLogo80P___90CutBase  label="mintsLogo80P - 90CutBase"
  Placement = pos=(0.2,-346,-108.5) rot=(1,0,0;1.5708rad)
FEATURE [Sketcher::SketchObject] Sketch187
  FullyConstrained = true
  Placement = pos=(0,0,-124.5) rot=(0,0,1;0rad)
  sketch-geometry (4):
    g0: LineSegment StartX=-14 StartY=-350 StartZ=0 EndX=14 EndY=-350 EndZ=0
    g1: LineSegment StartX=-14 StartY=-350 StartZ=0 EndX=-20 EndY=-352 EndZ=0
    g2: LineSegment StartX=-20 StartY=-352 StartZ=0 EndX=20 EndY=-352 EndZ=0
    g3: LineSegment StartX=20 StartY=-352 StartZ=0 EndX=14 EndY=-350 EndZ=0
  constraints (12):
    c: Horizontal(g0)
    c: DistanceY(g0) = -350
    c: DistanceX(g0) = 14
    c: DistanceX(g0) = -14
    c: Coincident(g1,g0)
    c: Coincident(g2,g1)
    c: Horizontal(g2)
    c: Coincident(g3,g2)
    c: Coincident(g0,g3)
    c: DistanceY(g1,g0) = 2
    c: DistanceX(g1) = -20
    c: DistanceX(g2) = 20
FEATURE [Part::Extrusion] Extrude067  label="logoConcaveCut"
  Base = -> Sketch187
  Dir = (0,0,1)
  DirMode = 2
  FaceMakerClass = Part::FaceMakerBullseye
  LengthFwd = 32
  LengthRev = 0
  Solid = true
  Symmetric = false
FEATURE [Sketcher::SketchObject] Sketch188
  FullyConstrained = true
  Placement = pos=(-20,0,0) rot=(0.57735,0.57735,0.57735;2.0944rad)
  sketch-geometry (4):
    g0: LineSegment StartX=-352 StartY=-92.5 StartZ=0 EndX=-350 EndY=-98.5 EndZ=0
    g1: LineSegment StartX=-350 StartY=-98.5 StartZ=0 EndX=-350 EndY=-118.5 EndZ=0
    g2: LineSegment StartX=-350 StartY=-118.5 StartZ=0 EndX=-352 EndY=-124.5 EndZ=0
    g3: LineSegment StartX=-352 StartY=-124.5 StartZ=0 EndX=-352 EndY=-92.5 EndZ=0
  constraints (12):
    c: Coincident(g0,g1)
    c: Vertical(g1)
    c: Coincident(g1,g2)
    c: Coincident(g2,g3)
    c: Coincident(g3,g0)
    c: Vertical(g3)
    c: DistanceX(g0) = -352
    c: DistanceY(g0) = -92.5
    c: DistanceX(g0,g0) = 2
    c: DistanceY(g0,g0) = 6
    c: DistanceY(g2,g1) = 6
    c: DistanceY(g2) = -124.5
FEATURE [Part::Extrusion] Extrude068
  Base = -> Sketch188
  Dir = (1,-2e-16,2e-16)
  DirMode = 2
  FaceMakerClass = Part::FaceMakerBullseye
  LengthFwd = 40
  LengthRev = 0
  Solid = true
  Symmetric = false
FEATURE [Part::MultiCommon] Common001
  Shapes = -> [Extrude068,Extrude067]
FEATURE [Part::Fillet] Fillet077  label="logoOverallCut"
  Base = -> Common001
  Edges = 8 edges r=3: [Edge1,Edge2,Edge3,Edge5,Edge7,Edge8,Edge9,Edge10]
FEATURE [Part::Cut] Cut077  label="srs004"
  Base = -> Fusion133
  Tool = -> Fillet077
FEATURE [Sketcher::SketchObject] Sketch189
  FullyConstrained = true
  Placement = pos=(0,0,0) rot=(1,0,0;1.5708rad)
FEATURE [Sketcher::SketchObject] Sketch190
  FullyConstrained = true
  Placement = pos=(0,-295,0) rot=(1,0,0;1.5708rad)
  sketch-geometry (14):
    g0: LineSegment StartX=28 StartY=-309 StartZ=0 EndX=28 EndY=-301 EndZ=0
    g1: LineSegment StartX=-19 StartY=-309 StartZ=0 EndX=28 EndY=-309 EndZ=0
    g2: LineSegment StartX=-19 StartY=-309 StartZ=0 EndX=-19 EndY=-284 EndZ=0
    g3: LineSegment StartX=-19 StartY=-284 StartZ=0 EndX=-13 EndY=-284 EndZ=0
    g4: LineSegment StartX=-13 StartY=-284 StartZ=0 EndX=-13 EndY=-301 EndZ=0
    g5: Circle CenterX=-15.96 CenterY=-286.8 CenterZ=0 NormalX=0 NormalY=0 NormalZ=1 AngleXU=0 Radius=1.125
    g6: Circle CenterX=-0.15 CenterY=-304.37 CenterZ=0 NormalX=0 NormalY=0 NormalZ=1 AngleXU=0 Radius=1.125
    g7: Circle CenterX=20.15 CenterY=-304.37 CenterZ=0 NormalX=0 NormalY=0 NormalZ=1 AngleXU=0 Radius=1.125
    g8: LineSegment StartX=-13 StartY=-301 StartZ=0 EndX=11 EndY=-301 EndZ=0
    g9: LineSegment StartX=11 StartY=-301 StartZ=0 EndX=11 EndY=-263 EndZ=0
    g10: LineSegment StartX=11 StartY=-263 StartZ=0 EndX=19 EndY=-263 EndZ=0
    g11: LineSegment StartX=19 StartY=-263 StartZ=0 EndX=19 EndY=-301 EndZ=0
    g12: LineSegment StartX=19 StartY=-301 StartZ=0 EndX=28 EndY=-301 EndZ=0
    g13: Circle CenterX=16.04 CenterY=-270.55 CenterZ=0 NormalX=0 NormalY=0 NormalZ=1 AngleXU=0 Radius=1.125
  constraints (42):
    c: Vertical(g0)
    c: Coincident(g1,g0)
    c: Horizontal(g1)
    c: DistanceX(g0) = 28
    c: Vertical(g2)
    c: Coincident(g3,g2)
    c: Horizontal(g3)
    c: Coincident(g4,g3)
    c: Vertical(g4)
    c: DistanceY(g1,g6) = 4.63
    c: DistanceY(g6,g7) = 0
    c: DistanceX(g6,g7) = 20.3
    c: DistanceY(g1) = -309
    c: Coincident(g2,g1)
    c: Coincident(g8,g4)
    c: Horizontal(g8)
    c: DistanceX(g4) = -13
    c: Vertical(g9)
    c: Distance(g3) = 6
    c: Coincident(g10,g9)
    c: Horizontal(g10)
    c: Coincident(g11,g10)
    c: Vertical(g11)
    c: Coincident(g12,g0)
    c: Horizontal(g12)
    c: DistanceY(g8,g11) = 0
    c: Coincident(g11,g12)
    c: DistanceX(g10) = 19
    c: DistanceX(g10,g10) = 8
    c: Coincident(g8,g9)
    c: DistanceY(g9) = -263
    c: DistanceY(g1,g4) = 8
    c: DistanceY(g1,g2) = 25
    c: DistanceX(g5,g13) = 32
    c: DistanceY(g5,g13) = 16.25
    c: DistanceY(g1,g5) = 22.2
    c: DistanceX(g1,g5) = 3.04
    c: Equal(g6,g7)
    c: Equal(g6,g5)
    c: Equal(g6,g13)
    c: Diameter(g6) = 2.25
    c: DistanceX(g6) = -0.15
FEATURE [Part::Extrusion] Extrude069  label="i2cHold002"
  Base = -> Sketch190
  Dir = (0,-1,2e-16)
  DirMode = 2
  FaceMakerClass = Part::FaceMakerBullseye
  LengthFwd = 5
  LengthRev = 0
  Solid = true
  Symmetric = false
FEATURE [Sketcher::SketchObject] Sketch192  label="bmeNuts"
  FullyConstrained = true
  Placement = pos=(0,-334,0) rot=(1,0,0;1.5708rad)
  sketch-geometry (14):
    g0: LineSegment StartX=1.175 StartY=-120.045 StartZ=0 EndX=2.5 EndY=-117.75 EndZ=0
    g1: LineSegment StartX=2.5 StartY=-117.75 StartZ=0 EndX=1.175 EndY=-115.455 EndZ=0
    g2: LineSegment StartX=1.175 StartY=-115.455 StartZ=0 EndX=-1.475 EndY=-115.455 EndZ=0
    g3: LineSegment StartX=-1.475 StartY=-115.455 StartZ=0 EndX=-2.8 EndY=-117.75 EndZ=0
    g4: LineSegment StartX=-2.8 StartY=-117.75 StartZ=0 EndX=-1.475 EndY=-120.045 EndZ=0
    g5: LineSegment StartX=-1.475 StartY=-120.045 StartZ=0 EndX=1.175 EndY=-120.045 EndZ=0
    g6: Circle CenterX=-0.15 CenterY=-117.75 CenterZ=0 NormalX=0 NormalY=0 NormalZ=1 AngleXU=0 Radius=2.65
    g7: LineSegment StartX=21.475 StartY=-120.045 StartZ=0 EndX=22.8 EndY=-117.75 EndZ=0
    g8: LineSegment StartX=22.8 StartY=-117.75 StartZ=0 EndX=21.475 EndY=-115.455 EndZ=0
    g9: LineSegment StartX=21.475 StartY=-115.455 StartZ=0 EndX=18.825 EndY=-115.455 EndZ=0
    g10: LineSegment StartX=18.825 StartY=-115.455 StartZ=0 EndX=17.5 EndY=-117.75 EndZ=0
    g11: LineSegment StartX=17.5 StartY=-117.75 StartZ=0 EndX=18.825 EndY=-120.045 EndZ=0
    g12: LineSegment StartX=18.825 StartY=-120.045 StartZ=0 EndX=21.475 EndY=-120.045 EndZ=0
    g13: Circle CenterX=20.15 CenterY=-117.75 CenterZ=0 NormalX=0 NormalY=0 NormalZ=1 AngleXU=0 Radius=2.65
  constraints (34):
    c: Coincident(g0,g1)
    c: Coincident(g1,g2)
    c: Coincident(g2,g3)
    c: Coincident(g3,g4)
    c: Coincident(g4,g5)
    c: Coincident(g5,g0)
    c: Equal(g0, g1-g5) x5
    c: PointOnObject(g0,g6)
    c: PointOnObject(g1,g6)
    c: PointOnObject(g2,g6)
    c: PointOnObject(g3,g6)
    c: PointOnObject(g4,g6)
    c: PointOnObject(g5,g6)
    c: Coincident(g7,g8)
    c: Coincident(g8,g9)
    c: Coincident(g9,g10)
    c: Coincident(g10,g11)
    c: Coincident(g11,g12)
    c: Coincident(g12,g7)
    c: Equal(g7, g8-g12) x5
    c: PointOnObject(g7,g13)
    c: PointOnObject(g8,g13)
    c: PointOnObject(g9,g13)
    c: PointOnObject(g10,g13)
    c: PointOnObject(g11,g13)
    c: PointOnObject(g12,g13)
    c: DistanceX(g6) = -0.15
    c: DistanceY(g6) = -117.75
    c: DistanceX(g13) = 20.15
    c: DistanceY(g13) = -117.75
    c: DistanceX(g5,g5) = 2.65
    c: Horizontal(g5)
    c: Horizontal(g12)
    c: DistanceX(g12,g12) = 2.65
FEATURE [Sketcher::SketchObject] Sketch193  label="scdHold002"
  FullyConstrained = true
  Placement = pos=(0,-304,0) rot=(1,0,0;1.5708rad)
  sketch-geometry (14):
    g0: LineSegment StartX=-14.905 StartY=-119.095 StartZ=0 EndX=-13.58 EndY=-116.8 EndZ=0
    g1: LineSegment StartX=-13.58 StartY=-116.8 StartZ=0 EndX=-14.905 EndY=-114.505 EndZ=0
    g2: LineSegment StartX=-14.905 StartY=-114.505 StartZ=0 EndX=-17.555 EndY=-114.505 EndZ=0
    g3: LineSegment StartX=-17.555 StartY=-114.505 StartZ=0 EndX=-18.88 EndY=-116.8 EndZ=0
    g4: LineSegment StartX=-18.88 StartY=-116.8 StartZ=0 EndX=-17.555 EndY=-119.095 EndZ=0
    g5: LineSegment StartX=-17.555 StartY=-119.095 StartZ=0 EndX=-14.905 EndY=-119.095 EndZ=0
    g6: Circle CenterX=-16.23 CenterY=-116.8 CenterZ=0 NormalX=0 NormalY=0 NormalZ=1 AngleXU=0 Radius=2.65
    g7: LineSegment StartX=17.095 StartY=-102.845 StartZ=0 EndX=18.42 EndY=-100.55 EndZ=0
    g8: LineSegment StartX=18.42 StartY=-100.55 StartZ=0 EndX=17.095 EndY=-98.2551 EndZ=0
    g9: LineSegment StartX=17.095 StartY=-98.2551 StartZ=0 EndX=14.445 EndY=-98.2551 EndZ=0
    g10: LineSegment StartX=14.445 StartY=-98.2551 StartZ=0 EndX=13.12 EndY=-100.55 EndZ=0
    g11: LineSegment StartX=13.12 StartY=-100.55 StartZ=0 EndX=14.445 EndY=-102.845 EndZ=0
    g12: LineSegment StartX=14.445 StartY=-102.845 StartZ=0 EndX=17.095 EndY=-102.845 EndZ=0
    g13: Circle CenterX=15.77 CenterY=-100.55 CenterZ=0 NormalX=0 NormalY=0 NormalZ=1 AngleXU=0 Radius=2.65
  constraints (34):
    c: Coincident(g0,g1)
    c: Coincident(g1,g2)
    c: Coincident(g2,g3)
    c: Coincident(g3,g4)
    c: Coincident(g4,g5)
    c: Coincident(g5,g0)
    c: Equal(g0, g1-g5) x5
    c: PointOnObject(g0,g6)
    c: PointOnObject(g1,g6)
    c: PointOnObject(g2,g6)
    c: PointOnObject(g3,g6)
    c: PointOnObject(g4,g6)
    c: PointOnObject(g5,g6)
    c: Coincident(g7,g8)
    c: Coincident(g8,g9)
    c: Coincident(g9,g10)
    c: Coincident(g10,g11)
    c: Coincident(g11,g12)
    c: Coincident(g12,g7)
    c: Equal(g7, g8-g12) x5
    c: PointOnObject(g7,g13)
    c: PointOnObject(g8,g13)
    c: PointOnObject(g9,g13)
    c: PointOnObject(g10,g13)
    c: PointOnObject(g11,g13)
    c: PointOnObject(g12,g13)
    c: DistanceX(g6) = -16.23
    c: DistanceY(g6) = -116.8
    c: DistanceX(g13) = 15.77
    c: DistanceY(g13) = -100.55
    c: Horizontal(g12)
    c: Horizontal(g5)
    c: DistanceX(g5,g5) = 2.65
    c: DistanceX(g12,g12) = 2.65
FEATURE [Part::Extrusion] Extrude071  label="scdNuts"
  Base = -> Sketch193
  Dir = (0,-1,2e-16)
  DirMode = 2
  FaceMakerClass = Part::FaceMakerBullseye
  LengthFwd = 2
  LengthRev = 0
  Solid = true
  Symmetric = false
FEATURE [Part::Extrusion] Extrude072  label="bmeNuts001"
  Base = -> Sketch192
  Dir = (0,-1,2e-16)
  DirMode = 2
  FaceMakerClass = Part::FaceMakerBullseye
  LengthFwd = 2
  LengthRev = 0
  Solid = true
  Symmetric = false
FEATURE [Sketcher::SketchObject] Sketch194
  FullyConstrained = true
  Placement = pos=(0,-295,0) rot=(1,0,0;1.5708rad)
  sketch-geometry (14):
    g0: LineSegment StartX=28 StartY=-309 StartZ=0 EndX=28 EndY=-301 EndZ=0
    g1: LineSegment StartX=-19 StartY=-309 StartZ=0 EndX=28 EndY=-309 EndZ=0
    g2: LineSegment StartX=-19 StartY=-309 StartZ=0 EndX=-19 EndY=-284 EndZ=0
    g3: LineSegment StartX=-19 StartY=-284 StartZ=0 EndX=-13 EndY=-284 EndZ=0
    g4: LineSegment StartX=-13 StartY=-284 StartZ=0 EndX=-13 EndY=-301 EndZ=0
    g5: Circle CenterX=-15.96 CenterY=-286.8 CenterZ=0 NormalX=0 NormalY=0 NormalZ=1 AngleXU=0 Radius=1.125
    g6: Circle CenterX=-0.15 CenterY=-304.37 CenterZ=0 NormalX=0 NormalY=0 NormalZ=1 AngleXU=0 Radius=1.125
    g7: Circle CenterX=20.15 CenterY=-304.37 CenterZ=0 NormalX=0 NormalY=0 NormalZ=1 AngleXU=0 Radius=1.125
    g8: LineSegment StartX=-13 StartY=-301 StartZ=0 EndX=11 EndY=-301 EndZ=0
    g9: LineSegment StartX=11 StartY=-301 StartZ=0 EndX=11 EndY=-263 EndZ=0
    g10: LineSegment StartX=11 StartY=-263 StartZ=0 EndX=19 EndY=-263 EndZ=0
    g11: LineSegment StartX=19 StartY=-263 StartZ=0 EndX=19 EndY=-301 EndZ=0
    g12: LineSegment StartX=19 StartY=-301 StartZ=0 EndX=28 EndY=-301 EndZ=0
    g13: Circle CenterX=16.04 CenterY=-270.55 CenterZ=0 NormalX=0 NormalY=0 NormalZ=1 AngleXU=0 Radius=1.125
  constraints (42):
    c: Vertical(g0)
    c: Coincident(g1,g0)
    c: Horizontal(g1)
    c: DistanceX(g0) = 28
    c: Vertical(g2)
    c: Coincident(g3,g2)
    c: Horizontal(g3)
    c: Coincident(g4,g3)
    c: Vertical(g4)
    c: DistanceY(g1,g6) = 4.63
    c: DistanceY(g6,g7) = 0
    c: DistanceX(g6,g7) = 20.3
    c: DistanceY(g1) = -309
    c: Coincident(g2,g1)
    c: Coincident(g8,g4)
    c: Horizontal(g8)
    c: DistanceX(g4) = -13
    c: Vertical(g9)
    c: Distance(g3) = 6
    c: Coincident(g10,g9)
    c: Horizontal(g10)
    c: Coincident(g11,g10)
    c: Vertical(g11)
    c: Coincident(g12,g0)
    c: Horizontal(g12)
    c: DistanceY(g8,g11) = 0
    c: Coincident(g11,g12)
    c: DistanceX(g10) = 19
    c: DistanceX(g10,g10) = 8
    c: Coincident(g8,g9)
    c: DistanceY(g9) = -263
    c: DistanceY(g1,g4) = 8
    c: DistanceY(g1,g2) = 25
    c: DistanceX(g5,g13) = 32
    c: DistanceY(g5,g13) = 16.25
    c: DistanceY(g1,g5) = 22.2
    c: DistanceX(g1,g5) = 3.04
    c: Equal(g6,g7)
    c: Equal(g6,g5)
    c: Equal(g6,g13)
    c: Diameter(g6) = 2.25
    c: DistanceX(g6) = -0.15
FEATURE [Part::Extrusion] Extrude073  label="i2cHold003"
  Base = -> Sketch194
  Dir = (0,-1,2e-16)
  DirMode = 2
  FaceMakerClass = Part::FaceMakerBullseye
  LengthFwd = 5
  LengthRev = 0
  Solid = true
  Symmetric = false
FEATURE [Sketcher::SketchObject] Sketch196  label="ipsHold001"
  FullyConstrained = true
  Placement = pos=(0,-266,0) rot=(1,0,0;1.5708rad)
  sketch-geometry (14):
    g0: LineSegment StartX=-19.075 StartY=-119.695 StartZ=0 EndX=-17.75 EndY=-117.4 EndZ=0
    g1: LineSegment StartX=-17.75 StartY=-117.4 StartZ=0 EndX=-19.075 EndY=-115.105 EndZ=0
    g2: LineSegment StartX=-19.075 StartY=-115.105 StartZ=0 EndX=-21.725 EndY=-115.105 EndZ=0
    g3: LineSegment StartX=-21.725 StartY=-115.105 StartZ=0 EndX=-23.05 EndY=-117.4 EndZ=0
    g4: LineSegment StartX=-23.05 StartY=-117.4 StartZ=0 EndX=-21.725 EndY=-119.695 EndZ=0
    g5: LineSegment StartX=-21.725 StartY=-119.695 StartZ=0 EndX=-19.075 EndY=-119.695 EndZ=0
    g6: Circle CenterX=-20.4 CenterY=-117.4 CenterZ=0 NormalX=0 NormalY=0 NormalZ=1 AngleXU=0 Radius=2.65
    g7: LineSegment StartX=21.725 StartY=-82.895 StartZ=0 EndX=23.05 EndY=-80.6 EndZ=0
    g8: LineSegment StartX=23.05 StartY=-80.6 StartZ=0 EndX=21.725 EndY=-78.305 EndZ=0
    g9: LineSegment StartX=21.725 StartY=-78.305 StartZ=0 EndX=19.075 EndY=-78.305 EndZ=0
    g10: LineSegment StartX=19.075 StartY=-78.305 StartZ=0 EndX=17.75 EndY=-80.6 EndZ=0
    g11: LineSegment StartX=17.75 StartY=-80.6 StartZ=0 EndX=19.075 EndY=-82.895 EndZ=0
    g12: LineSegment StartX=19.075 StartY=-82.895 StartZ=0 EndX=21.725 EndY=-82.895 EndZ=0
    g13: Circle CenterX=20.4 CenterY=-80.6 CenterZ=0 NormalX=0 NormalY=0 NormalZ=1 AngleXU=0 Radius=2.65
  constraints (34):
    c: Coincident(g0,g1)
    c: Coincident(g1,g2)
    c: Coincident(g2,g3)
    c: Coincident(g3,g4)
    c: Coincident(g4,g5)
    c: Coincident(g5,g0)
    c: Equal(g0, g1-g5) x5
    c: PointOnObject(g0,g6)
    c: PointOnObject(g1,g6)
    c: PointOnObject(g2,g6)
    c: PointOnObject(g3,g6)
    c: PointOnObject(g4,g6)
    c: PointOnObject(g5,g6)
    c: Coincident(g7,g8)
    c: Coincident(g8,g9)
    c: Coincident(g9,g10)
    c: Coincident(g10,g11)
    c: Coincident(g11,g12)
    c: Coincident(g12,g7)
    c: Equal(g7, g8-g12) x5
    c: PointOnObject(g7,g13)
    c: PointOnObject(g8,g13)
    c: PointOnObject(g9,g13)
    c: PointOnObject(g10,g13)
    c: PointOnObject(g11,g13)
    c: PointOnObject(g12,g13)
    c: DistanceY(g6) = -117.4
    c: DistanceX(g6) = -20.4
    c: Horizontal(g5)
    c: DistanceX(g5,g5) = 2.65
    c: Horizontal(g12)
    c: DistanceX(g13) = 20.4
    c: DistanceY(g6,g13) = 36.8
    c: DistanceX(g12,g12) = 2.65
FEATURE [Part::Extrusion] Extrude074  label="ipsNuts"
  Base = -> Sketch196
  Dir = (0,-1,2e-16)
  DirMode = 2
  FaceMakerClass = Part::FaceMakerBullseye
  LengthFwd = 2
  LengthRev = 0
  Solid = true
  Symmetric = false
FEATURE [Part::MultiFuse] Fusion134
  Shapes = -> [Extrude074,Extrude072,Extrude071]
FEATURE [Part::Fillet] Fillet078
  Base = -> Cut074
  Edges = 48 edges r=1: [Edge229,Edge230,Edge231,Edge232,Edge233,Edge235,Edge236,Edge237,Edge239,Edge240,Edge241,Edge242,Edge243,Edge245,Edge246,Edge247,Edge249,Edge250,Edge251,Edge252,Edge253,Edge255,Edge256,Edge257,Edge259,Edge260,Edge261,Edge262,Edge263,Edge265,Edge266,Edge267,Edge269,Edge270,Edge271,Edge272,Edge273,+11 more]
FEATURE [Part::Fillet] Fillet079  label="base024"
  Base = -> Fillet078
  Edges = 24 edges r=3: [Edge1,Edge3,Edge5,Edge7,Edge23,Edge25,Edge27,Edge29,Edge31,Edge33,Edge35,Edge37,Edge39,Edge41,Edge43,Edge45,Edge47,Edge49,Edge51,Edge53,Edge55,Edge57,Edge59,Edge61]
FEATURE [Part::Cut] Cut078  label="base025"
  Base = -> Fillet079
  Tool = -> Fusion134
FEATURE [Part::Feature] Part__Feature244  label="m2Nut"
  Placement = pos=(20.4,-265,-80.6) rot=(-0.57735,-0.57735,-0.57735;2.0944rad)
  shape: bbox 4.62 x 1.885 x 4.62 mm, 37 faces (baked)
FEATURE [Part::Feature] Part__Feature245  label="m2Nut001"
  Placement = pos=(-20.4,-265,-117.4) rot=(0.57735,0.57735,0.57735;4.18879rad)
  shape: bbox 4.62 x 1.885 x 4.62 mm, 37 faces (baked)
FEATURE [Part::Feature] Part__Feature246  label="m2Nut002"
  Placement = pos=(-0.15,-333,-117.75) rot=(0.57735,0.57735,0.57735;4.18879rad)
  shape: bbox 4.62 x 1.885 x 4.62 mm, 37 faces (baked)
FEATURE [Part::Feature] Part__Feature247  label="m2Nut003"
  Placement = pos=(20.15,-333,-117.75) rot=(0.57735,0.57735,0.57735;4.18879rad)
  shape: bbox 4.62 x 1.885 x 4.62 mm, 37 faces (baked)
FEATURE [Part::Feature] Part__Feature248  label="m2Nut004"
  Placement = pos=(-16.25,-303,-116.8) rot=(0.57735,0.57735,0.57735;4.18879rad)
  shape: bbox 4.62 x 1.885 x 4.62 mm, 37 faces (baked)
FEATURE [Part::Feature] Part__Feature249  label="m2Nut005"
  Placement = pos=(15.75,-303,-100.55) rot=(0.57735,0.57735,0.57735;4.18879rad)
  shape: bbox 4.62 x 1.885 x 4.62 mm, 37 faces (baked)
FEATURE [Part::Feature] Part__Feature250  label="Body"
  shape: bbox 15.5 x 16.75 x 29 mm, 21 faces (baked)
FEATURE [Part::Feature] Part__Feature251  label="Body001"
  Placement = pos=(0,0,2) rot=(0,0,1;0rad)
  shape: bbox 17.44 x 17.44 x 14.25 mm, 14 faces (baked)
FEATURE [Part::Feature] Part__Feature252  label="Body002"
  Placement = pos=(0,0,-2.9) rot=(0,0,1;0rad)
  shape: bbox 19 x 19 x 4.75 mm, 25 faces (baked)
FEATURE [Part::Feature] Part__Feature253  label="Body003"
  shape: bbox 16.75 x 16.75 x 0.9 mm, 4 faces (baked)
FEATURE [App::Part] PG7_Gland1
  Group = -> [Part__Feature250,Part__Feature251,Part__Feature252,Part__Feature253]
  Origin = -> Origin061
  Placement = pos=(0,-300,-132.25) rot=(0.707107,0.707107,0;3.14159rad)
FEATURE [Sketcher::SketchObject] Sketch197  label="pg7Cuts"
  FullyConstrained = true
  Placement = pos=(0,0,-128.25) rot=(0,0,1;0rad)
  sketch-geometry (1):
    g0: Circle CenterX=0 CenterY=-300 CenterZ=0 NormalX=0 NormalY=0 NormalZ=1 AngleXU=0 Radius=6.25
  constraints (3):
    c: Diameter(g0) = 12.5
    c: DistanceX(g0) = 0
    c: DistanceY(g0) = -300
FEATURE [Sketcher::SketchObject] Sketch198  label="pg7Cuts001"
  FullyConstrained = true
  Placement = pos=(0,0,-128.25) rot=(0,0,1;0rad)
  sketch-geometry (7):
    g0: LineSegment StartX=5.375 StartY=-309.31 StartZ=0 EndX=10.75 EndY=-300 EndZ=0
    g1: LineSegment StartX=10.75 StartY=-300 StartZ=0 EndX=5.375 EndY=-290.69 EndZ=0
    g2: LineSegment StartX=5.375 StartY=-290.69 StartZ=0 EndX=-5.375 EndY=-290.69 EndZ=0
    g3: LineSegment StartX=-5.375 StartY=-290.69 StartZ=0 EndX=-10.75 EndY=-300 EndZ=0
    g4: LineSegment StartX=-10.75 StartY=-300 StartZ=0 EndX=-5.375 EndY=-309.31 EndZ=0
    g5: LineSegment StartX=-5.375 StartY=-309.31 StartZ=0 EndX=5.375 EndY=-309.31 EndZ=0
    g6: Circle CenterX=0 CenterY=-300 CenterZ=0 NormalX=0 NormalY=0 NormalZ=1 AngleXU=0 Radius=10.75
  constraints (17):
    c: Coincident(g0,g1)
    c: Coincident(g1,g2)
    c: Coincident(g2,g3)
    c: Coincident(g3,g4)
    c: Coincident(g4,g5)
    c: Coincident(g5,g0)
    c: Equal(g0, g1-g5) x5
    c: PointOnObject(g0,g6)
    c: PointOnObject(g1,g6)
    c: PointOnObject(g2,g6)
    c: PointOnObject(g3,g6)
    c: PointOnObject(g4,g6)
    c: PointOnObject(g5,g6)
    c: Horizontal(g5)
    c: DistanceX(g5,g5) = 10.75
    c: DistanceX(g6) = 0
    c: DistanceY(g6) = -300
FEATURE [Part::Extrusion] Extrude075
  Base = -> Sketch197
  Dir = (0,0,1)
  DirMode = 2
  FaceMakerClass = Part::FaceMakerBullseye
  LengthFwd = 20
  LengthRev = 0
  Reversed = true
  Solid = true
  Symmetric = false
FEATURE [Part::Extrusion] Extrude076
  Base = -> Sketch198
  Dir = (0,0,1)
  DirMode = 2
  FaceMakerClass = Part::FaceMakerBullseye
  LengthFwd = 1.5
  LengthRev = 0
  Reversed = true
  Solid = true
  Symmetric = false
FEATURE [Part::MultiFuse] Fusion135  label="pg7"
  Shapes = -> [Extrude075,Extrude076]
FEATURE [Part::Cut] Cut079  label="base026"
  Base = -> Cut078
  Tool = -> Fusion135
FEATURE [Sketcher::SketchObject] Sketch199  label="m6Cut002"
  FullyConstrained = true
  Placement = pos=(0,0,14.5) rot=(0,0,1;0rad)
  sketch-geometry (1):
    g0: Circle CenterX=0 CenterY=-263.25 CenterZ=0 NormalX=0 NormalY=0 NormalZ=1 AngleXU=0 Radius=6.5
  constraints (3):
    c: DistanceX(g0) = 0
    c: Diameter(g0) = 13
    c: DistanceY(g0) = -263.25
FEATURE [Part::Extrusion] Extrude077
  Base = -> Sketch199
  Dir = (0,0,1)
  DirMode = 2
  FaceMakerClass = Part::FaceMakerBullseye
  LengthFwd = 10
  LengthRev = 0
  Solid = true
  Symmetric = false
FEATURE [Part::Cut] Cut080  label="srs005"
  Base = -> Cut077
  Tool = -> Extrude077
FEATURE [Part::Fillet] Fillet082
  Base = -> Cut079
  Edges = 6 edges r=0.5: [Edge43,Edge44,Edge45,Edge46,Edge47,Edge48]
FEATURE [Part::Fillet] Fillet083  label="base027"
  Base = -> Fillet082
  Edges = 6 edges r=0.5: [Edge201,Edge211,Edge215,Edge219,Edge223,Edge228]
FEATURE [Part::Fillet] Fillet084
  Base = -> Cut080
  Edges = 5 edges r=2: [Edge58,Edge61,Edge80,Edge83,Edge84]
FEATURE [Part::Fillet] Fillet085
  Base = -> Fillet084
  Edges = 1 edges r=1: [Edge131]
FEATURE [Part::Fillet] Fillet086
  Base = -> Fillet085
  Edges = 3 edges r=2: [Edge48,Edge54,Edge68]
FEATURE [Part::Fillet] Fillet087
  Base = -> Fillet086
  Edges = 4 edges: [Edge6 r=2,Edge9 r=1,Edge28 r=2,Edge37 r=1]
FEATURE [Part::Fillet] Fillet088
  Base = -> Fillet087
  Edges = 2 edges r=3: [Edge34,Edge35]
FEATURE [Part::Fillet] Fillet089
  Base = -> Fillet088
  Edges = 6 edges r=2: [Edge1,Edge3,Edge4,Edge14,Edge20,Edge28]
FEATURE [Part::Fillet] Fillet090
  Base = -> Fillet089
  Edges = 17 edges r=0.5: [Edge47,Edge48,Edge49,Edge50,Edge51,Edge57,Edge120,Edge122,Edge124,Edge126,Edge128,Edge130,Edge131,Edge132,Edge133,Edge134,Edge135]
FEATURE [Part::Fillet] Fillet091
  Base = -> Fillet090
  Edges = 6 edges r=1: [Edge127,Edge175,Edge176,Edge177,Edge189,Edge190]
FEATURE [Part::Fillet] Fillet092
  Base = -> Fillet091
  Edges = 4 edges r=1.75: [Edge99,Edge103,Edge206,Edge210]
FEATURE [Sketcher::SketchObject] Sketch200  label="m6Cut003"
  FullyConstrained = true
  Placement = pos=(0,0,9) rot=(0,0,-1;0rad)
  sketch-geometry (1):
    g0: Circle CenterX=0 CenterY=-263.25 CenterZ=0 NormalX=0 NormalY=0 NormalZ=1 AngleXU=0 Radius=3.5
  constraints (3):
    c: DistanceX(g0) = 0
    c: Diameter(g0) = 7
    c: DistanceY(g0) = -263.25
FEATURE [Part::Extrusion] Extrude078
  Base = -> Sketch200
  Dir = (0,0,1)
  DirMode = 2
  FaceMakerClass = Part::FaceMakerBullseye
  LengthFwd = 10
  LengthRev = 0
  Solid = true
  Symmetric = false
FEATURE [Part::Cut] Cut081  label="srs006"
  Base = -> Fillet092
  Tool = -> Extrude078
FEATURE [Part::Fillet] Fillet093  label="srs007"
  Base = -> Cut081
  Edges = 1 edges r=0.5: [Edge233]
FEATURE [Part::Fillet] Fillet094
  Base = -> Cut063
  Edges = 8 edges: [Edge5 r=1,Edge6 r=2,Edge7 r=2,Edge8 r=1,Edge9 r=2,Edge10 r=2,Edge11 r=1,Edge14 r=1]
